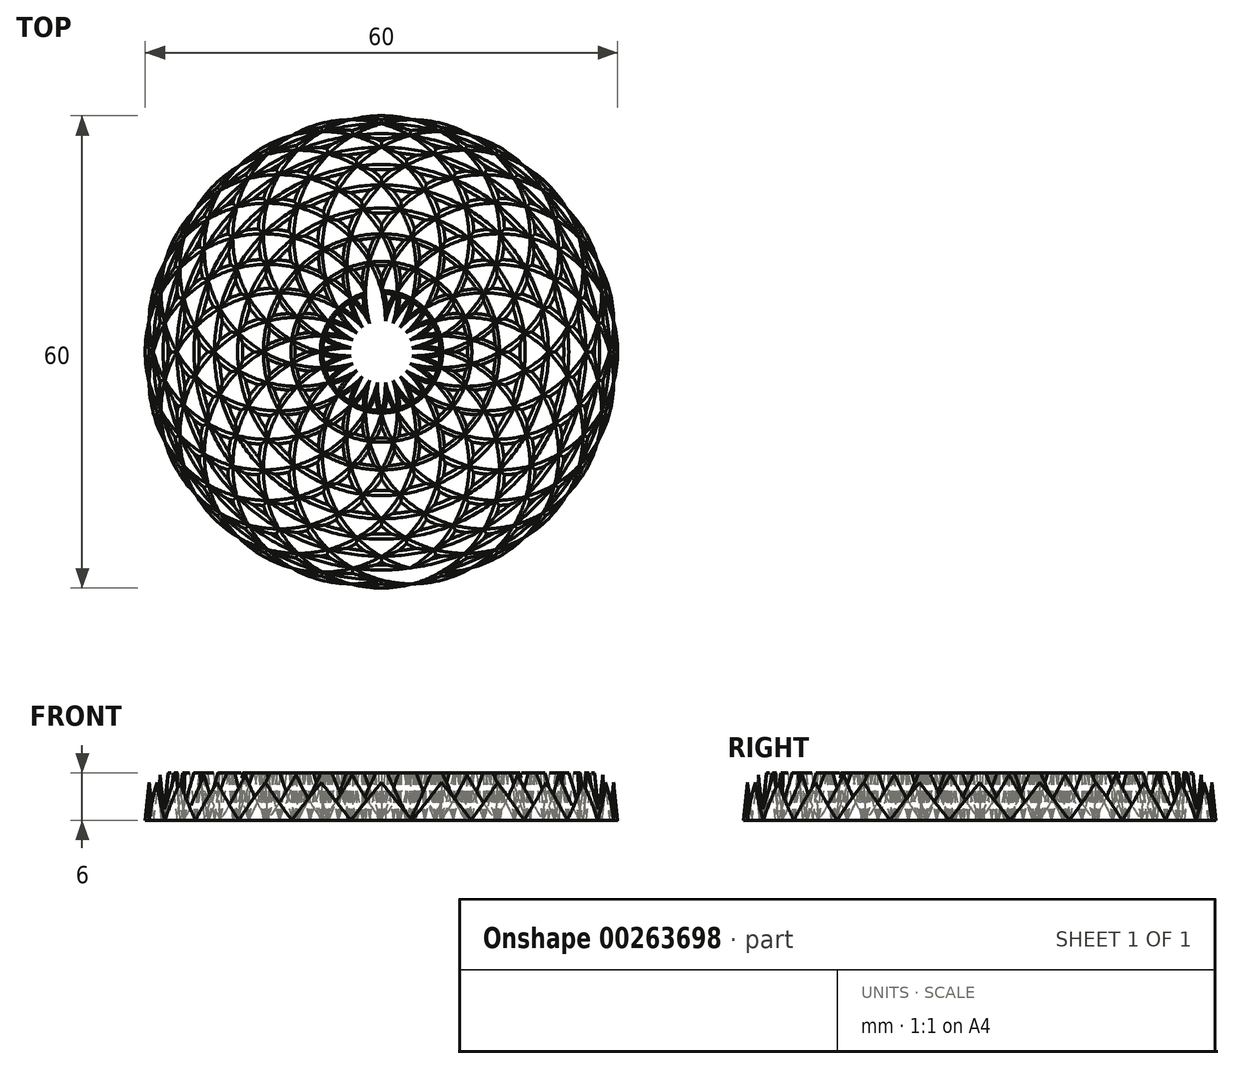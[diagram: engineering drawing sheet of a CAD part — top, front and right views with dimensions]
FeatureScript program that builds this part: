
annotation { "Feature Type Name" : "Feature", "Feature Type Description" : "" }
export const myFeature = defineFeature(function(context is Context, id is Id, definition is map)
    precondition{}
    {
        {
            var Q0;
            Q0=qCreatedBy(makeId("Top.planeOp"),FACE);
            var sketch = newSketch(context, id + "F0", { "sketchPlane" : qUnion([Q0])});
            skCircle(sketch, "E0", {"center": v(0, 0) * mm, "radius": 15 * mm});
            skLineSegment(sketch, "E1", {"start": v(-15, 0) * mm, "end": v(15, 0) * mm, "construction": true});
            skLineSegment(sketch, "E2", {"start": v(0, 15) * mm, "end": v(0, -15) * mm, "construction": true});
            skCircle(sketch, "E3", {"center": v(15, 0) * mm, "radius": 15 * mm});
            skCircle(sketch, "E4", {"center": v(7.5, 13) * mm, "radius": 15 * mm});
            skCircle(sketch, "E5", {"center": v(7.5, -13) * mm, "radius": 15 * mm});
            skCircle(sketch, "E6", {"center": v(-7.5, 13) * mm, "radius": 15 * mm});
            skCircle(sketch, "E7", {"center": v(-7.5, -13) * mm, "radius": 15 * mm});
            skCircle(sketch, "E8", {"center": v(-15, 0) * mm, "radius": 15 * mm});
            skLineSegment(sketch, "E9", {"start": v(0, 0) * mm, "end": v(22.5, 13) * mm, "construction": true});
            skCircle(sketch, "E10", {"center": v(13, 7.5) * mm, "radius": 15 * mm});
            skCircle(sketch, "E11", {"center": v(13, -7.5) * mm, "radius": 15 * mm});
            skCircle(sketch, "E12", {"center": v(0, -15) * mm, "radius": 15 * mm});
            skCircle(sketch, "E13", {"center": v(-13, -7.5) * mm, "radius": 15 * mm});
            skCircle(sketch, "E14", {"center": v(-13, 7.5) * mm, "radius": 15 * mm});
            skCircle(sketch, "E15", {"center": v(0, 15) * mm, "radius": 15 * mm});
            skLineSegment(sketch, "E16", {"start": v(7.5, 2) * mm, "end": v(20.5, 5.5) * mm, "construction": true});
            skCircle(sketch, "E17", {"center": v(14.49, 3.88) * mm, "radius": 15 * mm});
            skCircle(sketch, "E18", {"center": v(10.6, -10.6) * mm, "radius": 15 * mm});
            skCircle(sketch, "E19", {"center": v(-3.88, -14.49) * mm, "radius": 15 * mm});
            skCircle(sketch, "E20", {"center": v(-14.49, -3.88) * mm, "radius": 15 * mm});
            skCircle(sketch, "E21", {"center": v(-10.6, 10.6) * mm, "radius": 15 * mm});
            skCircle(sketch, "E22", {"center": v(3.88, 14.49) * mm, "radius": 15 * mm});
            skLineSegment(sketch, "E23", {"start": v(-2, 7.5) * mm, "end": v(-5.5, 20.5) * mm, "construction": true});
            skCircle(sketch, "E24", {"center": v(-3.88, 14.49) * mm, "radius": 15 * mm});
            skCircle(sketch, "E25", {"center": v(10.6, 10.6) * mm, "radius": 15 * mm});
            skCircle(sketch, "E26", {"center": v(14.49, -3.88) * mm, "radius": 15 * mm});
            skCircle(sketch, "E27", {"center": v(3.88, -14.49) * mm, "radius": 15 * mm});
            skCircle(sketch, "E28", {"center": v(-10.6, -10.6) * mm, "radius": 15 * mm});
            skCircle(sketch, "E29", {"center": v(-14.49, 3.88) * mm, "radius": 15 * mm});
            skCircle(sketch, "E30", {"center": v(0, 0) * mm, "radius": 18.26 * mm});
            skLineSegment(sketch, "E31", {"start": v(-6.99, 16.87) * mm, "end": v(-2.38, 18.1) * mm, "construction": true});
            skCircle(sketch, "E32", {"center": v(0, 0) * mm, "radius": 21.21 * mm});
            skLineSegment(sketch, "E33", {"start": v(0, 0) * mm, "end": v(7.5, 28) * mm, "construction": true});
            skCircle(sketch, "E34", {"center": v(0, 0) * mm, "radius": 28.98 * mm});
            skLineSegment(sketch, "E35", {"start": v(0, 0) * mm, "end": v(3.1, 23.6) * mm, "construction": true});
            skCircle(sketch, "E36", {"center": v(0, 0) * mm, "radius": 23.8 * mm});
            skLineSegment(sketch, "E37", {"start": v(0, 0) * mm, "end": v(-3.62, 27.48) * mm, "construction": true});
            skCircle(sketch, "E38", {"center": v(0, 0) * mm, "radius": 27.72 * mm});
            skLineSegment(sketch, "E39", {"start": v(0, 0) * mm, "end": v(-13, 22.5) * mm, "construction": true});
            skCircle(sketch, "E40", {"center": v(0, 0) * mm, "radius": 25.98 * mm});
            skLineSegment(sketch, "E41", {"start": v(0, 0) * mm, "end": v(-9.1, 6.99) * mm, "construction": true});
            skCircle(sketch, "E42", {"center": v(0, 0) * mm, "radius": 11.48 * mm});
            skLineSegment(sketch, "E43", {"start": v(0, 0) * mm, "end": v(-6.72, 3.88) * mm, "construction": true});
            skCircle(sketch, "E44", {"center": v(0, 0) * mm, "radius": 7.76 * mm});
            skLineSegment(sketch, "E45", {"start": v(0, 0) * mm, "end": v(-2.38, -3.1) * mm, "construction": true});
            skCircle(sketch, "E46", {"center": v(0, 0) * mm, "radius": 3.92 * mm});
            skSolve(sketch);
        }
        {
            var Q0;
            Q0=qCreatedBy(makeId("Top.planeOp"),FACE);
            cPlane(context, id + "F1", {"entities" : qUnion([Q0]), "cplaneType" : CPlaneType.OFFSET, "offset" : 0 * mm, "width" : 150 * mm, "height" : 150 * mm});
        }
        {
            var Q0;
            Q0=qCreatedBy(id+"F1.planeOp",FACE);
            var sketch = newSketch(context, id + "F2", { "sketchPlane" : qUnion([Q0])});
            skArc(sketch, "E47.0.0", {"start": v(-7.5, 2) * mm, "mid": v(-9.46, 1.88) * mm, "end": v(-11.38, 1.5) * mm});
            skArc(sketch, "E47.0.1", {"start": v(-11.38, 1.5) * mm, "mid": v(-9.62, 0.63) * mm, "end": v(-7.76, 0) * mm});
            skArc(sketch, "E48.0.1", {"start": v(-6.72, 3.88) * mm, "mid": v(-8.65, 4.27) * mm, "end": v(-10.6, 4.4) * mm});
            skArc(sketch, "E48.0.2", {"start": v(-10.6, 4.4) * mm, "mid": v(-9.13, 3.1) * mm, "end": v(-7.5, 2) * mm});
            skArc(sketch, "E49.0.1", {"start": v(-5.5, 5.5) * mm, "mid": v(-7.25, 6.36) * mm, "end": v(-9.1, 6.99) * mm});
            skArc(sketch, "E49.0.2", {"start": v(-9.1, 6.99) * mm, "mid": v(-8.02, 5.36) * mm, "end": v(-6.72, 3.88) * mm});
            skArc(sketch, "E50.0.0", {"start": v(-3.88, 6.72) * mm, "mid": v(-5.36, 8.02) * mm, "end": v(-6.99, 9.1) * mm});
            skArc(sketch, "E50.0.1", {"start": v(-6.99, 9.1) * mm, "mid": v(-6.36, 7.25) * mm, "end": v(-5.5, 5.5) * mm});
            skArc(sketch, "E51.0.1", {"start": v(-2, 7.5) * mm, "mid": v(-3.1, 9.13) * mm, "end": v(-4.4, 10.6) * mm});
            skArc(sketch, "E51.0.2", {"start": v(-4.4, 10.6) * mm, "mid": v(-4.27, 8.65) * mm, "end": v(-3.88, 6.72) * mm});
            skArc(sketch, "E52.0.1", {"start": v(0, 7.76) * mm, "mid": v(-0.63, 9.62) * mm, "end": v(-1.5, 11.38) * mm});
            skArc(sketch, "E52.0.2", {"start": v(-1.5, 11.38) * mm, "mid": v(-1.88, 9.46) * mm, "end": v(-2, 7.5) * mm});
            skArc(sketch, "E53.0.0", {"start": v(2, 7.5) * mm, "mid": v(1.88, 9.46) * mm, "end": v(1.5, 11.38) * mm});
            skArc(sketch, "E53.0.1", {"start": v(1.5, 11.38) * mm, "mid": v(0.63, 9.62) * mm, "end": v(0, 7.76) * mm});
            skArc(sketch, "E54.0.0", {"start": v(3.88, 6.72) * mm, "mid": v(4.27, 8.65) * mm, "end": v(4.4, 10.6) * mm});
            skArc(sketch, "E54.0.1", {"start": v(4.4, 10.6) * mm, "mid": v(3.1, 9.13) * mm, "end": v(2, 7.5) * mm});
            skArc(sketch, "E55.0.0", {"start": v(5.5, 5.5) * mm, "mid": v(6.36, 7.25) * mm, "end": v(6.99, 9.1) * mm});
            skArc(sketch, "E55.0.1", {"start": v(6.99, 9.1) * mm, "mid": v(5.36, 8.02) * mm, "end": v(3.88, 6.72) * mm});
            skArc(sketch, "E56.0.1", {"start": v(6.72, 3.88) * mm, "mid": v(8.02, 5.36) * mm, "end": v(9.1, 6.99) * mm});
            skArc(sketch, "E56.0.2", {"start": v(9.1, 6.99) * mm, "mid": v(7.25, 6.36) * mm, "end": v(5.5, 5.5) * mm});
            skArc(sketch, "E57.0.1", {"start": v(7.5, 2) * mm, "mid": v(9.13, 3.1) * mm, "end": v(10.6, 4.4) * mm});
            skArc(sketch, "E57.0.2", {"start": v(10.6, 4.4) * mm, "mid": v(8.65, 4.27) * mm, "end": v(6.72, 3.88) * mm});
            skArc(sketch, "E58.0.0", {"start": v(7.76, 0) * mm, "mid": v(9.62, 0.63) * mm, "end": v(11.38, 1.5) * mm});
            skArc(sketch, "E58.0.1", {"start": v(11.38, 1.5) * mm, "mid": v(9.46, 1.88) * mm, "end": v(7.5, 2) * mm});
            skArc(sketch, "E59.0.1", {"start": v(7.5, -2) * mm, "mid": v(9.46, -1.88) * mm, "end": v(11.38, -1.5) * mm});
            skArc(sketch, "E59.0.2", {"start": v(11.38, -1.5) * mm, "mid": v(9.62, -0.63) * mm, "end": v(7.76, 0) * mm});
            skArc(sketch, "E60.0.1", {"start": v(6.72, -3.88) * mm, "mid": v(8.65, -4.27) * mm, "end": v(10.6, -4.4) * mm});
            skArc(sketch, "E60.0.2", {"start": v(10.6, -4.4) * mm, "mid": v(9.13, -3.1) * mm, "end": v(7.5, -2) * mm});
            skArc(sketch, "E61.0.1", {"start": v(5.5, -5.5) * mm, "mid": v(7.25, -6.36) * mm, "end": v(9.1, -6.99) * mm});
            skArc(sketch, "E61.0.2", {"start": v(9.1, -6.99) * mm, "mid": v(8.02, -5.36) * mm, "end": v(6.72, -3.88) * mm});
            skArc(sketch, "E62.0.1", {"start": v(3.88, -6.72) * mm, "mid": v(5.36, -8.02) * mm, "end": v(6.99, -9.1) * mm});
            skArc(sketch, "E62.0.2", {"start": v(6.99, -9.1) * mm, "mid": v(6.36, -7.25) * mm, "end": v(5.5, -5.5) * mm});
            skArc(sketch, "E63.0.0", {"start": v(2, -7.5) * mm, "mid": v(3.1, -9.13) * mm, "end": v(4.4, -10.6) * mm});
            skArc(sketch, "E63.0.1", {"start": v(4.4, -10.6) * mm, "mid": v(4.27, -8.65) * mm, "end": v(3.88, -6.72) * mm});
            skArc(sketch, "E64.0.1", {"start": v(0, -7.76) * mm, "mid": v(0.63, -9.62) * mm, "end": v(1.5, -11.38) * mm});
            skArc(sketch, "E64.0.2", {"start": v(1.5, -11.38) * mm, "mid": v(1.88, -9.46) * mm, "end": v(2, -7.5) * mm});
            skArc(sketch, "E65.0.0", {"start": v(-2, -7.5) * mm, "mid": v(-1.88, -9.46) * mm, "end": v(-1.5, -11.38) * mm});
            skArc(sketch, "E65.0.1", {"start": v(-1.5, -11.38) * mm, "mid": v(-0.63, -9.62) * mm, "end": v(0, -7.76) * mm});
            skArc(sketch, "E66.0.1", {"start": v(-3.88, -6.72) * mm, "mid": v(-4.27, -8.65) * mm, "end": v(-4.4, -10.6) * mm});
            skArc(sketch, "E66.0.2", {"start": v(-4.4, -10.6) * mm, "mid": v(-3.1, -9.13) * mm, "end": v(-2, -7.5) * mm});
            skArc(sketch, "E67.0.0", {"start": v(-5.5, -5.5) * mm, "mid": v(-6.36, -7.25) * mm, "end": v(-6.99, -9.1) * mm});
            skArc(sketch, "E67.0.1", {"start": v(-6.99, -9.1) * mm, "mid": v(-5.36, -8.02) * mm, "end": v(-3.88, -6.72) * mm});
            skArc(sketch, "E68.0.1", {"start": v(-6.72, -3.88) * mm, "mid": v(-8.02, -5.36) * mm, "end": v(-9.1, -6.99) * mm});
            skArc(sketch, "E68.0.2", {"start": v(-9.1, -6.99) * mm, "mid": v(-7.25, -6.36) * mm, "end": v(-5.5, -5.5) * mm});
            skArc(sketch, "E69.0.1", {"start": v(-7.5, -2) * mm, "mid": v(-9.13, -3.1) * mm, "end": v(-10.6, -4.4) * mm});
            skArc(sketch, "E69.0.2", {"start": v(-10.6, -4.4) * mm, "mid": v(-8.65, -4.27) * mm, "end": v(-6.72, -3.88) * mm});
            skArc(sketch, "E70.0.1", {"start": v(-7.76, 0) * mm, "mid": v(-9.62, -0.63) * mm, "end": v(-11.38, -1.5) * mm});
            skArc(sketch, "E70.0.2", {"start": v(-11.38, -1.5) * mm, "mid": v(-9.46, -1.88) * mm, "end": v(-7.5, -2) * mm});
            skArc(sketch, "E71.0.1", {"start": v(-10.6, 4.4) * mm, "mid": v(-12.56, 4.27) * mm, "end": v(-14.49, 3.88) * mm});
            skArc(sketch, "E71.0.2", {"start": v(-14.49, 3.88) * mm, "mid": v(-13.01, 2.59) * mm, "end": v(-11.38, 1.5) * mm});
            skArc(sketch, "E72.0.1", {"start": v(-9.1, 6.99) * mm, "mid": v(-11.03, 7.37) * mm, "end": v(-13, 7.5) * mm});
            skArc(sketch, "E72.0.2", {"start": v(-13, 7.5) * mm, "mid": v(-11.9, 5.87) * mm, "end": v(-10.6, 4.4) * mm});
            skArc(sketch, "E73.0.1", {"start": v(-6.99, 9.1) * mm, "mid": v(-8.75, 9.98) * mm, "end": v(-10.6, 10.6) * mm});
            skArc(sketch, "E73.0.2", {"start": v(-10.6, 10.6) * mm, "mid": v(-9.98, 8.75) * mm, "end": v(-9.1, 6.99) * mm});
            skArc(sketch, "E74.0.1", {"start": v(-4.4, 10.6) * mm, "mid": v(-5.87, 11.9) * mm, "end": v(-7.5, 13) * mm});
            skArc(sketch, "E74.0.2", {"start": v(-7.5, 13) * mm, "mid": v(-7.37, 11.03) * mm, "end": v(-6.99, 9.1) * mm});
            skArc(sketch, "E75.0.1", {"start": v(-1.5, 11.38) * mm, "mid": v(-2.59, 13.01) * mm, "end": v(-3.88, 14.49) * mm});
            skArc(sketch, "E75.0.2", {"start": v(-3.88, 14.49) * mm, "mid": v(-4.27, 12.56) * mm, "end": v(-4.4, 10.6) * mm});
            skArc(sketch, "E76.0.0", {"start": v(1.5, 11.38) * mm, "mid": v(0.87, 13.24) * mm, "end": v(0, 15) * mm});
            skArc(sketch, "E76.0.1", {"start": v(0, 15) * mm, "mid": v(-0.87, 13.24) * mm, "end": v(-1.5, 11.38) * mm});
            skArc(sketch, "E77.0.1", {"start": v(4.4, 10.6) * mm, "mid": v(4.27, 12.56) * mm, "end": v(3.88, 14.49) * mm});
            skArc(sketch, "E77.0.2", {"start": v(3.88, 14.49) * mm, "mid": v(2.59, 13.01) * mm, "end": v(1.5, 11.38) * mm});
            skArc(sketch, "E78.0.1", {"start": v(6.99, 9.1) * mm, "mid": v(7.37, 11.03) * mm, "end": v(7.5, 13) * mm});
            skArc(sketch, "E78.0.2", {"start": v(7.5, 13) * mm, "mid": v(5.87, 11.9) * mm, "end": v(4.4, 10.6) * mm});
            skArc(sketch, "E79.0.1", {"start": v(9.1, 6.99) * mm, "mid": v(9.98, 8.75) * mm, "end": v(10.6, 10.6) * mm});
            skArc(sketch, "E79.0.2", {"start": v(10.6, 10.6) * mm, "mid": v(8.75, 9.98) * mm, "end": v(6.99, 9.1) * mm});
            skArc(sketch, "E80.0.0", {"start": v(10.6, 4.4) * mm, "mid": v(11.9, 5.87) * mm, "end": v(13, 7.5) * mm});
            skArc(sketch, "E80.0.1", {"start": v(13, 7.5) * mm, "mid": v(11.03, 7.37) * mm, "end": v(9.1, 6.99) * mm});
            skArc(sketch, "E81.0.1", {"start": v(11.38, 1.5) * mm, "mid": v(13.01, 2.59) * mm, "end": v(14.49, 3.88) * mm});
            skArc(sketch, "E81.0.2", {"start": v(14.49, 3.88) * mm, "mid": v(12.56, 4.27) * mm, "end": v(10.6, 4.4) * mm});
            skArc(sketch, "E82.0.0", {"start": v(11.38, -1.5) * mm, "mid": v(13.24, -0.87) * mm, "end": v(15, 0) * mm});
            skArc(sketch, "E82.0.1", {"start": v(15, 0) * mm, "mid": v(13.24, 0.87) * mm, "end": v(11.38, 1.5) * mm});
            skArc(sketch, "E83.0.1", {"start": v(10.6, -4.4) * mm, "mid": v(12.56, -4.27) * mm, "end": v(14.49, -3.88) * mm});
            skArc(sketch, "E83.0.2", {"start": v(14.49, -3.88) * mm, "mid": v(13.01, -2.59) * mm, "end": v(11.38, -1.5) * mm});
            skArc(sketch, "E84.0.1", {"start": v(9.1, -6.99) * mm, "mid": v(11.03, -7.37) * mm, "end": v(13, -7.5) * mm});
            skArc(sketch, "E84.0.2", {"start": v(13, -7.5) * mm, "mid": v(11.9, -5.87) * mm, "end": v(10.6, -4.4) * mm});
            skArc(sketch, "E85.0.1", {"start": v(6.99, -9.1) * mm, "mid": v(8.75, -9.98) * mm, "end": v(10.6, -10.6) * mm});
            skArc(sketch, "E85.0.2", {"start": v(10.6, -10.6) * mm, "mid": v(9.98, -8.75) * mm, "end": v(9.1, -6.99) * mm});
            skArc(sketch, "E86.0.0", {"start": v(4.4, -10.6) * mm, "mid": v(5.87, -11.9) * mm, "end": v(7.5, -13) * mm});
            skArc(sketch, "E86.0.1", {"start": v(7.5, -13) * mm, "mid": v(7.37, -11.03) * mm, "end": v(6.99, -9.1) * mm});
            skArc(sketch, "E87.0.1", {"start": v(1.5, -11.38) * mm, "mid": v(2.59, -13.01) * mm, "end": v(3.88, -14.49) * mm});
            skArc(sketch, "E87.0.2", {"start": v(3.88, -14.49) * mm, "mid": v(4.27, -12.56) * mm, "end": v(4.4, -10.6) * mm});
            skArc(sketch, "E88.0.1", {"start": v(-1.5, -11.38) * mm, "mid": v(-0.87, -13.24) * mm, "end": v(0, -15) * mm});
            skArc(sketch, "E88.0.2", {"start": v(0, -15) * mm, "mid": v(0.87, -13.24) * mm, "end": v(1.5, -11.38) * mm});
            skArc(sketch, "E89.0.1", {"start": v(-4.4, -10.6) * mm, "mid": v(-4.27, -12.56) * mm, "end": v(-3.88, -14.49) * mm});
            skArc(sketch, "E89.0.2", {"start": v(-3.88, -14.49) * mm, "mid": v(-2.59, -13.01) * mm, "end": v(-1.5, -11.38) * mm});
            skArc(sketch, "E90.0.1", {"start": v(-6.99, -9.1) * mm, "mid": v(-7.37, -11.03) * mm, "end": v(-7.5, -13) * mm});
            skArc(sketch, "E90.0.2", {"start": v(-7.5, -13) * mm, "mid": v(-5.87, -11.9) * mm, "end": v(-4.4, -10.6) * mm});
            skArc(sketch, "E91.0.0", {"start": v(-9.1, -6.99) * mm, "mid": v(-9.98, -8.75) * mm, "end": v(-10.6, -10.6) * mm});
            skArc(sketch, "E91.0.1", {"start": v(-10.6, -10.6) * mm, "mid": v(-8.75, -9.98) * mm, "end": v(-6.99, -9.1) * mm});
            skArc(sketch, "E92.0.1", {"start": v(-10.6, -4.4) * mm, "mid": v(-11.9, -5.87) * mm, "end": v(-13, -7.5) * mm});
            skArc(sketch, "E92.0.2", {"start": v(-13, -7.5) * mm, "mid": v(-11.03, -7.37) * mm, "end": v(-9.1, -6.99) * mm});
            skArc(sketch, "E93.0.0", {"start": v(-11.38, -1.5) * mm, "mid": v(-13.01, -2.59) * mm, "end": v(-14.49, -3.88) * mm});
            skArc(sketch, "E93.0.1", {"start": v(-14.49, -3.88) * mm, "mid": v(-12.56, -4.27) * mm, "end": v(-10.6, -4.4) * mm});
            skArc(sketch, "E94.0.1", {"start": v(-11.38, 1.5) * mm, "mid": v(-13.24, 0.87) * mm, "end": v(-15, 0) * mm});
            skArc(sketch, "E94.0.2", {"start": v(-15, 0) * mm, "mid": v(-13.24, -0.87) * mm, "end": v(-11.38, -1.5) * mm});
            skArc(sketch, "E95.0.0", {"start": v(-3.88, 6.72) * mm, "mid": v(-2.59, 5.25) * mm, "end": v(-1.5, 3.62) * mm});
            skArc(sketch, "E95.0.1", {"start": v(-1.5, 3.62) * mm, "mid": v(-1.88, 5.54) * mm, "end": v(-2, 7.5) * mm});
            skArc(sketch, "E95.0.2", {"start": v(-2, 7.5) * mm, "mid": v(-2.97, 7.17) * mm, "end": v(-3.88, 6.72) * mm});
            skArc(sketch, "E96.0.0", {"start": v(-2.38, 3.1) * mm, "mid": v(-3.25, 4.87) * mm, "end": v(-3.88, 6.72) * mm});
            skArc(sketch, "E96.0.1", {"start": v(-3.88, 6.72) * mm, "mid": v(-4.73, 6.16) * mm, "end": v(-5.5, 5.5) * mm});
            skArc(sketch, "E96.0.2", {"start": v(-5.5, 5.5) * mm, "mid": v(-3.86, 4.4) * mm, "end": v(-2.38, 3.1) * mm});
            skArc(sketch, "E97.0.0", {"start": v(-6.72, 3.88) * mm, "mid": v(-4.87, 3.25) * mm, "end": v(-3.1, 2.38) * mm});
            skArc(sketch, "E97.0.1", {"start": v(-3.1, 2.38) * mm, "mid": v(-4.4, 3.86) * mm, "end": v(-5.5, 5.5) * mm});
            skArc(sketch, "E98.0.0", {"start": v(-3.62, 1.5) * mm, "mid": v(-5.25, 2.59) * mm, "end": v(-6.72, 3.88) * mm});
            skArc(sketch, "E98.0.1", {"start": v(-6.72, 3.88) * mm, "mid": v(-7.17, 2.97) * mm, "end": v(-7.5, 2) * mm});
            skArc(sketch, "E98.0.2", {"start": v(-7.5, 2) * mm, "mid": v(-5.54, 1.88) * mm, "end": v(-3.62, 1.5) * mm});
            skArc(sketch, "E99.0.0", {"start": v(-3.88, 0.51) * mm, "mid": v(-5.74, 1.14) * mm, "end": v(-7.5, 2) * mm});
            skArc(sketch, "E99.0.1", {"start": v(-7.5, 2) * mm, "mid": v(-7.7, 1.01) * mm, "end": v(-7.76, 0) * mm});
            skArc(sketch, "E99.0.2", {"start": v(-7.76, 0) * mm, "mid": v(-5.84, 0.38) * mm, "end": v(-3.88, 0.51) * mm});
            skArc(sketch, "E100.0.0", {"start": v(-3.88, -0.51) * mm, "mid": v(-5.84, -0.38) * mm, "end": v(-7.76, 0) * mm});
            skArc(sketch, "E100.0.1", {"start": v(-7.76, 0) * mm, "mid": v(-7.7, -1.01) * mm, "end": v(-7.5, -2) * mm});
            skArc(sketch, "E100.0.2", {"start": v(-7.5, -2) * mm, "mid": v(-5.74, -1.14) * mm, "end": v(-3.88, -0.51) * mm});
            skArc(sketch, "E101.0.0", {"start": v(-3.62, -1.5) * mm, "mid": v(-5.54, -1.88) * mm, "end": v(-7.5, -2) * mm});
            skArc(sketch, "E101.0.1", {"start": v(-7.5, -2) * mm, "mid": v(-7.17, -2.97) * mm, "end": v(-6.72, -3.88) * mm});
            skArc(sketch, "E101.0.2", {"start": v(-6.72, -3.88) * mm, "mid": v(-5.25, -2.59) * mm, "end": v(-3.62, -1.5) * mm});
            skArc(sketch, "E102.0.0", {"start": v(-5.5, -5.5) * mm, "mid": v(-4.4, -3.86) * mm, "end": v(-3.1, -2.38) * mm});
            skArc(sketch, "E102.0.1", {"start": v(-3.1, -2.38) * mm, "mid": v(-4.87, -3.25) * mm, "end": v(-6.72, -3.88) * mm});
            skArc(sketch, "E102.0.2", {"start": v(-6.72, -3.88) * mm, "mid": v(-6.16, -4.73) * mm, "end": v(-5.5, -5.5) * mm});
            skArc(sketch, "E103.0.0", {"start": v(-2.38, -3.1) * mm, "mid": v(-3.86, -4.4) * mm, "end": v(-5.5, -5.5) * mm});
            skArc(sketch, "E103.0.1", {"start": v(-5.5, -5.5) * mm, "mid": v(-4.73, -6.16) * mm, "end": v(-3.88, -6.72) * mm});
            skArc(sketch, "E103.0.2", {"start": v(-3.88, -6.72) * mm, "mid": v(-3.25, -4.87) * mm, "end": v(-2.38, -3.1) * mm});
            skArc(sketch, "E104.0.0", {"start": v(-1.5, -3.62) * mm, "mid": v(-2.59, -5.25) * mm, "end": v(-3.88, -6.72) * mm});
            skArc(sketch, "E104.0.1", {"start": v(-3.88, -6.72) * mm, "mid": v(-2.97, -7.17) * mm, "end": v(-2, -7.5) * mm});
            skArc(sketch, "E104.0.2", {"start": v(-2, -7.5) * mm, "mid": v(-1.88, -5.54) * mm, "end": v(-1.5, -3.62) * mm});
            skArc(sketch, "E105.0.0", {"start": v(0, -7.76) * mm, "mid": v(-0.38, -5.84) * mm, "end": v(-0.51, -3.88) * mm});
            skArc(sketch, "E105.0.1", {"start": v(-0.51, -3.88) * mm, "mid": v(-1.14, -5.74) * mm, "end": v(-2, -7.5) * mm});
            skArc(sketch, "E105.0.2", {"start": v(-2, -7.5) * mm, "mid": v(-1.01, -7.7) * mm, "end": v(0, -7.76) * mm});
            skArc(sketch, "E106.0.0", {"start": v(0.51, -3.88) * mm, "mid": v(0.38, -5.84) * mm, "end": v(0, -7.76) * mm});
            skArc(sketch, "E106.0.1", {"start": v(0, -7.76) * mm, "mid": v(1.01, -7.7) * mm, "end": v(2, -7.5) * mm});
            skArc(sketch, "E106.0.2", {"start": v(2, -7.5) * mm, "mid": v(1.14, -5.74) * mm, "end": v(0.51, -3.88) * mm});
            skArc(sketch, "E107.0.0", {"start": v(1.5, -3.62) * mm, "mid": v(1.88, -5.54) * mm, "end": v(2, -7.5) * mm});
            skArc(sketch, "E107.0.1", {"start": v(2, -7.5) * mm, "mid": v(2.97, -7.17) * mm, "end": v(3.88, -6.72) * mm});
            skArc(sketch, "E107.0.2", {"start": v(3.88, -6.72) * mm, "mid": v(2.59, -5.25) * mm, "end": v(1.5, -3.62) * mm});
            skArc(sketch, "E108.0.0", {"start": v(2.38, -3.1) * mm, "mid": v(3.25, -4.87) * mm, "end": v(3.88, -6.72) * mm});
            skArc(sketch, "E108.0.1", {"start": v(3.88, -6.72) * mm, "mid": v(4.73, -6.16) * mm, "end": v(5.5, -5.5) * mm});
            skArc(sketch, "E108.0.2", {"start": v(5.5, -5.5) * mm, "mid": v(3.86, -4.4) * mm, "end": v(2.38, -3.1) * mm});
            skArc(sketch, "E109.0.0", {"start": v(3.1, -2.38) * mm, "mid": v(4.4, -3.86) * mm, "end": v(5.5, -5.5) * mm});
            skArc(sketch, "E109.0.1", {"start": v(5.5, -5.5) * mm, "mid": v(6.16, -4.73) * mm, "end": v(6.72, -3.88) * mm});
            skArc(sketch, "E109.0.2", {"start": v(6.72, -3.88) * mm, "mid": v(4.87, -3.25) * mm, "end": v(3.1, -2.38) * mm});
            skArc(sketch, "E110.0.0", {"start": v(7.5, -2) * mm, "mid": v(5.54, -1.88) * mm, "end": v(3.62, -1.5) * mm});
            skArc(sketch, "E110.0.1", {"start": v(3.62, -1.5) * mm, "mid": v(5.25, -2.59) * mm, "end": v(6.72, -3.88) * mm});
            skArc(sketch, "E110.0.2", {"start": v(6.72, -3.88) * mm, "mid": v(7.17, -2.97) * mm, "end": v(7.5, -2) * mm});
            skArc(sketch, "E111.0.0", {"start": v(3.88, -0.51) * mm, "mid": v(5.74, -1.14) * mm, "end": v(7.5, -2) * mm});
            skArc(sketch, "E111.0.1", {"start": v(7.5, -2) * mm, "mid": v(7.7, -1.01) * mm, "end": v(7.76, 0) * mm});
            skArc(sketch, "E111.0.2", {"start": v(7.76, 0) * mm, "mid": v(5.84, -0.38) * mm, "end": v(3.88, -0.51) * mm});
            skArc(sketch, "E112.0.0", {"start": v(7.5, 2) * mm, "mid": v(5.74, 1.14) * mm, "end": v(3.88, 0.51) * mm});
            skArc(sketch, "E112.0.1", {"start": v(3.88, 0.51) * mm, "mid": v(5.84, 0.38) * mm, "end": v(7.76, 0) * mm});
            skArc(sketch, "E112.0.2", {"start": v(7.76, 0) * mm, "mid": v(7.7, 1.01) * mm, "end": v(7.5, 2) * mm});
            skArc(sketch, "E113.0.0", {"start": v(6.72, 3.88) * mm, "mid": v(5.25, 2.59) * mm, "end": v(3.62, 1.5) * mm});
            skArc(sketch, "E113.0.1", {"start": v(3.62, 1.5) * mm, "mid": v(5.54, 1.88) * mm, "end": v(7.5, 2) * mm});
            skArc(sketch, "E113.0.2", {"start": v(7.5, 2) * mm, "mid": v(7.17, 2.97) * mm, "end": v(6.72, 3.88) * mm});
            skArc(sketch, "E114.0.0", {"start": v(3.1, 2.38) * mm, "mid": v(4.87, 3.25) * mm, "end": v(6.72, 3.88) * mm});
            skArc(sketch, "E114.0.1", {"start": v(6.72, 3.88) * mm, "mid": v(6.16, 4.73) * mm, "end": v(5.5, 5.5) * mm});
            skArc(sketch, "E114.0.2", {"start": v(5.5, 5.5) * mm, "mid": v(4.4, 3.86) * mm, "end": v(3.1, 2.38) * mm});
            skArc(sketch, "E115.0.0", {"start": v(2.38, 3.1) * mm, "mid": v(3.86, 4.4) * mm, "end": v(5.5, 5.5) * mm});
            skArc(sketch, "E115.0.1", {"start": v(5.5, 5.5) * mm, "mid": v(4.73, 6.16) * mm, "end": v(3.88, 6.72) * mm});
            skArc(sketch, "E115.0.2", {"start": v(3.88, 6.72) * mm, "mid": v(3.25, 4.87) * mm, "end": v(2.38, 3.1) * mm});
            skArc(sketch, "E116.0.0", {"start": v(1.5, 3.62) * mm, "mid": v(2.59, 5.25) * mm, "end": v(3.88, 6.72) * mm});
            skArc(sketch, "E116.0.1", {"start": v(3.88, 6.72) * mm, "mid": v(2.97, 7.17) * mm, "end": v(2, 7.5) * mm});
            skArc(sketch, "E116.0.2", {"start": v(2, 7.5) * mm, "mid": v(1.88, 5.54) * mm, "end": v(1.5, 3.62) * mm});
            skArc(sketch, "E117.0.0", {"start": v(0.51, 3.88) * mm, "mid": v(1.14, 5.74) * mm, "end": v(2, 7.5) * mm});
            skArc(sketch, "E117.0.1", {"start": v(2, 7.5) * mm, "mid": v(1.01, 7.7) * mm, "end": v(0, 7.76) * mm});
            skArc(sketch, "E117.0.2", {"start": v(0, 7.76) * mm, "mid": v(0.38, 5.84) * mm, "end": v(0.51, 3.88) * mm});
            skArc(sketch, "E118.0.0", {"start": v(-2, 7.5) * mm, "mid": v(-1.14, 5.74) * mm, "end": v(-0.51, 3.88) * mm});
            skArc(sketch, "E118.0.1", {"start": v(-0.51, 3.88) * mm, "mid": v(-0.38, 5.84) * mm, "end": v(0, 7.76) * mm});
            skArc(sketch, "E118.0.2", {"start": v(0, 7.76) * mm, "mid": v(-1.01, 7.7) * mm, "end": v(-2, 7.5) * mm});
            skArc(sketch, "E119.0.0", {"start": v(0, 0) * mm, "mid": v(0.87, 1.76) * mm, "end": v(1.5, 3.62) * mm});
            skArc(sketch, "E119.0.1", {"start": v(1.5, 3.62) * mm, "mid": v(0.63, 1.86) * mm, "end": v(0, 0) * mm});
            skArc(sketch, "E120.0.0", {"start": v(0, 0) * mm, "mid": v(1.3, 1.48) * mm, "end": v(2.38, 3.1) * mm});
            skArc(sketch, "E120.0.1", {"start": v(2.38, 3.1) * mm, "mid": v(1.1, 1.63) * mm, "end": v(0, 0) * mm});
            skArc(sketch, "E121.0.0", {"start": v(3.1, 2.38) * mm, "mid": v(1.48, 1.3) * mm, "end": v(0, 0) * mm});
            skArc(sketch, "E121.0.1", {"start": v(0, 0) * mm, "mid": v(1.63, 1.1) * mm, "end": v(3.1, 2.38) * mm});
            skArc(sketch, "E122.0.0", {"start": v(3.62, 1.5) * mm, "mid": v(1.76, 0.87) * mm, "end": v(0, 0) * mm});
            skArc(sketch, "E122.0.1", {"start": v(0, 0) * mm, "mid": v(1.86, 0.63) * mm, "end": v(3.62, 1.5) * mm});
            skArc(sketch, "E123.0.0", {"start": v(3.88, 0.51) * mm, "mid": v(1.92, 0.38) * mm, "end": v(0, 0) * mm});
            skArc(sketch, "E123.0.1", {"start": v(0, 0) * mm, "mid": v(1.96, 0.13) * mm, "end": v(3.88, 0.51) * mm});
            skArc(sketch, "E124.0.0", {"start": v(3.88, -0.51) * mm, "mid": v(1.96, -0.13) * mm, "end": v(0, 0) * mm});
            skArc(sketch, "E124.0.1", {"start": v(0, 0) * mm, "mid": v(1.92, -0.38) * mm, "end": v(3.88, -0.51) * mm});
            skArc(sketch, "E125.0.0", {"start": v(3.62, -1.5) * mm, "mid": v(1.86, -0.63) * mm, "end": v(0, 0) * mm});
            skArc(sketch, "E125.0.1", {"start": v(0, 0) * mm, "mid": v(1.76, -0.87) * mm, "end": v(3.62, -1.5) * mm});
            skArc(sketch, "E126.0.0", {"start": v(3.1, -2.38) * mm, "mid": v(1.63, -1.1) * mm, "end": v(0, 0) * mm});
            skArc(sketch, "E126.0.1", {"start": v(0, 0) * mm, "mid": v(1.48, -1.3) * mm, "end": v(3.1, -2.38) * mm});
            skArc(sketch, "E127.0.0", {"start": v(0, 0) * mm, "mid": v(1.1, -1.63) * mm, "end": v(2.38, -3.1) * mm});
            skArc(sketch, "E127.0.1", {"start": v(2.38, -3.1) * mm, "mid": v(1.3, -1.48) * mm, "end": v(0, 0) * mm});
            skArc(sketch, "E128.0.0", {"start": v(0, 0) * mm, "mid": v(0.63, -1.86) * mm, "end": v(1.5, -3.62) * mm});
            skArc(sketch, "E128.0.1", {"start": v(1.5, -3.62) * mm, "mid": v(0.87, -1.76) * mm, "end": v(0, 0) * mm});
            skArc(sketch, "E129.0.0", {"start": v(0, 0) * mm, "mid": v(0.13, -1.96) * mm, "end": v(0.51, -3.88) * mm});
            skArc(sketch, "E129.0.1", {"start": v(0.51, -3.88) * mm, "mid": v(0.38, -1.92) * mm, "end": v(0, 0) * mm});
            skArc(sketch, "E130.0.0", {"start": v(-0.51, -3.88) * mm, "mid": v(-0.13, -1.96) * mm, "end": v(0, 0) * mm});
            skArc(sketch, "E130.0.1", {"start": v(0, 0) * mm, "mid": v(-0.38, -1.92) * mm, "end": v(-0.51, -3.88) * mm});
            skArc(sketch, "E131.0.0", {"start": v(0, 0) * mm, "mid": v(-0.87, -1.76) * mm, "end": v(-1.5, -3.62) * mm});
            skArc(sketch, "E131.0.1", {"start": v(-1.5, -3.62) * mm, "mid": v(-0.63, -1.86) * mm, "end": v(0, 0) * mm});
            skArc(sketch, "E132.0.0", {"start": v(0, 0) * mm, "mid": v(-1.3, -1.48) * mm, "end": v(-2.38, -3.1) * mm});
            skArc(sketch, "E132.0.1", {"start": v(-2.38, -3.1) * mm, "mid": v(-1.1, -1.63) * mm, "end": v(0, 0) * mm});
            skArc(sketch, "E133.0.0", {"start": v(-3.1, -2.38) * mm, "mid": v(-1.48, -1.3) * mm, "end": v(0, 0) * mm});
            skArc(sketch, "E133.0.1", {"start": v(0, 0) * mm, "mid": v(-1.63, -1.1) * mm, "end": v(-3.1, -2.38) * mm});
            skArc(sketch, "E134.0.0", {"start": v(-3.62, -1.5) * mm, "mid": v(-1.76, -0.87) * mm, "end": v(0, 0) * mm});
            skArc(sketch, "E134.0.1", {"start": v(0, 0) * mm, "mid": v(-1.86, -0.63) * mm, "end": v(-3.62, -1.5) * mm});
            skArc(sketch, "E135.0.0", {"start": v(0, 0) * mm, "mid": v(-1.96, -0.13) * mm, "end": v(-3.88, -0.51) * mm});
            skArc(sketch, "E135.0.1", {"start": v(-3.88, -0.51) * mm, "mid": v(-1.92, -0.38) * mm, "end": v(0, 0) * mm});
            skArc(sketch, "E136.0.0", {"start": v(0, 0) * mm, "mid": v(-1.92, 0.38) * mm, "end": v(-3.88, 0.51) * mm});
            skArc(sketch, "E136.0.1", {"start": v(-3.88, 0.51) * mm, "mid": v(-1.96, 0.13) * mm, "end": v(0, 0) * mm});
            skArc(sketch, "E137.0.0", {"start": v(0, 0) * mm, "mid": v(-1.76, 0.87) * mm, "end": v(-3.62, 1.5) * mm});
            skArc(sketch, "E137.0.1", {"start": v(-3.62, 1.5) * mm, "mid": v(-1.86, 0.63) * mm, "end": v(0, 0) * mm});
            skArc(sketch, "E138.0.0", {"start": v(-3.1, 2.38) * mm, "mid": v(-1.63, 1.1) * mm, "end": v(0, 0) * mm});
            skArc(sketch, "E138.0.1", {"start": v(0, 0) * mm, "mid": v(-1.48, 1.3) * mm, "end": v(-3.1, 2.38) * mm});
            skArc(sketch, "E139.0.0", {"start": v(-2.38, 3.1) * mm, "mid": v(-1.3, 1.48) * mm, "end": v(0, 0) * mm});
            skArc(sketch, "E139.0.1", {"start": v(0, 0) * mm, "mid": v(-1.1, 1.63) * mm, "end": v(-2.38, 3.1) * mm});
            skArc(sketch, "E140.0.0", {"start": v(-1.5, 3.62) * mm, "mid": v(-0.87, 1.76) * mm, "end": v(0, 0) * mm});
            skArc(sketch, "E140.0.1", {"start": v(0, 0) * mm, "mid": v(-0.63, 1.86) * mm, "end": v(-1.5, 3.62) * mm});
            skArc(sketch, "E141.0.0", {"start": v(0, 0) * mm, "mid": v(-0.13, 1.96) * mm, "end": v(-0.51, 3.88) * mm});
            skArc(sketch, "E141.0.1", {"start": v(-0.51, 3.88) * mm, "mid": v(-0.38, 1.92) * mm, "end": v(0, 0) * mm});
            skArc(sketch, "E142.0.0", {"start": v(0, 0) * mm, "mid": v(0.38, 1.92) * mm, "end": v(0.51, 3.88) * mm});
            skArc(sketch, "E142.0.1", {"start": v(0.51, 3.88) * mm, "mid": v(0.13, 1.96) * mm, "end": v(0, 0) * mm});
            skCircle(sketch, "E143.0", {"center": v(0, 0) * mm, "radius": 7.76 * mm});
            skCircle(sketch, "E144.0", {"center": v(0, 0) * mm, "radius": 11.48 * mm});
            skCircle(sketch, "E145.0", {"center": v(0, 0) * mm, "radius": 15 * mm});
            skCircle(sketch, "E146.0", {"center": v(0, 0) * mm, "radius": 18.26 * mm});
            skCircle(sketch, "E147.0", {"center": v(0, 0) * mm, "radius": 21.21 * mm});
            skCircle(sketch, "E148.0", {"center": v(0, 0) * mm, "radius": 23.8 * mm});
            skCircle(sketch, "E149.0", {"center": v(0, 0) * mm, "radius": 25.98 * mm});
            skCircle(sketch, "E150.0", {"center": v(0, 0) * mm, "radius": 27.72 * mm});
            skCircle(sketch, "E151.0", {"center": v(0, 0) * mm, "radius": 28.98 * mm});
            skSolve(sketch);
        }
        {
            var Q0;
            Q0=makeQuery(id+"F2.imprint","IMPRINT",FACE,{"disambiguationData":[TD([[makeQuery(id+"F2.imprint","IMPRINT",EDGE,{"derivedFrom":sQuery(id+"F2.wireOp",EDGE,"E117.0.2")}),-1.0]])]});
            var Q1;
            Q1=makeQuery(id+"F2.imprint","IMPRINT",FACE,{"disambiguationData":[TD([[makeQuery(id+"F2.imprint","IMPRINT",EDGE,{"derivedFrom":sQuery(id+"F2.wireOp",EDGE,"E116.0.2")}),-1.0]])]});
            var Q2;
            Q2=makeQuery(id+"F2.imprint","IMPRINT",FACE,{"disambiguationData":[TD([[makeQuery(id+"F2.imprint","IMPRINT",EDGE,{"derivedFrom":sQuery(id+"F2.wireOp",EDGE,"E115.0.2")}),-1.0]])]});
            var Q3;
            Q3=makeQuery(id+"F2.imprint","IMPRINT",FACE,{"disambiguationData":[TD([[makeQuery(id+"F2.imprint","IMPRINT",EDGE,{"derivedFrom":sQuery(id+"F2.wireOp",EDGE,"E114.0.2")}),-1.0]])]});
            var Q4;
            Q4=makeQuery(id+"F2.imprint","IMPRINT",FACE,{"disambiguationData":[TD([[makeQuery(id+"F2.imprint","IMPRINT",EDGE,{"derivedFrom":sQuery(id+"F2.wireOp",EDGE,"E113.0.0")}),-1.0]])]});
            var Q5;
            Q5=makeQuery(id+"F2.imprint","IMPRINT",FACE,{"disambiguationData":[TD([[makeQuery(id+"F2.imprint","IMPRINT",EDGE,{"derivedFrom":sQuery(id+"F2.wireOp",EDGE,"E112.0.0")}),-1.0]])]});
            var Q6;
            Q6=makeQuery(id+"F2.imprint","IMPRINT",FACE,{"disambiguationData":[TD([[makeQuery(id+"F2.imprint","IMPRINT",EDGE,{"derivedFrom":sQuery(id+"F2.wireOp",EDGE,"E111.0.2")}),-1.0]])]});
            var Q7;
            Q7=makeQuery(id+"F2.imprint","IMPRINT",FACE,{"disambiguationData":[TD([[makeQuery(id+"F2.imprint","IMPRINT",EDGE,{"derivedFrom":sQuery(id+"F2.wireOp",EDGE,"E110.0.0")}),-1.0]])]});
            var Q8;
            Q8=makeQuery(id+"F2.imprint","IMPRINT",FACE,{"disambiguationData":[TD([[makeQuery(id+"F2.imprint","IMPRINT",EDGE,{"derivedFrom":sQuery(id+"F2.wireOp",EDGE,"E109.0.2")}),-1.0]])]});
            var Q9;
            Q9=makeQuery(id+"F2.imprint","IMPRINT",FACE,{"disambiguationData":[TD([[makeQuery(id+"F2.imprint","IMPRINT",EDGE,{"derivedFrom":sQuery(id+"F2.wireOp",EDGE,"E108.0.2")}),-1.0]])]});
            var Q10;
            Q10=makeQuery(id+"F2.imprint","IMPRINT",FACE,{"disambiguationData":[TD([[makeQuery(id+"F2.imprint","IMPRINT",EDGE,{"derivedFrom":sQuery(id+"F2.wireOp",EDGE,"E106.0.2")}),-1.0]])]});
            var Q11;
            Q11=makeQuery(id+"F2.imprint","IMPRINT",FACE,{"disambiguationData":[TD([[makeQuery(id+"F2.imprint","IMPRINT",EDGE,{"derivedFrom":sQuery(id+"F2.wireOp",EDGE,"E104.0.2")}),-1.0]])]});
            var Q12;
            Q12=makeQuery(id+"F2.imprint","IMPRINT",FACE,{"disambiguationData":[TD([[makeQuery(id+"F2.imprint","IMPRINT",EDGE,{"derivedFrom":sQuery(id+"F2.wireOp",EDGE,"E103.0.2")}),-1.0]])]});
            var Q13;
            Q13=makeQuery(id+"F2.imprint","IMPRINT",FACE,{"disambiguationData":[TD([[makeQuery(id+"F2.imprint","IMPRINT",EDGE,{"derivedFrom":sQuery(id+"F2.wireOp",EDGE,"E102.0.0")}),-1.0]])]});
            var Q14;
            Q14=makeQuery(id+"F2.imprint","IMPRINT",FACE,{"disambiguationData":[TD([[makeQuery(id+"F2.imprint","IMPRINT",EDGE,{"derivedFrom":sQuery(id+"F2.wireOp",EDGE,"E101.0.2")}),-1.0]])]});
            var Q15;
            Q15=makeQuery(id+"F2.imprint","IMPRINT",FACE,{"disambiguationData":[TD([[makeQuery(id+"F2.imprint","IMPRINT",EDGE,{"derivedFrom":sQuery(id+"F2.wireOp",EDGE,"E100.0.2")}),-1.0]])]});
            var Q16;
            Q16=makeQuery(id+"F2.imprint","IMPRINT",FACE,{"disambiguationData":[TD([[makeQuery(id+"F2.imprint","IMPRINT",EDGE,{"derivedFrom":sQuery(id+"F2.wireOp",EDGE,"E99.0.2")}),-1.0]])]});
            var Q17;
            Q17=makeQuery(id+"F2.imprint","IMPRINT",FACE,{"disambiguationData":[TD([[makeQuery(id+"F2.imprint","IMPRINT",EDGE,{"derivedFrom":sQuery(id+"F2.wireOp",EDGE,"E98.0.2")}),-1.0]])]});
            var Q18;
            Q18=makeQuery(id+"F2.imprint","IMPRINT",FACE,{"disambiguationData":[TD([[makeQuery(id+"F2.imprint","IMPRINT",EDGE,{"derivedFrom":sQuery(id+"F2.wireOp",EDGE,"E96.0.2")}),-1.0]])]});
            var Q19;
            Q19=makeQuery(id+"F2.imprint","IMPRINT",FACE,{"disambiguationData":[TD([[makeQuery(id+"F2.imprint","IMPRINT",EDGE,{"derivedFrom":sQuery(id+"F2.wireOp",EDGE,"E95.0.0")}),-1.0]])]});
            var Q20;
            Q20=makeQuery(id+"F2.imprint","IMPRINT",FACE,{"disambiguationData":[TD([[makeQuery(id+"F2.imprint","IMPRINT",EDGE,{"derivedFrom":sQuery(id+"F2.wireOp",EDGE,"E95.0.1")}),-1.0]])]});
            var Q21;
            Q21=makeQuery(id+"F2.imprint","IMPRINT",FACE,{"disambiguationData":[TD([[makeQuery(id+"F2.imprint","IMPRINT",EDGE,{"derivedFrom":sQuery(id+"F2.wireOp",EDGE,"E105.0.0")}),-1.0]])]});
            var Q22;
            Q22=makeQuery(id+"F2.imprint","IMPRINT",FACE,{"disambiguationData":[TD([[makeQuery(id+"F2.imprint","IMPRINT",EDGE,{"derivedFrom":sQuery(id+"F2.wireOp",EDGE,"E107.0.2")}),-1.0]])]});
            var Q23;
            Q23=makeQuery(id+"F2.imprint","IMPRINT",FACE,{"disambiguationData":[TD([[makeQuery(id+"F2.imprint","IMPRINT",EDGE,{"derivedFrom":sQuery(id+"F2.wireOp",EDGE,"E97.0.0")}),-1.0]])]});
            extrude(context, id + "F3", {"entities" : qUnion([Q0, Q1, Q2, Q3, Q4, Q5, Q6, Q7, Q8, Q9, Q10, Q11, Q12, Q13, Q14, Q15, Q16, Q17, Q18, Q19, Q20, Q21, Q22, Q23]), "depth" : 6 * mm, "hasDraft" : true, "draftAngle" : 3 * degree, "draftPullDirection" : true});
        }
        {
            var Q0;
            {var subQ0=sQuery(id+"F0.wireOp",EDGE,"E42");var subQ1=sQuery(id+"F0.wireOp",EDGE,"E17");var subQ2=makeQuery(id+"F0.imprint","INTERSECT",VERTEX,{"derivedFrom":[sQuery(id+"F0.wireOp",EDGE,"E7"),subQ1,subQ0]});Q0=makeQuery(id+"F0.imprint","IMPRINT",FACE,{"disambiguationData":[TD([[makeQuery(id+"F0.imprint","IMPRINT",EDGE,{"disambiguationData":[TD([[subQ2,1.0]])],"derivedFrom":subQ1}),-1.0]])]});}
            var Q1;
            {var subQ0=sQuery(id+"F0.wireOp",EDGE,"E28");var subQ1=sQuery(id+"F0.wireOp",EDGE,"E0");var subQ2=makeQuery(id+"F0.imprint","INTERSECT",VERTEX,{"derivedFrom":[subQ1,sQuery(id+"F0.wireOp",EDGE,"E26"),subQ0]});Q1=makeQuery(id+"F0.imprint","IMPRINT",FACE,{"disambiguationData":[TD([[makeQuery(id+"F0.imprint","IMPRINT",EDGE,{"disambiguationData":[TD([[subQ2,-1.0]])],"derivedFrom":subQ1}),1.0]])]});}
            var Q2;
            {var subQ0=sQuery(id+"F0.wireOp",EDGE,"E7");var subQ1=sQuery(id+"F0.wireOp",EDGE,"E0");var subQ2=makeQuery(id+"F0.imprint","INTERSECT",VERTEX,{"derivedFrom":[subQ1,sQuery(id+"F0.wireOp",EDGE,"E3"),subQ0]});Q2=makeQuery(id+"F0.imprint","IMPRINT",FACE,{"disambiguationData":[TD([[makeQuery(id+"F0.imprint","IMPRINT",EDGE,{"disambiguationData":[TD([[subQ2,-1.0]])],"derivedFrom":subQ1}),1.0]])]});}
            var Q3;
            {var subQ0=sQuery(id+"F0.wireOp",EDGE,"E42");var subQ1=sQuery(id+"F0.wireOp",EDGE,"E7");var subQ2=makeQuery(id+"F0.imprint","INTERSECT",VERTEX,{"derivedFrom":[subQ1,sQuery(id+"F0.wireOp",EDGE,"E17"),subQ0]});Q3=makeQuery(id+"F0.imprint","IMPRINT",FACE,{"disambiguationData":[TD([[makeQuery(id+"F0.imprint","IMPRINT",EDGE,{"disambiguationData":[TD([[subQ2,-1.0]])],"derivedFrom":subQ1}),-1.0]])]});}
            var Q4;
            {var subQ0=sQuery(id+"F0.wireOp",EDGE,"E19");var subQ1=sQuery(id+"F0.wireOp",EDGE,"E0");var subQ2=makeQuery(id+"F0.imprint","INTERSECT",VERTEX,{"derivedFrom":[subQ1,sQuery(id+"F0.wireOp",EDGE,"E17"),subQ0]});Q4=makeQuery(id+"F0.imprint","IMPRINT",FACE,{"disambiguationData":[TD([[makeQuery(id+"F0.imprint","IMPRINT",EDGE,{"disambiguationData":[TD([[subQ2,-1.0]])],"derivedFrom":subQ1}),1.0]])]});}
            var Q5;
            {var subQ0=sQuery(id+"F0.wireOp",EDGE,"E13");var subQ1=sQuery(id+"F0.wireOp",EDGE,"E3");var subQ2=makeQuery(id+"F0.imprint","INTERSECT",VERTEX,{"derivedFrom":[subQ1,subQ0,sQuery(id+"F0.wireOp",EDGE,"E44")]});Q5=makeQuery(id+"F0.imprint","IMPRINT",FACE,{"disambiguationData":[TD([[makeQuery(id+"F0.imprint","IMPRINT",EDGE,{"disambiguationData":[TD([[subQ2,-1.0]])],"derivedFrom":subQ1}),-1.0]])]});}
            var Q6;
            {var subQ0=sQuery(id+"F0.wireOp",EDGE,"E42");var subQ1=sQuery(id+"F0.wireOp",EDGE,"E20");var subQ2=makeQuery(id+"F0.imprint","INTERSECT",VERTEX,{"derivedFrom":[sQuery(id+"F0.wireOp",EDGE,"E11"),subQ1,subQ0]});Q6=makeQuery(id+"F0.imprint","IMPRINT",FACE,{"disambiguationData":[TD([[makeQuery(id+"F0.imprint","IMPRINT",EDGE,{"disambiguationData":[TD([[subQ2,-1.0]])],"derivedFrom":subQ1}),-1.0]])]});}
            var Q7;
            {var subQ0=sQuery(id+"F0.wireOp",EDGE,"E42");var subQ1=sQuery(id+"F0.wireOp",EDGE,"E8");var subQ2=makeQuery(id+"F0.imprint","INTERSECT",VERTEX,{"derivedFrom":[subQ1,sQuery(id+"F0.wireOp",EDGE,"E18"),subQ0]});Q7=makeQuery(id+"F0.imprint","IMPRINT",FACE,{"disambiguationData":[TD([[makeQuery(id+"F0.imprint","IMPRINT",EDGE,{"disambiguationData":[TD([[subQ2,-1.0]])],"derivedFrom":subQ1}),-1.0]])]});}
            var Q8;
            {var subQ0=sQuery(id+"F0.wireOp",EDGE,"E42");var subQ1=sQuery(id+"F0.wireOp",EDGE,"E18");var subQ2=makeQuery(id+"F0.imprint","INTERSECT",VERTEX,{"derivedFrom":[sQuery(id+"F0.wireOp",EDGE,"E8"),subQ1,subQ0]});Q8=makeQuery(id+"F0.imprint","IMPRINT",FACE,{"disambiguationData":[TD([[makeQuery(id+"F0.imprint","IMPRINT",EDGE,{"disambiguationData":[TD([[subQ2,1.0]])],"derivedFrom":subQ1}),-1.0]])]});}
            var Q9;
            {var subQ0=sQuery(id+"F0.wireOp",EDGE,"E14");var subQ1=sQuery(id+"F0.wireOp",EDGE,"E5");var subQ2=makeQuery(id+"F0.imprint","INTERSECT",VERTEX,{"derivedFrom":[subQ1,subQ0,sQuery(id+"F0.wireOp",EDGE,"E44")]});Q9=makeQuery(id+"F0.imprint","IMPRINT",FACE,{"disambiguationData":[TD([[makeQuery(id+"F0.imprint","IMPRINT",EDGE,{"disambiguationData":[TD([[subQ2,-1.0]])],"derivedFrom":subQ1}),-1.0]])]});}
            var Q10;
            {var subQ0=sQuery(id+"F0.wireOp",EDGE,"E42");var subQ1=sQuery(id+"F0.wireOp",EDGE,"E21");var subQ2=makeQuery(id+"F0.imprint","INTERSECT",VERTEX,{"derivedFrom":[sQuery(id+"F0.wireOp",EDGE,"E12"),subQ1,subQ0]});Q10=makeQuery(id+"F0.imprint","IMPRINT",FACE,{"disambiguationData":[TD([[makeQuery(id+"F0.imprint","IMPRINT",EDGE,{"disambiguationData":[TD([[subQ2,-1.0]])],"derivedFrom":subQ1}),-1.0]])]});}
            var Q11;
            {var subQ0=sQuery(id+"F0.wireOp",EDGE,"E42");var subQ1=sQuery(id+"F0.wireOp",EDGE,"E6");var subQ2=makeQuery(id+"F0.imprint","INTERSECT",VERTEX,{"derivedFrom":[subQ1,sQuery(id+"F0.wireOp",EDGE,"E19"),subQ0]});Q11=makeQuery(id+"F0.imprint","IMPRINT",FACE,{"disambiguationData":[TD([[makeQuery(id+"F0.imprint","IMPRINT",EDGE,{"disambiguationData":[TD([[subQ2,-1.0]])],"derivedFrom":subQ1}),-1.0]])]});}
            var Q12;
            {var subQ0=sQuery(id+"F0.wireOp",EDGE,"E42");var subQ1=sQuery(id+"F0.wireOp",EDGE,"E19");var subQ2=makeQuery(id+"F0.imprint","INTERSECT",VERTEX,{"derivedFrom":[sQuery(id+"F0.wireOp",EDGE,"E6"),subQ1,subQ0]});Q12=makeQuery(id+"F0.imprint","IMPRINT",FACE,{"disambiguationData":[TD([[makeQuery(id+"F0.imprint","IMPRINT",EDGE,{"disambiguationData":[TD([[subQ2,1.0]])],"derivedFrom":subQ1}),-1.0]])]});}
            var Q13;
            {var subQ0=sQuery(id+"F0.wireOp",EDGE,"E42");var subQ1=sQuery(id+"F0.wireOp",EDGE,"E22");var subQ2=makeQuery(id+"F0.imprint","INTERSECT",VERTEX,{"derivedFrom":[sQuery(id+"F0.wireOp",EDGE,"E13"),subQ1,subQ0]});Q13=makeQuery(id+"F0.imprint","IMPRINT",FACE,{"disambiguationData":[TD([[makeQuery(id+"F0.imprint","IMPRINT",EDGE,{"disambiguationData":[TD([[subQ2,-1.0]])],"derivedFrom":subQ1}),-1.0]])]});}
            var Q14;
            {var subQ0=sQuery(id+"F0.wireOp",EDGE,"E42");var subQ1=sQuery(id+"F0.wireOp",EDGE,"E4");var subQ2=makeQuery(id+"F0.imprint","INTERSECT",VERTEX,{"derivedFrom":[subQ1,sQuery(id+"F0.wireOp",EDGE,"E20"),subQ0]});Q14=makeQuery(id+"F0.imprint","IMPRINT",FACE,{"disambiguationData":[TD([[makeQuery(id+"F0.imprint","IMPRINT",EDGE,{"disambiguationData":[TD([[subQ2,-1.0]])],"derivedFrom":subQ1}),-1.0]])]});}
            var Q15;
            {var subQ0=sQuery(id+"F0.wireOp",EDGE,"E15");var subQ1=sQuery(id+"F0.wireOp",EDGE,"E7");var subQ2=makeQuery(id+"F0.imprint","INTERSECT",VERTEX,{"derivedFrom":[subQ1,subQ0,sQuery(id+"F0.wireOp",EDGE,"E44")]});Q15=makeQuery(id+"F0.imprint","IMPRINT",FACE,{"disambiguationData":[TD([[makeQuery(id+"F0.imprint","IMPRINT",EDGE,{"disambiguationData":[TD([[subQ2,-1.0]])],"derivedFrom":subQ1}),-1.0]])]});}
            var Q16;
            {var subQ0=sQuery(id+"F0.wireOp",EDGE,"E42");var subQ1=sQuery(id+"F0.wireOp",EDGE,"E20");var subQ2=makeQuery(id+"F0.imprint","INTERSECT",VERTEX,{"derivedFrom":[sQuery(id+"F0.wireOp",EDGE,"E4"),subQ1,subQ0]});Q16=makeQuery(id+"F0.imprint","IMPRINT",FACE,{"disambiguationData":[TD([[makeQuery(id+"F0.imprint","IMPRINT",EDGE,{"disambiguationData":[TD([[subQ2,1.0]])],"derivedFrom":subQ1}),-1.0]])]});}
            var Q17;
            {var subQ0=sQuery(id+"F0.wireOp",EDGE,"E10");var subQ1=sQuery(id+"F0.wireOp",EDGE,"E8");var subQ2=makeQuery(id+"F0.imprint","INTERSECT",VERTEX,{"derivedFrom":[subQ1,subQ0,sQuery(id+"F0.wireOp",EDGE,"E44")]});Q17=makeQuery(id+"F0.imprint","IMPRINT",FACE,{"disambiguationData":[TD([[makeQuery(id+"F0.imprint","IMPRINT",EDGE,{"disambiguationData":[TD([[subQ2,-1.0]])],"derivedFrom":subQ1}),-1.0]])]});}
            var Q18;
            {var subQ0=sQuery(id+"F0.wireOp",EDGE,"E42");var subQ1=sQuery(id+"F0.wireOp",EDGE,"E3");var subQ2=makeQuery(id+"F0.imprint","INTERSECT",VERTEX,{"derivedFrom":[subQ1,sQuery(id+"F0.wireOp",EDGE,"E21"),subQ0]});Q18=makeQuery(id+"F0.imprint","IMPRINT",FACE,{"disambiguationData":[TD([[makeQuery(id+"F0.imprint","IMPRINT",EDGE,{"disambiguationData":[TD([[subQ2,-1.0]])],"derivedFrom":subQ1}),-1.0]])]});}
            var Q19;
            {var subQ0=sQuery(id+"F0.wireOp",EDGE,"E42");var subQ1=sQuery(id+"F0.wireOp",EDGE,"E21");var subQ2=makeQuery(id+"F0.imprint","INTERSECT",VERTEX,{"derivedFrom":[sQuery(id+"F0.wireOp",EDGE,"E3"),subQ1,subQ0]});Q19=makeQuery(id+"F0.imprint","IMPRINT",FACE,{"disambiguationData":[TD([[makeQuery(id+"F0.imprint","IMPRINT",EDGE,{"disambiguationData":[TD([[subQ2,1.0]])],"derivedFrom":subQ1}),-1.0]])]});}
            var Q20;
            {var subQ0=sQuery(id+"F0.wireOp",EDGE,"E11");var subQ1=sQuery(id+"F0.wireOp",EDGE,"E6");var subQ2=makeQuery(id+"F0.imprint","INTERSECT",VERTEX,{"derivedFrom":[subQ1,subQ0,sQuery(id+"F0.wireOp",EDGE,"E44")]});Q20=makeQuery(id+"F0.imprint","IMPRINT",FACE,{"disambiguationData":[TD([[makeQuery(id+"F0.imprint","IMPRINT",EDGE,{"disambiguationData":[TD([[subQ2,-1.0]])],"derivedFrom":subQ1}),-1.0]])]});}
            var Q21;
            {var subQ0=sQuery(id+"F0.wireOp",EDGE,"E42");var subQ1=sQuery(id+"F0.wireOp",EDGE,"E18");var subQ2=makeQuery(id+"F0.imprint","INTERSECT",VERTEX,{"derivedFrom":[sQuery(id+"F0.wireOp",EDGE,"E15"),subQ1,subQ0]});Q21=makeQuery(id+"F0.imprint","IMPRINT",FACE,{"disambiguationData":[TD([[makeQuery(id+"F0.imprint","IMPRINT",EDGE,{"disambiguationData":[TD([[subQ2,-1.0]])],"derivedFrom":subQ1}),-1.0]])]});}
            var Q22;
            {var subQ0=sQuery(id+"F0.wireOp",EDGE,"E42");var subQ1=sQuery(id+"F0.wireOp",EDGE,"E5");var subQ2=makeQuery(id+"F0.imprint","INTERSECT",VERTEX,{"derivedFrom":[subQ1,sQuery(id+"F0.wireOp",EDGE,"E22"),subQ0]});Q22=makeQuery(id+"F0.imprint","IMPRINT",FACE,{"disambiguationData":[TD([[makeQuery(id+"F0.imprint","IMPRINT",EDGE,{"disambiguationData":[TD([[subQ2,-1.0]])],"derivedFrom":subQ1}),-1.0]])]});}
            var Q23;
            {var subQ0=sQuery(id+"F0.wireOp",EDGE,"E42");var subQ1=sQuery(id+"F0.wireOp",EDGE,"E22");var subQ2=makeQuery(id+"F0.imprint","INTERSECT",VERTEX,{"derivedFrom":[sQuery(id+"F0.wireOp",EDGE,"E5"),subQ1,subQ0]});Q23=makeQuery(id+"F0.imprint","IMPRINT",FACE,{"disambiguationData":[TD([[makeQuery(id+"F0.imprint","IMPRINT",EDGE,{"disambiguationData":[TD([[subQ2,1.0]])],"derivedFrom":subQ1}),-1.0]])]});}
            var Q24;
            {var subQ0=sQuery(id+"F0.wireOp",EDGE,"E12");var subQ1=sQuery(id+"F0.wireOp",EDGE,"E4");var subQ2=makeQuery(id+"F0.imprint","INTERSECT",VERTEX,{"derivedFrom":[subQ1,subQ0,sQuery(id+"F0.wireOp",EDGE,"E44")]});Q24=makeQuery(id+"F0.imprint","IMPRINT",FACE,{"disambiguationData":[TD([[makeQuery(id+"F0.imprint","IMPRINT",EDGE,{"disambiguationData":[TD([[subQ2,-1.0]])],"derivedFrom":subQ1}),-1.0]])]});}
            var Q25;
            {var subQ0=sQuery(id+"F0.wireOp",EDGE,"E42");var subQ1=sQuery(id+"F0.wireOp",EDGE,"E19");var subQ2=makeQuery(id+"F0.imprint","INTERSECT",VERTEX,{"derivedFrom":[sQuery(id+"F0.wireOp",EDGE,"E10"),subQ1,subQ0]});Q25=makeQuery(id+"F0.imprint","IMPRINT",FACE,{"disambiguationData":[TD([[makeQuery(id+"F0.imprint","IMPRINT",EDGE,{"disambiguationData":[TD([[subQ2,-1.0]])],"derivedFrom":subQ1}),-1.0]])]});}
            var Q26;
            {var subQ0=sQuery(id+"F0.wireOp",EDGE,"E13");var subQ1=sQuery(id+"F0.wireOp",EDGE,"E0");var subQ2=makeQuery(id+"F0.imprint","INTERSECT",VERTEX,{"derivedFrom":[subQ1,sQuery(id+"F0.wireOp",EDGE,"E11"),subQ0]});Q26=makeQuery(id+"F0.imprint","IMPRINT",FACE,{"disambiguationData":[TD([[makeQuery(id+"F0.imprint","IMPRINT",EDGE,{"disambiguationData":[TD([[subQ2,-1.0]])],"derivedFrom":subQ1}),1.0]])]});}
            var Q27;
            {var subQ0=sQuery(id+"F0.wireOp",EDGE,"E20");var subQ1=sQuery(id+"F0.wireOp",EDGE,"E0");var subQ2=makeQuery(id+"F0.imprint","INTERSECT",VERTEX,{"derivedFrom":[subQ1,sQuery(id+"F0.wireOp",EDGE,"E18"),subQ0]});Q27=makeQuery(id+"F0.imprint","IMPRINT",FACE,{"disambiguationData":[TD([[makeQuery(id+"F0.imprint","IMPRINT",EDGE,{"disambiguationData":[TD([[subQ2,-1.0]])],"derivedFrom":subQ1}),1.0]])]});}
            var Q28;
            {var subQ0=sQuery(id+"F0.wireOp",EDGE,"E8");var subQ1=sQuery(id+"F0.wireOp",EDGE,"E0");var subQ2=makeQuery(id+"F0.imprint","INTERSECT",VERTEX,{"derivedFrom":[subQ1,sQuery(id+"F0.wireOp",EDGE,"E5"),subQ0]});Q28=makeQuery(id+"F0.imprint","IMPRINT",FACE,{"disambiguationData":[TD([[makeQuery(id+"F0.imprint","IMPRINT",EDGE,{"disambiguationData":[TD([[subQ2,-1.0]])],"derivedFrom":subQ1}),1.0]])]});}
            var Q29;
            {var subQ0=sQuery(id+"F0.wireOp",EDGE,"E29");var subQ1=sQuery(id+"F0.wireOp",EDGE,"E0");var subQ2=makeQuery(id+"F0.imprint","INTERSECT",VERTEX,{"derivedFrom":[subQ1,sQuery(id+"F0.wireOp",EDGE,"E27"),subQ0]});Q29=makeQuery(id+"F0.imprint","IMPRINT",FACE,{"disambiguationData":[TD([[makeQuery(id+"F0.imprint","IMPRINT",EDGE,{"disambiguationData":[TD([[subQ2,-1.0]])],"derivedFrom":subQ1}),1.0]])]});}
            var Q30;
            {var subQ0=sQuery(id+"F0.wireOp",EDGE,"E14");var subQ1=sQuery(id+"F0.wireOp",EDGE,"E0");var subQ2=makeQuery(id+"F0.imprint","INTERSECT",VERTEX,{"derivedFrom":[subQ1,sQuery(id+"F0.wireOp",EDGE,"E12"),subQ0]});Q30=makeQuery(id+"F0.imprint","IMPRINT",FACE,{"disambiguationData":[TD([[makeQuery(id+"F0.imprint","IMPRINT",EDGE,{"disambiguationData":[TD([[subQ2,-1.0]])],"derivedFrom":subQ1}),1.0]])]});}
            var Q31;
            {var subQ0=sQuery(id+"F0.wireOp",EDGE,"E21");var subQ1=sQuery(id+"F0.wireOp",EDGE,"E0");var subQ2=makeQuery(id+"F0.imprint","INTERSECT",VERTEX,{"derivedFrom":[subQ1,sQuery(id+"F0.wireOp",EDGE,"E19"),subQ0]});Q31=makeQuery(id+"F0.imprint","IMPRINT",FACE,{"disambiguationData":[TD([[makeQuery(id+"F0.imprint","IMPRINT",EDGE,{"disambiguationData":[TD([[subQ2,-1.0]])],"derivedFrom":subQ1}),1.0]])]});}
            var Q32;
            {var subQ0=sQuery(id+"F0.wireOp",EDGE,"E6");var subQ1=sQuery(id+"F0.wireOp",EDGE,"E0");var subQ2=makeQuery(id+"F0.imprint","INTERSECT",VERTEX,{"derivedFrom":[subQ1,subQ0,sQuery(id+"F0.wireOp",EDGE,"E7")]});Q32=makeQuery(id+"F0.imprint","IMPRINT",FACE,{"disambiguationData":[TD([[makeQuery(id+"F0.imprint","IMPRINT",EDGE,{"disambiguationData":[TD([[subQ2,-1.0]])],"derivedFrom":subQ1}),1.0]])]});}
            var Q33;
            {var subQ0=sQuery(id+"F0.wireOp",EDGE,"E24");var subQ1=sQuery(id+"F0.wireOp",EDGE,"E0");var subQ2=makeQuery(id+"F0.imprint","INTERSECT",VERTEX,{"derivedFrom":[subQ1,subQ0,sQuery(id+"F0.wireOp",EDGE,"E28")]});Q33=makeQuery(id+"F0.imprint","IMPRINT",FACE,{"disambiguationData":[TD([[makeQuery(id+"F0.imprint","IMPRINT",EDGE,{"disambiguationData":[TD([[subQ2,-1.0]])],"derivedFrom":subQ1}),1.0]])]});}
            var Q34;
            {var subQ0=sQuery(id+"F0.wireOp",EDGE,"E15");var subQ1=sQuery(id+"F0.wireOp",EDGE,"E0");var subQ2=makeQuery(id+"F0.imprint","INTERSECT",VERTEX,{"derivedFrom":[subQ1,sQuery(id+"F0.wireOp",EDGE,"E13"),subQ0]});Q34=makeQuery(id+"F0.imprint","IMPRINT",FACE,{"disambiguationData":[TD([[makeQuery(id+"F0.imprint","IMPRINT",EDGE,{"disambiguationData":[TD([[subQ2,-1.0]])],"derivedFrom":subQ1}),1.0]])]});}
            var Q35;
            {var subQ0=sQuery(id+"F0.wireOp",EDGE,"E22");var subQ1=sQuery(id+"F0.wireOp",EDGE,"E0");var subQ2=makeQuery(id+"F0.imprint","INTERSECT",VERTEX,{"derivedFrom":[subQ1,sQuery(id+"F0.wireOp",EDGE,"E20"),subQ0]});Q35=makeQuery(id+"F0.imprint","IMPRINT",FACE,{"disambiguationData":[TD([[makeQuery(id+"F0.imprint","IMPRINT",EDGE,{"disambiguationData":[TD([[subQ2,-1.0]])],"derivedFrom":subQ1}),1.0]])]});}
            var Q36;
            {var subQ0=sQuery(id+"F0.wireOp",EDGE,"E4");var subQ1=sQuery(id+"F0.wireOp",EDGE,"E0");var subQ2=makeQuery(id+"F0.imprint","INTERSECT",VERTEX,{"derivedFrom":[subQ1,subQ0,sQuery(id+"F0.wireOp",EDGE,"E8")]});Q36=makeQuery(id+"F0.imprint","IMPRINT",FACE,{"disambiguationData":[TD([[makeQuery(id+"F0.imprint","IMPRINT",EDGE,{"disambiguationData":[TD([[subQ2,-1.0]])],"derivedFrom":subQ1}),1.0]])]});}
            var Q37;
            {var subQ0=sQuery(id+"F0.wireOp",EDGE,"E25");var subQ1=sQuery(id+"F0.wireOp",EDGE,"E0");var subQ2=makeQuery(id+"F0.imprint","INTERSECT",VERTEX,{"derivedFrom":[subQ1,subQ0,sQuery(id+"F0.wireOp",EDGE,"E29")]});Q37=makeQuery(id+"F0.imprint","IMPRINT",FACE,{"disambiguationData":[TD([[makeQuery(id+"F0.imprint","IMPRINT",EDGE,{"disambiguationData":[TD([[subQ2,-1.0]])],"derivedFrom":subQ1}),1.0]])]});}
            var Q38;
            {var subQ0=sQuery(id+"F0.wireOp",EDGE,"E26");var subQ1=sQuery(id+"F0.wireOp",EDGE,"E0");var subQ2=makeQuery(id+"F0.imprint","INTERSECT",VERTEX,{"derivedFrom":[subQ1,sQuery(id+"F0.wireOp",EDGE,"E24"),subQ0]});Q38=makeQuery(id+"F0.imprint","IMPRINT",FACE,{"disambiguationData":[TD([[makeQuery(id+"F0.imprint","IMPRINT",EDGE,{"disambiguationData":[TD([[subQ2,-1.0]])],"derivedFrom":subQ1}),1.0]])]});}
            var Q39;
            {var subQ0=sQuery(id+"F0.wireOp",EDGE,"E18");var subQ1=sQuery(id+"F0.wireOp",EDGE,"E0");var subQ2=makeQuery(id+"F0.imprint","INTERSECT",VERTEX,{"derivedFrom":[subQ1,subQ0,sQuery(id+"F0.wireOp",EDGE,"E22")]});Q39=makeQuery(id+"F0.imprint","IMPRINT",FACE,{"disambiguationData":[TD([[makeQuery(id+"F0.imprint","IMPRINT",EDGE,{"disambiguationData":[TD([[subQ2,-1.0]])],"derivedFrom":subQ1}),1.0]])]});}
            var Q40;
            {var subQ0=sQuery(id+"F0.wireOp",EDGE,"E11");var subQ1=sQuery(id+"F0.wireOp",EDGE,"E0");var subQ2=makeQuery(id+"F0.imprint","INTERSECT",VERTEX,{"derivedFrom":[subQ1,subQ0,sQuery(id+"F0.wireOp",EDGE,"E15")]});Q40=makeQuery(id+"F0.imprint","IMPRINT",FACE,{"disambiguationData":[TD([[makeQuery(id+"F0.imprint","IMPRINT",EDGE,{"disambiguationData":[TD([[subQ2,-1.0]])],"derivedFrom":subQ1}),1.0]])]});}
            var Q41;
            {var subQ0=sQuery(id+"F0.wireOp",EDGE,"E4");var subQ1=sQuery(id+"F0.wireOp",EDGE,"E0");var subQ2=makeQuery(id+"F0.imprint","INTERSECT",VERTEX,{"derivedFrom":[subQ1,subQ0,sQuery(id+"F0.wireOp",EDGE,"E5")]});Q41=makeQuery(id+"F0.imprint","IMPRINT",FACE,{"disambiguationData":[TD([[makeQuery(id+"F0.imprint","IMPRINT",EDGE,{"disambiguationData":[TD([[subQ2,1.0]])],"derivedFrom":subQ1}),1.0]])]});}
            var Q42;
            {var subQ0=sQuery(id+"F0.wireOp",EDGE,"E22");var subQ1=sQuery(id+"F0.wireOp",EDGE,"E0");var subQ2=makeQuery(id+"F0.imprint","INTERSECT",VERTEX,{"derivedFrom":[subQ1,sQuery(id+"F0.wireOp",EDGE,"E18"),subQ0]});Q42=makeQuery(id+"F0.imprint","IMPRINT",FACE,{"disambiguationData":[TD([[makeQuery(id+"F0.imprint","IMPRINT",EDGE,{"disambiguationData":[TD([[subQ2,1.0]])],"derivedFrom":subQ1}),1.0]])]});}
            var Q43;
            {var subQ0=sQuery(id+"F0.wireOp",EDGE,"E12");var subQ1=sQuery(id+"F0.wireOp",EDGE,"E0");var subQ2=makeQuery(id+"F0.imprint","INTERSECT",VERTEX,{"derivedFrom":[subQ1,sQuery(id+"F0.wireOp",EDGE,"E10"),subQ0]});Q43=makeQuery(id+"F0.imprint","IMPRINT",FACE,{"disambiguationData":[TD([[makeQuery(id+"F0.imprint","IMPRINT",EDGE,{"disambiguationData":[TD([[subQ2,-1.0]])],"derivedFrom":subQ1}),1.0]])]});}
            var Q44;
            {var subQ0=sQuery(id+"F0.wireOp",EDGE,"E3");var subQ1=sQuery(id+"F0.wireOp",EDGE,"E0");var subQ2=makeQuery(id+"F0.imprint","INTERSECT",VERTEX,{"derivedFrom":[subQ1,subQ0,sQuery(id+"F0.wireOp",EDGE,"E6")]});Q44=makeQuery(id+"F0.imprint","IMPRINT",FACE,{"disambiguationData":[TD([[makeQuery(id+"F0.imprint","IMPRINT",EDGE,{"disambiguationData":[TD([[subQ2,-1.0]])],"derivedFrom":subQ1}),1.0]])]});}
            var Q45;
            {var subQ0=sQuery(id+"F0.wireOp",EDGE,"E10");var subQ1=sQuery(id+"F0.wireOp",EDGE,"E0");var subQ2=makeQuery(id+"F0.imprint","INTERSECT",VERTEX,{"derivedFrom":[subQ1,subQ0,sQuery(id+"F0.wireOp",EDGE,"E14")]});Q45=makeQuery(id+"F0.imprint","IMPRINT",FACE,{"disambiguationData":[TD([[makeQuery(id+"F0.imprint","IMPRINT",EDGE,{"disambiguationData":[TD([[subQ2,-1.0]])],"derivedFrom":subQ1}),1.0]])]});}
            var Q46;
            {var subQ0=sQuery(id+"F0.wireOp",EDGE,"E17");var subQ1=sQuery(id+"F0.wireOp",EDGE,"E0");var subQ2=makeQuery(id+"F0.imprint","INTERSECT",VERTEX,{"derivedFrom":[subQ1,subQ0,sQuery(id+"F0.wireOp",EDGE,"E21")]});Q46=makeQuery(id+"F0.imprint","IMPRINT",FACE,{"disambiguationData":[TD([[makeQuery(id+"F0.imprint","IMPRINT",EDGE,{"disambiguationData":[TD([[subQ2,-1.0]])],"derivedFrom":subQ1}),1.0]])]});}
            var Q47;
            {var subQ0=sQuery(id+"F0.wireOp",EDGE,"E42");var subQ1=sQuery(id+"F0.wireOp",EDGE,"E17");var subQ2=makeQuery(id+"F0.imprint","INTERSECT",VERTEX,{"derivedFrom":[sQuery(id+"F0.wireOp",EDGE,"E14"),subQ1,subQ0]});Q47=makeQuery(id+"F0.imprint","IMPRINT",FACE,{"disambiguationData":[TD([[makeQuery(id+"F0.imprint","IMPRINT",EDGE,{"disambiguationData":[TD([[subQ2,-1.0]])],"derivedFrom":subQ1}),-1.0]])]});}
            extrude(context, id + "F4", {"entities" : qUnion([Q0, Q1, Q2, Q3, Q4, Q5, Q6, Q7, Q8, Q9, Q10, Q11, Q12, Q13, Q14, Q15, Q16, Q17, Q18, Q19, Q20, Q21, Q22, Q23, Q24, Q25, Q26, Q27, Q28, Q29, Q30, Q31, Q32, Q33, Q34, Q35, Q36, Q37, Q38, Q39, Q40, Q41, Q42, Q43, Q44, Q45, Q46, Q47]), "depth" : 6 * mm, "hasDraft" : true, "draftAngle" : 5 * degree, "draftPullDirection" : true});
        }
        {
            var Q0;
            {var subQ0=sQuery(id+"F0.wireOp",EDGE,"E20");var subQ1=sQuery(id+"F0.wireOp",EDGE,"E18");var subQ2=makeQuery(id+"F0.imprint","INTERSECT",VERTEX,{"derivedFrom":[sQuery(id+"F0.wireOp",EDGE,"E0"),subQ1,subQ0]});Q0=makeQuery(id+"F0.imprint","IMPRINT",FACE,{"disambiguationData":[TD([[makeQuery(id+"F0.imprint","IMPRINT",EDGE,{"disambiguationData":[TD([[subQ2,-1.0]])],"derivedFrom":subQ1}),-1.0]])]});}
            var Q1;
            {var subQ0=sQuery(id+"F0.wireOp",EDGE,"E13");var subQ1=sQuery(id+"F0.wireOp",EDGE,"E11");var subQ2=makeQuery(id+"F0.imprint","INTERSECT",VERTEX,{"derivedFrom":[sQuery(id+"F0.wireOp",EDGE,"E0"),subQ1,subQ0]});Q1=makeQuery(id+"F0.imprint","IMPRINT",FACE,{"disambiguationData":[TD([[makeQuery(id+"F0.imprint","IMPRINT",EDGE,{"disambiguationData":[TD([[subQ2,-1.0]])],"derivedFrom":subQ1}),-1.0]])]});}
            var Q2;
            {var subQ0=sQuery(id+"F0.wireOp",EDGE,"E28");var subQ1=sQuery(id+"F0.wireOp",EDGE,"E26");var subQ2=makeQuery(id+"F0.imprint","INTERSECT",VERTEX,{"derivedFrom":[sQuery(id+"F0.wireOp",EDGE,"E0"),subQ1,subQ0]});Q2=makeQuery(id+"F0.imprint","IMPRINT",FACE,{"disambiguationData":[TD([[makeQuery(id+"F0.imprint","IMPRINT",EDGE,{"disambiguationData":[TD([[subQ2,-1.0]])],"derivedFrom":subQ1}),-1.0]])]});}
            var Q3;
            {var subQ0=sQuery(id+"F0.wireOp",EDGE,"E7");var subQ1=sQuery(id+"F0.wireOp",EDGE,"E3");var subQ2=makeQuery(id+"F0.imprint","INTERSECT",VERTEX,{"derivedFrom":[sQuery(id+"F0.wireOp",EDGE,"E0"),subQ1,subQ0]});Q3=makeQuery(id+"F0.imprint","IMPRINT",FACE,{"disambiguationData":[TD([[makeQuery(id+"F0.imprint","IMPRINT",EDGE,{"disambiguationData":[TD([[subQ2,-1.0]])],"derivedFrom":subQ1}),-1.0]])]});}
            var Q4;
            {var subQ0=sQuery(id+"F0.wireOp",EDGE,"E19");var subQ1=sQuery(id+"F0.wireOp",EDGE,"E17");var subQ2=makeQuery(id+"F0.imprint","INTERSECT",VERTEX,{"derivedFrom":[sQuery(id+"F0.wireOp",EDGE,"E0"),subQ1,subQ0]});Q4=makeQuery(id+"F0.imprint","IMPRINT",FACE,{"disambiguationData":[TD([[makeQuery(id+"F0.imprint","IMPRINT",EDGE,{"disambiguationData":[TD([[subQ2,-1.0]])],"derivedFrom":subQ1}),-1.0]])]});}
            var Q5;
            {var subQ0=sQuery(id+"F0.wireOp",EDGE,"E12");var subQ1=sQuery(id+"F0.wireOp",EDGE,"E10");var subQ2=makeQuery(id+"F0.imprint","INTERSECT",VERTEX,{"derivedFrom":[sQuery(id+"F0.wireOp",EDGE,"E0"),subQ1,subQ0]});Q5=makeQuery(id+"F0.imprint","IMPRINT",FACE,{"disambiguationData":[TD([[makeQuery(id+"F0.imprint","IMPRINT",EDGE,{"disambiguationData":[TD([[subQ2,-1.0]])],"derivedFrom":subQ1}),-1.0]])]});}
            var Q6;
            {var subQ0=sQuery(id+"F0.wireOp",EDGE,"E27");var subQ1=sQuery(id+"F0.wireOp",EDGE,"E25");var subQ2=makeQuery(id+"F0.imprint","INTERSECT",VERTEX,{"derivedFrom":[sQuery(id+"F0.wireOp",EDGE,"E0"),subQ1,subQ0]});Q6=makeQuery(id+"F0.imprint","IMPRINT",FACE,{"disambiguationData":[TD([[makeQuery(id+"F0.imprint","IMPRINT",EDGE,{"disambiguationData":[TD([[subQ2,-1.0]])],"derivedFrom":subQ1}),-1.0]])]});}
            var Q7;
            {var subQ0=sQuery(id+"F0.wireOp",EDGE,"E5");var subQ1=sQuery(id+"F0.wireOp",EDGE,"E4");var subQ2=makeQuery(id+"F0.imprint","INTERSECT",VERTEX,{"derivedFrom":[sQuery(id+"F0.wireOp",EDGE,"E0"),subQ1,subQ0]});Q7=makeQuery(id+"F0.imprint","IMPRINT",FACE,{"disambiguationData":[TD([[makeQuery(id+"F0.imprint","IMPRINT",EDGE,{"disambiguationData":[TD([[subQ2,-1.0]])],"derivedFrom":subQ1}),-1.0]])]});}
            var Q8;
            {var subQ0=sQuery(id+"F0.wireOp",EDGE,"E22");var subQ1=sQuery(id+"F0.wireOp",EDGE,"E18");var subQ2=makeQuery(id+"F0.imprint","INTERSECT",VERTEX,{"derivedFrom":[sQuery(id+"F0.wireOp",EDGE,"E0"),subQ1,subQ0]});Q8=makeQuery(id+"F0.imprint","IMPRINT",FACE,{"disambiguationData":[TD([[makeQuery(id+"F0.imprint","IMPRINT",EDGE,{"disambiguationData":[TD([[subQ2,1.0]])],"derivedFrom":subQ1}),-1.0]])]});}
            var Q9;
            {var subQ0=sQuery(id+"F0.wireOp",EDGE,"E15");var subQ1=sQuery(id+"F0.wireOp",EDGE,"E11");var subQ2=makeQuery(id+"F0.imprint","INTERSECT",VERTEX,{"derivedFrom":[sQuery(id+"F0.wireOp",EDGE,"E0"),subQ1,subQ0]});Q9=makeQuery(id+"F0.imprint","IMPRINT",FACE,{"disambiguationData":[TD([[makeQuery(id+"F0.imprint","IMPRINT",EDGE,{"disambiguationData":[TD([[subQ2,1.0]])],"derivedFrom":subQ1}),-1.0]])]});}
            var Q10;
            {var subQ0=sQuery(id+"F0.wireOp",EDGE,"E26");var subQ1=sQuery(id+"F0.wireOp",EDGE,"E24");var subQ2=makeQuery(id+"F0.imprint","INTERSECT",VERTEX,{"derivedFrom":[sQuery(id+"F0.wireOp",EDGE,"E0"),subQ1,subQ0]});Q10=makeQuery(id+"F0.imprint","IMPRINT",FACE,{"disambiguationData":[TD([[makeQuery(id+"F0.imprint","IMPRINT",EDGE,{"disambiguationData":[TD([[subQ2,-1.0]])],"derivedFrom":subQ1}),-1.0]])]});}
            var Q11;
            {var subQ0=sQuery(id+"F0.wireOp",EDGE,"E6");var subQ1=sQuery(id+"F0.wireOp",EDGE,"E3");var subQ2=makeQuery(id+"F0.imprint","INTERSECT",VERTEX,{"derivedFrom":[sQuery(id+"F0.wireOp",EDGE,"E0"),subQ1,subQ0]});Q11=makeQuery(id+"F0.imprint","IMPRINT",FACE,{"disambiguationData":[TD([[makeQuery(id+"F0.imprint","IMPRINT",EDGE,{"disambiguationData":[TD([[subQ2,1.0]])],"derivedFrom":subQ1}),-1.0]])]});}
            var Q12;
            {var subQ0=sQuery(id+"F0.wireOp",EDGE,"E21");var subQ1=sQuery(id+"F0.wireOp",EDGE,"E17");var subQ2=makeQuery(id+"F0.imprint","INTERSECT",VERTEX,{"derivedFrom":[sQuery(id+"F0.wireOp",EDGE,"E0"),subQ1,subQ0]});Q12=makeQuery(id+"F0.imprint","IMPRINT",FACE,{"disambiguationData":[TD([[makeQuery(id+"F0.imprint","IMPRINT",EDGE,{"disambiguationData":[TD([[subQ2,1.0]])],"derivedFrom":subQ1}),-1.0]])]});}
            var Q13;
            {var subQ0=sQuery(id+"F0.wireOp",EDGE,"E14");var subQ1=sQuery(id+"F0.wireOp",EDGE,"E10");var subQ2=makeQuery(id+"F0.imprint","INTERSECT",VERTEX,{"derivedFrom":[sQuery(id+"F0.wireOp",EDGE,"E0"),subQ1,subQ0]});Q13=makeQuery(id+"F0.imprint","IMPRINT",FACE,{"disambiguationData":[TD([[makeQuery(id+"F0.imprint","IMPRINT",EDGE,{"disambiguationData":[TD([[subQ2,1.0]])],"derivedFrom":subQ1}),-1.0]])]});}
            var Q14;
            {var subQ0=sQuery(id+"F0.wireOp",EDGE,"E29");var subQ1=sQuery(id+"F0.wireOp",EDGE,"E25");var subQ2=makeQuery(id+"F0.imprint","INTERSECT",VERTEX,{"derivedFrom":[sQuery(id+"F0.wireOp",EDGE,"E0"),subQ1,subQ0]});Q14=makeQuery(id+"F0.imprint","IMPRINT",FACE,{"disambiguationData":[TD([[makeQuery(id+"F0.imprint","IMPRINT",EDGE,{"disambiguationData":[TD([[subQ2,1.0]])],"derivedFrom":subQ1}),-1.0]])]});}
            var Q15;
            {var subQ0=sQuery(id+"F0.wireOp",EDGE,"E8");var subQ1=sQuery(id+"F0.wireOp",EDGE,"E4");var subQ2=makeQuery(id+"F0.imprint","INTERSECT",VERTEX,{"derivedFrom":[sQuery(id+"F0.wireOp",EDGE,"E0"),subQ1,subQ0]});Q15=makeQuery(id+"F0.imprint","IMPRINT",FACE,{"disambiguationData":[TD([[makeQuery(id+"F0.imprint","IMPRINT",EDGE,{"disambiguationData":[TD([[subQ2,1.0]])],"derivedFrom":subQ1}),-1.0]])]});}
            var Q16;
            {var subQ0=sQuery(id+"F0.wireOp",EDGE,"E22");var subQ1=sQuery(id+"F0.wireOp",EDGE,"E20");var subQ2=makeQuery(id+"F0.imprint","INTERSECT",VERTEX,{"derivedFrom":[sQuery(id+"F0.wireOp",EDGE,"E0"),subQ1,subQ0]});Q16=makeQuery(id+"F0.imprint","IMPRINT",FACE,{"disambiguationData":[TD([[makeQuery(id+"F0.imprint","IMPRINT",EDGE,{"disambiguationData":[TD([[subQ2,-1.0]])],"derivedFrom":subQ1}),-1.0]])]});}
            var Q17;
            {var subQ0=sQuery(id+"F0.wireOp",EDGE,"E15");var subQ1=sQuery(id+"F0.wireOp",EDGE,"E13");var subQ2=makeQuery(id+"F0.imprint","INTERSECT",VERTEX,{"derivedFrom":[sQuery(id+"F0.wireOp",EDGE,"E0"),subQ1,subQ0]});Q17=makeQuery(id+"F0.imprint","IMPRINT",FACE,{"disambiguationData":[TD([[makeQuery(id+"F0.imprint","IMPRINT",EDGE,{"disambiguationData":[TD([[subQ2,-1.0]])],"derivedFrom":subQ1}),-1.0]])]});}
            var Q18;
            {var subQ0=sQuery(id+"F0.wireOp",EDGE,"E28");var subQ1=sQuery(id+"F0.wireOp",EDGE,"E24");var subQ2=makeQuery(id+"F0.imprint","INTERSECT",VERTEX,{"derivedFrom":[sQuery(id+"F0.wireOp",EDGE,"E0"),subQ1,subQ0]});Q18=makeQuery(id+"F0.imprint","IMPRINT",FACE,{"disambiguationData":[TD([[makeQuery(id+"F0.imprint","IMPRINT",EDGE,{"disambiguationData":[TD([[subQ2,1.0]])],"derivedFrom":subQ1}),-1.0]])]});}
            var Q19;
            {var subQ0=sQuery(id+"F0.wireOp",EDGE,"E7");var subQ1=sQuery(id+"F0.wireOp",EDGE,"E6");var subQ2=makeQuery(id+"F0.imprint","INTERSECT",VERTEX,{"derivedFrom":[sQuery(id+"F0.wireOp",EDGE,"E0"),subQ1,subQ0]});Q19=makeQuery(id+"F0.imprint","IMPRINT",FACE,{"disambiguationData":[TD([[makeQuery(id+"F0.imprint","IMPRINT",EDGE,{"disambiguationData":[TD([[subQ2,1.0]])],"derivedFrom":subQ1}),-1.0]])]});}
            var Q20;
            {var subQ0=sQuery(id+"F0.wireOp",EDGE,"E21");var subQ1=sQuery(id+"F0.wireOp",EDGE,"E19");var subQ2=makeQuery(id+"F0.imprint","INTERSECT",VERTEX,{"derivedFrom":[sQuery(id+"F0.wireOp",EDGE,"E0"),subQ1,subQ0]});Q20=makeQuery(id+"F0.imprint","IMPRINT",FACE,{"disambiguationData":[TD([[makeQuery(id+"F0.imprint","IMPRINT",EDGE,{"disambiguationData":[TD([[subQ2,-1.0]])],"derivedFrom":subQ1}),-1.0]])]});}
            var Q21;
            {var subQ0=sQuery(id+"F0.wireOp",EDGE,"E14");var subQ1=sQuery(id+"F0.wireOp",EDGE,"E12");var subQ2=makeQuery(id+"F0.imprint","INTERSECT",VERTEX,{"derivedFrom":[sQuery(id+"F0.wireOp",EDGE,"E0"),subQ1,subQ0]});Q21=makeQuery(id+"F0.imprint","IMPRINT",FACE,{"disambiguationData":[TD([[makeQuery(id+"F0.imprint","IMPRINT",EDGE,{"disambiguationData":[TD([[subQ2,-1.0]])],"derivedFrom":subQ1}),-1.0]])]});}
            var Q22;
            {var subQ0=sQuery(id+"F0.wireOp",EDGE,"E29");var subQ1=sQuery(id+"F0.wireOp",EDGE,"E27");var subQ2=makeQuery(id+"F0.imprint","INTERSECT",VERTEX,{"derivedFrom":[sQuery(id+"F0.wireOp",EDGE,"E0"),subQ1,subQ0]});Q22=makeQuery(id+"F0.imprint","IMPRINT",FACE,{"disambiguationData":[TD([[makeQuery(id+"F0.imprint","IMPRINT",EDGE,{"disambiguationData":[TD([[subQ2,-1.0]])],"derivedFrom":subQ1}),-1.0]])]});}
            var Q23;
            {var subQ0=sQuery(id+"F0.wireOp",EDGE,"E8");var subQ1=sQuery(id+"F0.wireOp",EDGE,"E5");var subQ2=makeQuery(id+"F0.imprint","INTERSECT",VERTEX,{"derivedFrom":[sQuery(id+"F0.wireOp",EDGE,"E0"),subQ1,subQ0]});Q23=makeQuery(id+"F0.imprint","IMPRINT",FACE,{"disambiguationData":[TD([[makeQuery(id+"F0.imprint","IMPRINT",EDGE,{"disambiguationData":[TD([[subQ2,-1.0]])],"derivedFrom":subQ1}),-1.0]])]});}
            var Q24;
            {var subQ0=sQuery(id+"F0.wireOp",EDGE,"E22");var subQ1=sQuery(id+"F0.wireOp",EDGE,"E8");var subQ2=makeQuery(id+"F0.imprint","INTERSECT",VERTEX,{"derivedFrom":[subQ1,subQ0,sQuery(id+"F0.wireOp",EDGE,"E30")]});Q24=makeQuery(id+"F0.imprint","IMPRINT",FACE,{"disambiguationData":[TD([[makeQuery(id+"F0.imprint","IMPRINT",EDGE,{"disambiguationData":[TD([[subQ2,-1.0]])],"derivedFrom":subQ1}),-1.0]])]});}
            var Q25;
            {var subQ0=sQuery(id+"F0.wireOp",EDGE,"E32");var subQ1=sQuery(id+"F0.wireOp",EDGE,"E15");var subQ2=makeQuery(id+"F0.imprint","INTERSECT",VERTEX,{"derivedFrom":[sQuery(id+"F0.wireOp",EDGE,"E8"),subQ1,subQ0]});Q25=makeQuery(id+"F0.imprint","IMPRINT",FACE,{"disambiguationData":[TD([[makeQuery(id+"F0.imprint","IMPRINT",EDGE,{"disambiguationData":[TD([[subQ2,-1.0]])],"derivedFrom":subQ1}),-1.0]])]});}
            var Q26;
            {var subQ0=sQuery(id+"F0.wireOp",EDGE,"E32");var subQ1=sQuery(id+"F0.wireOp",EDGE,"E13");var subQ2=makeQuery(id+"F0.imprint","INTERSECT",VERTEX,{"derivedFrom":[sQuery(id+"F0.wireOp",EDGE,"E6"),subQ1,subQ0]});Q26=makeQuery(id+"F0.imprint","IMPRINT",FACE,{"disambiguationData":[TD([[makeQuery(id+"F0.imprint","IMPRINT",EDGE,{"disambiguationData":[TD([[subQ2,1.0]])],"derivedFrom":subQ1}),-1.0]])]});}
            var Q27;
            {var subQ0=sQuery(id+"F0.wireOp",EDGE,"E32");var subQ1=sQuery(id+"F0.wireOp",EDGE,"E6");var subQ2=makeQuery(id+"F0.imprint","INTERSECT",VERTEX,{"derivedFrom":[subQ1,sQuery(id+"F0.wireOp",EDGE,"E13"),subQ0]});Q27=makeQuery(id+"F0.imprint","IMPRINT",FACE,{"disambiguationData":[TD([[makeQuery(id+"F0.imprint","IMPRINT",EDGE,{"disambiguationData":[TD([[subQ2,-1.0]])],"derivedFrom":subQ1}),-1.0]])]});}
            var Q28;
            {var subQ0=sQuery(id+"F0.wireOp",EDGE,"E21");var subQ1=sQuery(id+"F0.wireOp",EDGE,"E7");var subQ2=makeQuery(id+"F0.imprint","INTERSECT",VERTEX,{"derivedFrom":[subQ1,subQ0,sQuery(id+"F0.wireOp",EDGE,"E30")]});Q28=makeQuery(id+"F0.imprint","IMPRINT",FACE,{"disambiguationData":[TD([[makeQuery(id+"F0.imprint","IMPRINT",EDGE,{"disambiguationData":[TD([[subQ2,-1.0]])],"derivedFrom":subQ1}),-1.0]])]});}
            var Q29;
            {var subQ0=sQuery(id+"F0.wireOp",EDGE,"E32");var subQ1=sQuery(id+"F0.wireOp",EDGE,"E14");var subQ2=makeQuery(id+"F0.imprint","INTERSECT",VERTEX,{"derivedFrom":[sQuery(id+"F0.wireOp",EDGE,"E7"),subQ1,subQ0]});Q29=makeQuery(id+"F0.imprint","IMPRINT",FACE,{"disambiguationData":[TD([[makeQuery(id+"F0.imprint","IMPRINT",EDGE,{"disambiguationData":[TD([[subQ2,-1.0]])],"derivedFrom":subQ1}),-1.0]])]});}
            var Q30;
            {var subQ0=sQuery(id+"F0.wireOp",EDGE,"E32");var subQ1=sQuery(id+"F0.wireOp",EDGE,"E12");var subQ2=makeQuery(id+"F0.imprint","INTERSECT",VERTEX,{"derivedFrom":[sQuery(id+"F0.wireOp",EDGE,"E8"),subQ1,subQ0]});Q30=makeQuery(id+"F0.imprint","IMPRINT",FACE,{"disambiguationData":[TD([[makeQuery(id+"F0.imprint","IMPRINT",EDGE,{"disambiguationData":[TD([[subQ2,1.0]])],"derivedFrom":subQ1}),-1.0]])]});}
            var Q31;
            {var subQ0=sQuery(id+"F0.wireOp",EDGE,"E32");var subQ1=sQuery(id+"F0.wireOp",EDGE,"E8");var subQ2=makeQuery(id+"F0.imprint","INTERSECT",VERTEX,{"derivedFrom":[subQ1,sQuery(id+"F0.wireOp",EDGE,"E12"),subQ0]});Q31=makeQuery(id+"F0.imprint","IMPRINT",FACE,{"disambiguationData":[TD([[makeQuery(id+"F0.imprint","IMPRINT",EDGE,{"disambiguationData":[TD([[subQ2,-1.0]])],"derivedFrom":subQ1}),-1.0]])]});}
            var Q32;
            {var subQ0=sQuery(id+"F0.wireOp",EDGE,"E20");var subQ1=sQuery(id+"F0.wireOp",EDGE,"E5");var subQ2=makeQuery(id+"F0.imprint","INTERSECT",VERTEX,{"derivedFrom":[subQ1,subQ0,sQuery(id+"F0.wireOp",EDGE,"E30")]});Q32=makeQuery(id+"F0.imprint","IMPRINT",FACE,{"disambiguationData":[TD([[makeQuery(id+"F0.imprint","IMPRINT",EDGE,{"disambiguationData":[TD([[subQ2,-1.0]])],"derivedFrom":subQ1}),-1.0]])]});}
            var Q33;
            {var subQ0=sQuery(id+"F0.wireOp",EDGE,"E32");var subQ1=sQuery(id+"F0.wireOp",EDGE,"E13");var subQ2=makeQuery(id+"F0.imprint","INTERSECT",VERTEX,{"derivedFrom":[sQuery(id+"F0.wireOp",EDGE,"E5"),subQ1,subQ0]});Q33=makeQuery(id+"F0.imprint","IMPRINT",FACE,{"disambiguationData":[TD([[makeQuery(id+"F0.imprint","IMPRINT",EDGE,{"disambiguationData":[TD([[subQ2,-1.0]])],"derivedFrom":subQ1}),-1.0]])]});}
            var Q34;
            {var subQ0=sQuery(id+"F0.wireOp",EDGE,"E32");var subQ1=sQuery(id+"F0.wireOp",EDGE,"E11");var subQ2=makeQuery(id+"F0.imprint","INTERSECT",VERTEX,{"derivedFrom":[sQuery(id+"F0.wireOp",EDGE,"E7"),subQ1,subQ0]});Q34=makeQuery(id+"F0.imprint","IMPRINT",FACE,{"disambiguationData":[TD([[makeQuery(id+"F0.imprint","IMPRINT",EDGE,{"disambiguationData":[TD([[subQ2,1.0]])],"derivedFrom":subQ1}),-1.0]])]});}
            var Q35;
            {var subQ0=sQuery(id+"F0.wireOp",EDGE,"E32");var subQ1=sQuery(id+"F0.wireOp",EDGE,"E7");var subQ2=makeQuery(id+"F0.imprint","INTERSECT",VERTEX,{"derivedFrom":[subQ1,sQuery(id+"F0.wireOp",EDGE,"E11"),subQ0]});Q35=makeQuery(id+"F0.imprint","IMPRINT",FACE,{"disambiguationData":[TD([[makeQuery(id+"F0.imprint","IMPRINT",EDGE,{"disambiguationData":[TD([[subQ2,-1.0]])],"derivedFrom":subQ1}),-1.0]])]});}
            var Q36;
            {var subQ0=sQuery(id+"F0.wireOp",EDGE,"E19");var subQ1=sQuery(id+"F0.wireOp",EDGE,"E3");var subQ2=makeQuery(id+"F0.imprint","INTERSECT",VERTEX,{"derivedFrom":[subQ1,subQ0,sQuery(id+"F0.wireOp",EDGE,"E30")]});Q36=makeQuery(id+"F0.imprint","IMPRINT",FACE,{"disambiguationData":[TD([[makeQuery(id+"F0.imprint","IMPRINT",EDGE,{"disambiguationData":[TD([[subQ2,-1.0]])],"derivedFrom":subQ1}),-1.0]])]});}
            var Q37;
            {var subQ0=sQuery(id+"F0.wireOp",EDGE,"E32");var subQ1=sQuery(id+"F0.wireOp",EDGE,"E12");var subQ2=makeQuery(id+"F0.imprint","INTERSECT",VERTEX,{"derivedFrom":[sQuery(id+"F0.wireOp",EDGE,"E3"),subQ1,subQ0]});Q37=makeQuery(id+"F0.imprint","IMPRINT",FACE,{"disambiguationData":[TD([[makeQuery(id+"F0.imprint","IMPRINT",EDGE,{"disambiguationData":[TD([[subQ2,-1.0]])],"derivedFrom":subQ1}),-1.0]])]});}
            var Q38;
            {var subQ0=sQuery(id+"F0.wireOp",EDGE,"E32");var subQ1=sQuery(id+"F0.wireOp",EDGE,"E10");var subQ2=makeQuery(id+"F0.imprint","INTERSECT",VERTEX,{"derivedFrom":[sQuery(id+"F0.wireOp",EDGE,"E5"),subQ1,subQ0]});Q38=makeQuery(id+"F0.imprint","IMPRINT",FACE,{"disambiguationData":[TD([[makeQuery(id+"F0.imprint","IMPRINT",EDGE,{"disambiguationData":[TD([[subQ2,1.0]])],"derivedFrom":subQ1}),-1.0]])]});}
            var Q39;
            {var subQ0=sQuery(id+"F0.wireOp",EDGE,"E32");var subQ1=sQuery(id+"F0.wireOp",EDGE,"E5");var subQ2=makeQuery(id+"F0.imprint","INTERSECT",VERTEX,{"derivedFrom":[subQ1,sQuery(id+"F0.wireOp",EDGE,"E10"),subQ0]});Q39=makeQuery(id+"F0.imprint","IMPRINT",FACE,{"disambiguationData":[TD([[makeQuery(id+"F0.imprint","IMPRINT",EDGE,{"disambiguationData":[TD([[subQ2,-1.0]])],"derivedFrom":subQ1}),-1.0]])]});}
            var Q40;
            {var subQ0=sQuery(id+"F0.wireOp",EDGE,"E18");var subQ1=sQuery(id+"F0.wireOp",EDGE,"E4");var subQ2=makeQuery(id+"F0.imprint","INTERSECT",VERTEX,{"derivedFrom":[subQ1,subQ0,sQuery(id+"F0.wireOp",EDGE,"E30")]});Q40=makeQuery(id+"F0.imprint","IMPRINT",FACE,{"disambiguationData":[TD([[makeQuery(id+"F0.imprint","IMPRINT",EDGE,{"disambiguationData":[TD([[subQ2,-1.0]])],"derivedFrom":subQ1}),-1.0]])]});}
            var Q41;
            {var subQ0=sQuery(id+"F0.wireOp",EDGE,"E32");var subQ1=sQuery(id+"F0.wireOp",EDGE,"E11");var subQ2=makeQuery(id+"F0.imprint","INTERSECT",VERTEX,{"derivedFrom":[sQuery(id+"F0.wireOp",EDGE,"E4"),subQ1,subQ0]});Q41=makeQuery(id+"F0.imprint","IMPRINT",FACE,{"disambiguationData":[TD([[makeQuery(id+"F0.imprint","IMPRINT",EDGE,{"disambiguationData":[TD([[subQ2,-1.0]])],"derivedFrom":subQ1}),-1.0]])]});}
            var Q42;
            {var subQ0=sQuery(id+"F0.wireOp",EDGE,"E32");var subQ1=sQuery(id+"F0.wireOp",EDGE,"E15");var subQ2=makeQuery(id+"F0.imprint","INTERSECT",VERTEX,{"derivedFrom":[sQuery(id+"F0.wireOp",EDGE,"E3"),subQ1,subQ0]});Q42=makeQuery(id+"F0.imprint","IMPRINT",FACE,{"disambiguationData":[TD([[makeQuery(id+"F0.imprint","IMPRINT",EDGE,{"disambiguationData":[TD([[subQ2,1.0]])],"derivedFrom":subQ1}),-1.0]])]});}
            var Q43;
            {var subQ0=sQuery(id+"F0.wireOp",EDGE,"E32");var subQ1=sQuery(id+"F0.wireOp",EDGE,"E3");var subQ2=makeQuery(id+"F0.imprint","INTERSECT",VERTEX,{"derivedFrom":[subQ1,sQuery(id+"F0.wireOp",EDGE,"E15"),subQ0]});Q43=makeQuery(id+"F0.imprint","IMPRINT",FACE,{"disambiguationData":[TD([[makeQuery(id+"F0.imprint","IMPRINT",EDGE,{"disambiguationData":[TD([[subQ2,-1.0]])],"derivedFrom":subQ1}),-1.0]])]});}
            var Q44;
            {var subQ0=sQuery(id+"F0.wireOp",EDGE,"E17");var subQ1=sQuery(id+"F0.wireOp",EDGE,"E6");var subQ2=makeQuery(id+"F0.imprint","INTERSECT",VERTEX,{"derivedFrom":[subQ1,subQ0,sQuery(id+"F0.wireOp",EDGE,"E30")]});Q44=makeQuery(id+"F0.imprint","IMPRINT",FACE,{"disambiguationData":[TD([[makeQuery(id+"F0.imprint","IMPRINT",EDGE,{"disambiguationData":[TD([[subQ2,-1.0]])],"derivedFrom":subQ1}),-1.0]])]});}
            var Q45;
            {var subQ0=sQuery(id+"F0.wireOp",EDGE,"E32");var subQ1=sQuery(id+"F0.wireOp",EDGE,"E10");var subQ2=makeQuery(id+"F0.imprint","INTERSECT",VERTEX,{"derivedFrom":[sQuery(id+"F0.wireOp",EDGE,"E6"),subQ1,subQ0]});Q45=makeQuery(id+"F0.imprint","IMPRINT",FACE,{"disambiguationData":[TD([[makeQuery(id+"F0.imprint","IMPRINT",EDGE,{"disambiguationData":[TD([[subQ2,-1.0]])],"derivedFrom":subQ1}),-1.0]])]});}
            var Q46;
            {var subQ0=sQuery(id+"F0.wireOp",EDGE,"E32");var subQ1=sQuery(id+"F0.wireOp",EDGE,"E14");var subQ2=makeQuery(id+"F0.imprint","INTERSECT",VERTEX,{"derivedFrom":[sQuery(id+"F0.wireOp",EDGE,"E4"),subQ1,subQ0]});Q46=makeQuery(id+"F0.imprint","IMPRINT",FACE,{"disambiguationData":[TD([[makeQuery(id+"F0.imprint","IMPRINT",EDGE,{"disambiguationData":[TD([[subQ2,1.0]])],"derivedFrom":subQ1}),-1.0]])]});}
            var Q47;
            {var subQ0=sQuery(id+"F0.wireOp",EDGE,"E32");var subQ1=sQuery(id+"F0.wireOp",EDGE,"E4");var subQ2=makeQuery(id+"F0.imprint","INTERSECT",VERTEX,{"derivedFrom":[subQ1,sQuery(id+"F0.wireOp",EDGE,"E14"),subQ0]});Q47=makeQuery(id+"F0.imprint","IMPRINT",FACE,{"disambiguationData":[TD([[makeQuery(id+"F0.imprint","IMPRINT",EDGE,{"disambiguationData":[TD([[subQ2,-1.0]])],"derivedFrom":subQ1}),-1.0]])]});}
            var Q48;
            {var subQ0=sQuery(id+"F0.wireOp",EDGE,"E32");var subQ1=sQuery(id+"F0.wireOp",EDGE,"E14");var subQ2=makeQuery(id+"F0.imprint","INTERSECT",VERTEX,{"derivedFrom":[sQuery(id+"F0.wireOp",EDGE,"E4"),subQ1,subQ0]});Q48=makeQuery(id+"F0.imprint","IMPRINT",FACE,{"disambiguationData":[TD([[makeQuery(id+"F0.imprint","IMPRINT",EDGE,{"disambiguationData":[TD([[subQ2,1.0]])],"derivedFrom":subQ1}),-1.0]])]});}
            var Q49;
            {var subQ0=sQuery(id+"F0.wireOp",EDGE,"E36");var subQ1=sQuery(id+"F0.wireOp",EDGE,"E18");var subQ2=makeQuery(id+"F0.imprint","INTERSECT",VERTEX,{"derivedFrom":[sQuery(id+"F0.wireOp",EDGE,"E7"),subQ1,subQ0]});Q49=makeQuery(id+"F0.imprint","IMPRINT",FACE,{"disambiguationData":[TD([[makeQuery(id+"F0.imprint","IMPRINT",EDGE,{"disambiguationData":[TD([[subQ2,1.0]])],"derivedFrom":subQ1}),-1.0]])]});}
            var Q50;
            {var subQ0=sQuery(id+"F0.wireOp",EDGE,"E36");var subQ1=sQuery(id+"F0.wireOp",EDGE,"E7");var subQ2=makeQuery(id+"F0.imprint","INTERSECT",VERTEX,{"derivedFrom":[subQ1,sQuery(id+"F0.wireOp",EDGE,"E18"),subQ0]});Q50=makeQuery(id+"F0.imprint","IMPRINT",FACE,{"disambiguationData":[TD([[makeQuery(id+"F0.imprint","IMPRINT",EDGE,{"disambiguationData":[TD([[subQ2,-1.0]])],"derivedFrom":subQ1}),-1.0]])]});}
            var Q51;
            {var subQ0=sQuery(id+"F0.wireOp",EDGE,"E36");var subQ1=sQuery(id+"F0.wireOp",EDGE,"E19");var subQ2=makeQuery(id+"F0.imprint","INTERSECT",VERTEX,{"derivedFrom":[sQuery(id+"F0.wireOp",EDGE,"E11"),subQ1,subQ0]});Q51=makeQuery(id+"F0.imprint","IMPRINT",FACE,{"disambiguationData":[TD([[makeQuery(id+"F0.imprint","IMPRINT",EDGE,{"disambiguationData":[TD([[subQ2,-1.0]])],"derivedFrom":subQ1}),-1.0]])]});}
            var Q52;
            {var subQ0=sQuery(id+"F0.wireOp",EDGE,"E12");var subQ1=sQuery(id+"F0.wireOp",EDGE,"E3");var subQ2=makeQuery(id+"F0.imprint","INTERSECT",VERTEX,{"derivedFrom":[subQ1,subQ0,sQuery(id+"F0.wireOp",EDGE,"E32")]});Q52=makeQuery(id+"F0.imprint","IMPRINT",FACE,{"disambiguationData":[TD([[makeQuery(id+"F0.imprint","IMPRINT",EDGE,{"disambiguationData":[TD([[subQ2,-1.0]])],"derivedFrom":subQ1}),-1.0]])]});}
            var Q53;
            {var subQ0=sQuery(id+"F0.wireOp",EDGE,"E36");var subQ1=sQuery(id+"F0.wireOp",EDGE,"E17");var subQ2=makeQuery(id+"F0.imprint","INTERSECT",VERTEX,{"derivedFrom":[sQuery(id+"F0.wireOp",EDGE,"E5"),subQ1,subQ0]});Q53=makeQuery(id+"F0.imprint","IMPRINT",FACE,{"disambiguationData":[TD([[makeQuery(id+"F0.imprint","IMPRINT",EDGE,{"disambiguationData":[TD([[subQ2,1.0]])],"derivedFrom":subQ1}),-1.0]])]});}
            var Q54;
            {var subQ0=sQuery(id+"F0.wireOp",EDGE,"E36");var subQ1=sQuery(id+"F0.wireOp",EDGE,"E5");var subQ2=makeQuery(id+"F0.imprint","INTERSECT",VERTEX,{"derivedFrom":[subQ1,sQuery(id+"F0.wireOp",EDGE,"E17"),subQ0]});Q54=makeQuery(id+"F0.imprint","IMPRINT",FACE,{"disambiguationData":[TD([[makeQuery(id+"F0.imprint","IMPRINT",EDGE,{"disambiguationData":[TD([[subQ2,-1.0]])],"derivedFrom":subQ1}),-1.0]])]});}
            var Q55;
            {var subQ0=sQuery(id+"F0.wireOp",EDGE,"E36");var subQ1=sQuery(id+"F0.wireOp",EDGE,"E18");var subQ2=makeQuery(id+"F0.imprint","INTERSECT",VERTEX,{"derivedFrom":[sQuery(id+"F0.wireOp",EDGE,"E10"),subQ1,subQ0]});Q55=makeQuery(id+"F0.imprint","IMPRINT",FACE,{"disambiguationData":[TD([[makeQuery(id+"F0.imprint","IMPRINT",EDGE,{"disambiguationData":[TD([[subQ2,-1.0]])],"derivedFrom":subQ1}),-1.0]])]});}
            var Q56;
            {var subQ0=sQuery(id+"F0.wireOp",EDGE,"E11");var subQ1=sQuery(id+"F0.wireOp",EDGE,"E4");var subQ2=makeQuery(id+"F0.imprint","INTERSECT",VERTEX,{"derivedFrom":[subQ1,subQ0,sQuery(id+"F0.wireOp",EDGE,"E32")]});Q56=makeQuery(id+"F0.imprint","IMPRINT",FACE,{"disambiguationData":[TD([[makeQuery(id+"F0.imprint","IMPRINT",EDGE,{"disambiguationData":[TD([[subQ2,-1.0]])],"derivedFrom":subQ1}),-1.0]])]});}
            var Q57;
            {var subQ0=sQuery(id+"F0.wireOp",EDGE,"E36");var subQ1=sQuery(id+"F0.wireOp",EDGE,"E22");var subQ2=makeQuery(id+"F0.imprint","INTERSECT",VERTEX,{"derivedFrom":[sQuery(id+"F0.wireOp",EDGE,"E3"),subQ1,subQ0]});Q57=makeQuery(id+"F0.imprint","IMPRINT",FACE,{"disambiguationData":[TD([[makeQuery(id+"F0.imprint","IMPRINT",EDGE,{"disambiguationData":[TD([[subQ2,1.0]])],"derivedFrom":subQ1}),-1.0]])]});}
            var Q58;
            {var subQ0=sQuery(id+"F0.wireOp",EDGE,"E36");var subQ1=sQuery(id+"F0.wireOp",EDGE,"E3");var subQ2=makeQuery(id+"F0.imprint","INTERSECT",VERTEX,{"derivedFrom":[subQ1,sQuery(id+"F0.wireOp",EDGE,"E22"),subQ0]});Q58=makeQuery(id+"F0.imprint","IMPRINT",FACE,{"disambiguationData":[TD([[makeQuery(id+"F0.imprint","IMPRINT",EDGE,{"disambiguationData":[TD([[subQ2,-1.0]])],"derivedFrom":subQ1}),-1.0]])]});}
            var Q59;
            {var subQ0=sQuery(id+"F0.wireOp",EDGE,"E36");var subQ1=sQuery(id+"F0.wireOp",EDGE,"E17");var subQ2=makeQuery(id+"F0.imprint","INTERSECT",VERTEX,{"derivedFrom":[sQuery(id+"F0.wireOp",EDGE,"E15"),subQ1,subQ0]});Q59=makeQuery(id+"F0.imprint","IMPRINT",FACE,{"disambiguationData":[TD([[makeQuery(id+"F0.imprint","IMPRINT",EDGE,{"disambiguationData":[TD([[subQ2,-1.0]])],"derivedFrom":subQ1}),-1.0]])]});}
            var Q60;
            {var subQ0=sQuery(id+"F0.wireOp",EDGE,"E10");var subQ1=sQuery(id+"F0.wireOp",EDGE,"E6");var subQ2=makeQuery(id+"F0.imprint","INTERSECT",VERTEX,{"derivedFrom":[subQ1,subQ0,sQuery(id+"F0.wireOp",EDGE,"E32")]});Q60=makeQuery(id+"F0.imprint","IMPRINT",FACE,{"disambiguationData":[TD([[makeQuery(id+"F0.imprint","IMPRINT",EDGE,{"disambiguationData":[TD([[subQ2,-1.0]])],"derivedFrom":subQ1}),-1.0]])]});}
            var Q61;
            {var subQ0=sQuery(id+"F0.wireOp",EDGE,"E36");var subQ1=sQuery(id+"F0.wireOp",EDGE,"E21");var subQ2=makeQuery(id+"F0.imprint","INTERSECT",VERTEX,{"derivedFrom":[sQuery(id+"F0.wireOp",EDGE,"E4"),subQ1,subQ0]});Q61=makeQuery(id+"F0.imprint","IMPRINT",FACE,{"disambiguationData":[TD([[makeQuery(id+"F0.imprint","IMPRINT",EDGE,{"disambiguationData":[TD([[subQ2,1.0]])],"derivedFrom":subQ1}),-1.0]])]});}
            var Q62;
            {var subQ0=sQuery(id+"F0.wireOp",EDGE,"E36");var subQ1=sQuery(id+"F0.wireOp",EDGE,"E4");var subQ2=makeQuery(id+"F0.imprint","INTERSECT",VERTEX,{"derivedFrom":[subQ1,sQuery(id+"F0.wireOp",EDGE,"E21"),subQ0]});Q62=makeQuery(id+"F0.imprint","IMPRINT",FACE,{"disambiguationData":[TD([[makeQuery(id+"F0.imprint","IMPRINT",EDGE,{"disambiguationData":[TD([[subQ2,-1.0]])],"derivedFrom":subQ1}),-1.0]])]});}
            var Q63;
            {var subQ0=sQuery(id+"F0.wireOp",EDGE,"E36");var subQ1=sQuery(id+"F0.wireOp",EDGE,"E22");var subQ2=makeQuery(id+"F0.imprint","INTERSECT",VERTEX,{"derivedFrom":[sQuery(id+"F0.wireOp",EDGE,"E14"),subQ1,subQ0]});Q63=makeQuery(id+"F0.imprint","IMPRINT",FACE,{"disambiguationData":[TD([[makeQuery(id+"F0.imprint","IMPRINT",EDGE,{"disambiguationData":[TD([[subQ2,-1.0]])],"derivedFrom":subQ1}),-1.0]])]});}
            var Q64;
            {var subQ0=sQuery(id+"F0.wireOp",EDGE,"E15");var subQ1=sQuery(id+"F0.wireOp",EDGE,"E8");var subQ2=makeQuery(id+"F0.imprint","INTERSECT",VERTEX,{"derivedFrom":[subQ1,subQ0,sQuery(id+"F0.wireOp",EDGE,"E32")]});Q64=makeQuery(id+"F0.imprint","IMPRINT",FACE,{"disambiguationData":[TD([[makeQuery(id+"F0.imprint","IMPRINT",EDGE,{"disambiguationData":[TD([[subQ2,-1.0]])],"derivedFrom":subQ1}),-1.0]])]});}
            var Q65;
            {var subQ0=sQuery(id+"F0.wireOp",EDGE,"E36");var subQ1=sQuery(id+"F0.wireOp",EDGE,"E20");var subQ2=makeQuery(id+"F0.imprint","INTERSECT",VERTEX,{"derivedFrom":[sQuery(id+"F0.wireOp",EDGE,"E6"),subQ1,subQ0]});Q65=makeQuery(id+"F0.imprint","IMPRINT",FACE,{"disambiguationData":[TD([[makeQuery(id+"F0.imprint","IMPRINT",EDGE,{"disambiguationData":[TD([[subQ2,1.0]])],"derivedFrom":subQ1}),-1.0]])]});}
            var Q66;
            {var subQ0=sQuery(id+"F0.wireOp",EDGE,"E36");var subQ1=sQuery(id+"F0.wireOp",EDGE,"E6");var subQ2=makeQuery(id+"F0.imprint","INTERSECT",VERTEX,{"derivedFrom":[subQ1,sQuery(id+"F0.wireOp",EDGE,"E20"),subQ0]});Q66=makeQuery(id+"F0.imprint","IMPRINT",FACE,{"disambiguationData":[TD([[makeQuery(id+"F0.imprint","IMPRINT",EDGE,{"disambiguationData":[TD([[subQ2,-1.0]])],"derivedFrom":subQ1}),-1.0]])]});}
            var Q67;
            {var subQ0=sQuery(id+"F0.wireOp",EDGE,"E36");var subQ1=sQuery(id+"F0.wireOp",EDGE,"E21");var subQ2=makeQuery(id+"F0.imprint","INTERSECT",VERTEX,{"derivedFrom":[sQuery(id+"F0.wireOp",EDGE,"E13"),subQ1,subQ0]});Q67=makeQuery(id+"F0.imprint","IMPRINT",FACE,{"disambiguationData":[TD([[makeQuery(id+"F0.imprint","IMPRINT",EDGE,{"disambiguationData":[TD([[subQ2,-1.0]])],"derivedFrom":subQ1}),-1.0]])]});}
            var Q68;
            {var subQ0=sQuery(id+"F0.wireOp",EDGE,"E14");var subQ1=sQuery(id+"F0.wireOp",EDGE,"E7");var subQ2=makeQuery(id+"F0.imprint","INTERSECT",VERTEX,{"derivedFrom":[subQ1,subQ0,sQuery(id+"F0.wireOp",EDGE,"E32")]});Q68=makeQuery(id+"F0.imprint","IMPRINT",FACE,{"disambiguationData":[TD([[makeQuery(id+"F0.imprint","IMPRINT",EDGE,{"disambiguationData":[TD([[subQ2,-1.0]])],"derivedFrom":subQ1}),-1.0]])]});}
            var Q69;
            {var subQ0=sQuery(id+"F0.wireOp",EDGE,"E36");var subQ1=sQuery(id+"F0.wireOp",EDGE,"E19");var subQ2=makeQuery(id+"F0.imprint","INTERSECT",VERTEX,{"derivedFrom":[sQuery(id+"F0.wireOp",EDGE,"E8"),subQ1,subQ0]});Q69=makeQuery(id+"F0.imprint","IMPRINT",FACE,{"disambiguationData":[TD([[makeQuery(id+"F0.imprint","IMPRINT",EDGE,{"disambiguationData":[TD([[subQ2,1.0]])],"derivedFrom":subQ1}),-1.0]])]});}
            var Q70;
            {var subQ0=sQuery(id+"F0.wireOp",EDGE,"E36");var subQ1=sQuery(id+"F0.wireOp",EDGE,"E8");var subQ2=makeQuery(id+"F0.imprint","INTERSECT",VERTEX,{"derivedFrom":[subQ1,sQuery(id+"F0.wireOp",EDGE,"E19"),subQ0]});Q70=makeQuery(id+"F0.imprint","IMPRINT",FACE,{"disambiguationData":[TD([[makeQuery(id+"F0.imprint","IMPRINT",EDGE,{"disambiguationData":[TD([[subQ2,-1.0]])],"derivedFrom":subQ1}),-1.0]])]});}
            var Q71;
            {var subQ0=sQuery(id+"F0.wireOp",EDGE,"E36");var subQ1=sQuery(id+"F0.wireOp",EDGE,"E20");var subQ2=makeQuery(id+"F0.imprint","INTERSECT",VERTEX,{"derivedFrom":[sQuery(id+"F0.wireOp",EDGE,"E12"),subQ1,subQ0]});Q71=makeQuery(id+"F0.imprint","IMPRINT",FACE,{"disambiguationData":[TD([[makeQuery(id+"F0.imprint","IMPRINT",EDGE,{"disambiguationData":[TD([[subQ2,-1.0]])],"derivedFrom":subQ1}),-1.0]])]});}
            var Q72;
            {var subQ0=sQuery(id+"F0.wireOp",EDGE,"E13");var subQ1=sQuery(id+"F0.wireOp",EDGE,"E5");var subQ2=makeQuery(id+"F0.imprint","INTERSECT",VERTEX,{"derivedFrom":[subQ1,subQ0,sQuery(id+"F0.wireOp",EDGE,"E32")]});Q72=makeQuery(id+"F0.imprint","IMPRINT",FACE,{"disambiguationData":[TD([[makeQuery(id+"F0.imprint","IMPRINT",EDGE,{"disambiguationData":[TD([[subQ2,-1.0]])],"derivedFrom":subQ1}),-1.0]])]});}
            var Q73;
            {var subQ0=sQuery(id+"F0.wireOp",EDGE,"E40");var subQ1=sQuery(id+"F0.wireOp",EDGE,"E6");var subQ2=makeQuery(id+"F0.imprint","INTERSECT",VERTEX,{"derivedFrom":[sQuery(id+"F0.wireOp",EDGE,"E4"),subQ1,subQ0]});Q73=makeQuery(id+"F0.imprint","IMPRINT",FACE,{"disambiguationData":[TD([[makeQuery(id+"F0.imprint","IMPRINT",EDGE,{"disambiguationData":[TD([[subQ2,1.0]])],"derivedFrom":subQ1}),-1.0]])]});}
            var Q74;
            {var subQ0=sQuery(id+"F0.wireOp",EDGE,"E40");var subQ1=sQuery(id+"F0.wireOp",EDGE,"E10");var subQ2=makeQuery(id+"F0.imprint","INTERSECT",VERTEX,{"derivedFrom":[subQ1,sQuery(id+"F0.wireOp",EDGE,"E15"),subQ0]});Q74=makeQuery(id+"F0.imprint","IMPRINT",FACE,{"disambiguationData":[TD([[makeQuery(id+"F0.imprint","IMPRINT",EDGE,{"disambiguationData":[TD([[subQ2,-1.0]])],"derivedFrom":subQ1}),-1.0]])]});}
            var Q75;
            {var subQ0=sQuery(id+"F0.wireOp",EDGE,"E40");var subQ1=sQuery(id+"F0.wireOp",EDGE,"E15");var subQ2=makeQuery(id+"F0.imprint","INTERSECT",VERTEX,{"derivedFrom":[sQuery(id+"F0.wireOp",EDGE,"E10"),subQ1,subQ0]});Q75=makeQuery(id+"F0.imprint","IMPRINT",FACE,{"disambiguationData":[TD([[makeQuery(id+"F0.imprint","IMPRINT",EDGE,{"disambiguationData":[TD([[subQ2,1.0]])],"derivedFrom":subQ1}),-1.0]])]});}
            var Q76;
            {var subQ0=sQuery(id+"F0.wireOp",EDGE,"E40");var subQ1=sQuery(id+"F0.wireOp",EDGE,"E3");var subQ2=makeQuery(id+"F0.imprint","INTERSECT",VERTEX,{"derivedFrom":[subQ1,sQuery(id+"F0.wireOp",EDGE,"E4"),subQ0]});Q76=makeQuery(id+"F0.imprint","IMPRINT",FACE,{"disambiguationData":[TD([[makeQuery(id+"F0.imprint","IMPRINT",EDGE,{"disambiguationData":[TD([[subQ2,-1.0]])],"derivedFrom":subQ1}),-1.0]])]});}
            var Q77;
            {var subQ0=sQuery(id+"F0.wireOp",EDGE,"E40");var subQ1=sQuery(id+"F0.wireOp",EDGE,"E4");var subQ2=makeQuery(id+"F0.imprint","INTERSECT",VERTEX,{"derivedFrom":[sQuery(id+"F0.wireOp",EDGE,"E3"),subQ1,subQ0]});Q77=makeQuery(id+"F0.imprint","IMPRINT",FACE,{"disambiguationData":[TD([[makeQuery(id+"F0.imprint","IMPRINT",EDGE,{"disambiguationData":[TD([[subQ2,1.0]])],"derivedFrom":subQ1}),-1.0]])]});}
            var Q78;
            {var subQ0=sQuery(id+"F0.wireOp",EDGE,"E40");var subQ1=sQuery(id+"F0.wireOp",EDGE,"E11");var subQ2=makeQuery(id+"F0.imprint","INTERSECT",VERTEX,{"derivedFrom":[sQuery(id+"F0.wireOp",EDGE,"E10"),subQ1,subQ0]});Q78=makeQuery(id+"F0.imprint","IMPRINT",FACE,{"disambiguationData":[TD([[makeQuery(id+"F0.imprint","IMPRINT",EDGE,{"disambiguationData":[TD([[subQ2,-1.0]])],"derivedFrom":subQ1}),-1.0]])]});}
            var Q79;
            {var subQ0=sQuery(id+"F0.wireOp",EDGE,"E18");var subQ1=sQuery(id+"F0.wireOp",EDGE,"E10");var subQ2=makeQuery(id+"F0.imprint","INTERSECT",VERTEX,{"derivedFrom":[subQ1,subQ0,sQuery(id+"F0.wireOp",EDGE,"E36")]});Q79=makeQuery(id+"F0.imprint","IMPRINT",FACE,{"disambiguationData":[TD([[makeQuery(id+"F0.imprint","IMPRINT",EDGE,{"disambiguationData":[TD([[subQ2,-1.0]])],"derivedFrom":subQ1}),-1.0]])]});}
            var Q80;
            {var subQ0=sQuery(id+"F0.wireOp",EDGE,"E40");var subQ1=sQuery(id+"F0.wireOp",EDGE,"E5");var subQ2=makeQuery(id+"F0.imprint","INTERSECT",VERTEX,{"derivedFrom":[sQuery(id+"F0.wireOp",EDGE,"E3"),subQ1,subQ0]});Q80=makeQuery(id+"F0.imprint","IMPRINT",FACE,{"disambiguationData":[TD([[makeQuery(id+"F0.imprint","IMPRINT",EDGE,{"disambiguationData":[TD([[subQ2,-1.0]])],"derivedFrom":subQ1}),-1.0]])]});}
            var Q81;
            {var subQ0=sQuery(id+"F0.wireOp",EDGE,"E27");var subQ1=sQuery(id+"F0.wireOp",EDGE,"E3");var subQ2=makeQuery(id+"F0.imprint","INTERSECT",VERTEX,{"derivedFrom":[subQ1,subQ0,sQuery(id+"F0.wireOp",EDGE,"E36")]});Q81=makeQuery(id+"F0.imprint","IMPRINT",FACE,{"disambiguationData":[TD([[makeQuery(id+"F0.imprint","IMPRINT",EDGE,{"disambiguationData":[TD([[subQ2,-1.0]])],"derivedFrom":subQ1}),-1.0]])]});}
            var Q82;
            {var subQ0=sQuery(id+"F0.wireOp",EDGE,"E40");var subQ1=sQuery(id+"F0.wireOp",EDGE,"E12");var subQ2=makeQuery(id+"F0.imprint","INTERSECT",VERTEX,{"derivedFrom":[sQuery(id+"F0.wireOp",EDGE,"E11"),subQ1,subQ0]});Q82=makeQuery(id+"F0.imprint","IMPRINT",FACE,{"disambiguationData":[TD([[makeQuery(id+"F0.imprint","IMPRINT",EDGE,{"disambiguationData":[TD([[subQ2,-1.0]])],"derivedFrom":subQ1}),-1.0]])]});}
            var Q83;
            {var subQ0=sQuery(id+"F0.wireOp",EDGE,"E19");var subQ1=sQuery(id+"F0.wireOp",EDGE,"E11");var subQ2=makeQuery(id+"F0.imprint","INTERSECT",VERTEX,{"derivedFrom":[subQ1,subQ0,sQuery(id+"F0.wireOp",EDGE,"E36")]});Q83=makeQuery(id+"F0.imprint","IMPRINT",FACE,{"disambiguationData":[TD([[makeQuery(id+"F0.imprint","IMPRINT",EDGE,{"disambiguationData":[TD([[subQ2,-1.0]])],"derivedFrom":subQ1}),-1.0]])]});}
            var Q84;
            {var subQ0=sQuery(id+"F0.wireOp",EDGE,"E40");var subQ1=sQuery(id+"F0.wireOp",EDGE,"E7");var subQ2=makeQuery(id+"F0.imprint","INTERSECT",VERTEX,{"derivedFrom":[sQuery(id+"F0.wireOp",EDGE,"E5"),subQ1,subQ0]});Q84=makeQuery(id+"F0.imprint","IMPRINT",FACE,{"disambiguationData":[TD([[makeQuery(id+"F0.imprint","IMPRINT",EDGE,{"disambiguationData":[TD([[subQ2,-1.0]])],"derivedFrom":subQ1}),-1.0]])]});}
            var Q85;
            {var subQ0=sQuery(id+"F0.wireOp",EDGE,"E28");var subQ1=sQuery(id+"F0.wireOp",EDGE,"E5");var subQ2=makeQuery(id+"F0.imprint","INTERSECT",VERTEX,{"derivedFrom":[subQ1,subQ0,sQuery(id+"F0.wireOp",EDGE,"E36")]});Q85=makeQuery(id+"F0.imprint","IMPRINT",FACE,{"disambiguationData":[TD([[makeQuery(id+"F0.imprint","IMPRINT",EDGE,{"disambiguationData":[TD([[subQ2,-1.0]])],"derivedFrom":subQ1}),-1.0]])]});}
            var Q86;
            {var subQ0=sQuery(id+"F0.wireOp",EDGE,"E40");var subQ1=sQuery(id+"F0.wireOp",EDGE,"E13");var subQ2=makeQuery(id+"F0.imprint","INTERSECT",VERTEX,{"derivedFrom":[sQuery(id+"F0.wireOp",EDGE,"E12"),subQ1,subQ0]});Q86=makeQuery(id+"F0.imprint","IMPRINT",FACE,{"disambiguationData":[TD([[makeQuery(id+"F0.imprint","IMPRINT",EDGE,{"disambiguationData":[TD([[subQ2,-1.0]])],"derivedFrom":subQ1}),-1.0]])]});}
            var Q87;
            {var subQ0=sQuery(id+"F0.wireOp",EDGE,"E20");var subQ1=sQuery(id+"F0.wireOp",EDGE,"E12");var subQ2=makeQuery(id+"F0.imprint","INTERSECT",VERTEX,{"derivedFrom":[subQ1,subQ0,sQuery(id+"F0.wireOp",EDGE,"E36")]});Q87=makeQuery(id+"F0.imprint","IMPRINT",FACE,{"disambiguationData":[TD([[makeQuery(id+"F0.imprint","IMPRINT",EDGE,{"disambiguationData":[TD([[subQ2,-1.0]])],"derivedFrom":subQ1}),-1.0]])]});}
            var Q88;
            {var subQ0=sQuery(id+"F0.wireOp",EDGE,"E40");var subQ1=sQuery(id+"F0.wireOp",EDGE,"E8");var subQ2=makeQuery(id+"F0.imprint","INTERSECT",VERTEX,{"derivedFrom":[sQuery(id+"F0.wireOp",EDGE,"E7"),subQ1,subQ0]});Q88=makeQuery(id+"F0.imprint","IMPRINT",FACE,{"disambiguationData":[TD([[makeQuery(id+"F0.imprint","IMPRINT",EDGE,{"disambiguationData":[TD([[subQ2,-1.0]])],"derivedFrom":subQ1}),-1.0]])]});}
            var Q89;
            {var subQ0=sQuery(id+"F0.wireOp",EDGE,"E29");var subQ1=sQuery(id+"F0.wireOp",EDGE,"E7");var subQ2=makeQuery(id+"F0.imprint","INTERSECT",VERTEX,{"derivedFrom":[subQ1,subQ0,sQuery(id+"F0.wireOp",EDGE,"E36")]});Q89=makeQuery(id+"F0.imprint","IMPRINT",FACE,{"disambiguationData":[TD([[makeQuery(id+"F0.imprint","IMPRINT",EDGE,{"disambiguationData":[TD([[subQ2,-1.0]])],"derivedFrom":subQ1}),-1.0]])]});}
            var Q90;
            {var subQ0=sQuery(id+"F0.wireOp",EDGE,"E40");var subQ1=sQuery(id+"F0.wireOp",EDGE,"E14");var subQ2=makeQuery(id+"F0.imprint","INTERSECT",VERTEX,{"derivedFrom":[sQuery(id+"F0.wireOp",EDGE,"E13"),subQ1,subQ0]});Q90=makeQuery(id+"F0.imprint","IMPRINT",FACE,{"disambiguationData":[TD([[makeQuery(id+"F0.imprint","IMPRINT",EDGE,{"disambiguationData":[TD([[subQ2,-1.0]])],"derivedFrom":subQ1}),-1.0]])]});}
            var Q91;
            {var subQ0=sQuery(id+"F0.wireOp",EDGE,"E21");var subQ1=sQuery(id+"F0.wireOp",EDGE,"E13");var subQ2=makeQuery(id+"F0.imprint","INTERSECT",VERTEX,{"derivedFrom":[subQ1,subQ0,sQuery(id+"F0.wireOp",EDGE,"E36")]});Q91=makeQuery(id+"F0.imprint","IMPRINT",FACE,{"disambiguationData":[TD([[makeQuery(id+"F0.imprint","IMPRINT",EDGE,{"disambiguationData":[TD([[subQ2,-1.0]])],"derivedFrom":subQ1}),-1.0]])]});}
            var Q92;
            {var subQ0=sQuery(id+"F0.wireOp",EDGE,"E40");var subQ1=sQuery(id+"F0.wireOp",EDGE,"E6");var subQ2=makeQuery(id+"F0.imprint","INTERSECT",VERTEX,{"derivedFrom":[subQ1,sQuery(id+"F0.wireOp",EDGE,"E8"),subQ0]});Q92=makeQuery(id+"F0.imprint","IMPRINT",FACE,{"disambiguationData":[TD([[makeQuery(id+"F0.imprint","IMPRINT",EDGE,{"disambiguationData":[TD([[subQ2,-1.0]])],"derivedFrom":subQ1}),-1.0]])]});}
            var Q93;
            {var subQ0=sQuery(id+"F0.wireOp",EDGE,"E40");var subQ1=sQuery(id+"F0.wireOp",EDGE,"E8");var subQ2=makeQuery(id+"F0.imprint","INTERSECT",VERTEX,{"derivedFrom":[sQuery(id+"F0.wireOp",EDGE,"E6"),subQ1,subQ0]});Q93=makeQuery(id+"F0.imprint","IMPRINT",FACE,{"disambiguationData":[TD([[makeQuery(id+"F0.imprint","IMPRINT",EDGE,{"disambiguationData":[TD([[subQ2,1.0]])],"derivedFrom":subQ1}),-1.0]])]});}
            var Q94;
            {var subQ0=sQuery(id+"F0.wireOp",EDGE,"E40");var subQ1=sQuery(id+"F0.wireOp",EDGE,"E15");var subQ2=makeQuery(id+"F0.imprint","INTERSECT",VERTEX,{"derivedFrom":[sQuery(id+"F0.wireOp",EDGE,"E14"),subQ1,subQ0]});Q94=makeQuery(id+"F0.imprint","IMPRINT",FACE,{"disambiguationData":[TD([[makeQuery(id+"F0.imprint","IMPRINT",EDGE,{"disambiguationData":[TD([[subQ2,-1.0]])],"derivedFrom":subQ1}),-1.0]])]});}
            var Q95;
            {var subQ0=sQuery(id+"F0.wireOp",EDGE,"E22");var subQ1=sQuery(id+"F0.wireOp",EDGE,"E14");var subQ2=makeQuery(id+"F0.imprint","INTERSECT",VERTEX,{"derivedFrom":[subQ1,subQ0,sQuery(id+"F0.wireOp",EDGE,"E36")]});Q95=makeQuery(id+"F0.imprint","IMPRINT",FACE,{"disambiguationData":[TD([[makeQuery(id+"F0.imprint","IMPRINT",EDGE,{"disambiguationData":[TD([[subQ2,-1.0]])],"derivedFrom":subQ1}),-1.0]])]});}
            var Q96;
            {var subQ0=sQuery(id+"F0.wireOp",EDGE,"E40");var subQ1=sQuery(id+"F0.wireOp",EDGE,"E4");var subQ2=makeQuery(id+"F0.imprint","INTERSECT",VERTEX,{"derivedFrom":[subQ1,sQuery(id+"F0.wireOp",EDGE,"E6"),subQ0]});Q96=makeQuery(id+"F0.imprint","IMPRINT",FACE,{"disambiguationData":[TD([[makeQuery(id+"F0.imprint","IMPRINT",EDGE,{"disambiguationData":[TD([[subQ2,-1.0]])],"derivedFrom":subQ1}),-1.0]])]});}
            var Q97;
            {var subQ0=sQuery(id+"F0.wireOp",EDGE,"E38");var subQ1=sQuery(id+"F0.wireOp",EDGE,"E10");var subQ2=makeQuery(id+"F0.imprint","INTERSECT",VERTEX,{"derivedFrom":[subQ1,sQuery(id+"F0.wireOp",EDGE,"E22"),subQ0]});Q97=makeQuery(id+"F0.imprint","IMPRINT",FACE,{"disambiguationData":[TD([[makeQuery(id+"F0.imprint","IMPRINT",EDGE,{"disambiguationData":[TD([[subQ2,-1.0]])],"derivedFrom":subQ1}),-1.0]])]});}
            var Q98;
            {var subQ0=sQuery(id+"F0.wireOp",EDGE,"E38");var subQ1=sQuery(id+"F0.wireOp",EDGE,"E24");var subQ2=makeQuery(id+"F0.imprint","INTERSECT",VERTEX,{"derivedFrom":[sQuery(id+"F0.wireOp",EDGE,"E4"),subQ1,subQ0]});Q98=makeQuery(id+"F0.imprint","IMPRINT",FACE,{"disambiguationData":[TD([[makeQuery(id+"F0.imprint","IMPRINT",EDGE,{"disambiguationData":[TD([[subQ2,1.0]])],"derivedFrom":subQ1}),-1.0]])]});}
            var Q99;
            {var subQ0=sQuery(id+"F0.wireOp",EDGE,"E38");var subQ1=sQuery(id+"F0.wireOp",EDGE,"E4");var subQ2=makeQuery(id+"F0.imprint","INTERSECT",VERTEX,{"derivedFrom":[subQ1,sQuery(id+"F0.wireOp",EDGE,"E24"),subQ0]});Q99=makeQuery(id+"F0.imprint","IMPRINT",FACE,{"disambiguationData":[TD([[makeQuery(id+"F0.imprint","IMPRINT",EDGE,{"disambiguationData":[TD([[subQ2,-1.0]])],"derivedFrom":subQ1}),-1.0]])]});}
            var Q100;
            {var subQ0=sQuery(id+"F0.wireOp",EDGE,"E38");var subQ1=sQuery(id+"F0.wireOp",EDGE,"E21");var subQ2=makeQuery(id+"F0.imprint","INTERSECT",VERTEX,{"derivedFrom":[sQuery(id+"F0.wireOp",EDGE,"E15"),subQ1,subQ0]});Q100=makeQuery(id+"F0.imprint","IMPRINT",FACE,{"disambiguationData":[TD([[makeQuery(id+"F0.imprint","IMPRINT",EDGE,{"disambiguationData":[TD([[subQ2,1.0]])],"derivedFrom":subQ1}),-1.0]])]});}
            var Q101;
            {var subQ0=sQuery(id+"F0.wireOp",EDGE,"E15");var subQ1=sQuery(id+"F0.wireOp",EDGE,"E14");var subQ2=makeQuery(id+"F0.imprint","INTERSECT",VERTEX,{"derivedFrom":[subQ1,subQ0,sQuery(id+"F0.wireOp",EDGE,"E40")]});Q101=makeQuery(id+"F0.imprint","IMPRINT",FACE,{"disambiguationData":[TD([[makeQuery(id+"F0.imprint","IMPRINT",EDGE,{"disambiguationData":[TD([[subQ2,-1.0]])],"derivedFrom":subQ1}),-1.0]])]});}
            var Q102;
            {var subQ0=sQuery(id+"F0.wireOp",EDGE,"E38");var subQ1=sQuery(id+"F0.wireOp",EDGE,"E24");var subQ2=makeQuery(id+"F0.imprint","INTERSECT",VERTEX,{"derivedFrom":[sQuery(id+"F0.wireOp",EDGE,"E14"),subQ1,subQ0]});Q102=makeQuery(id+"F0.imprint","IMPRINT",FACE,{"disambiguationData":[TD([[makeQuery(id+"F0.imprint","IMPRINT",EDGE,{"disambiguationData":[TD([[subQ2,-1.0]])],"derivedFrom":subQ1}),-1.0]])]});}
            var Q103;
            {var subQ0=sQuery(id+"F0.wireOp",EDGE,"E38");var subQ1=sQuery(id+"F0.wireOp",EDGE,"E6");var subQ2=makeQuery(id+"F0.imprint","INTERSECT",VERTEX,{"derivedFrom":[subQ1,sQuery(id+"F0.wireOp",EDGE,"E29"),subQ0]});Q103=makeQuery(id+"F0.imprint","IMPRINT",FACE,{"disambiguationData":[TD([[makeQuery(id+"F0.imprint","IMPRINT",EDGE,{"disambiguationData":[TD([[subQ2,-1.0]])],"derivedFrom":subQ1}),-1.0]])]});}
            var Q104;
            {var subQ0=sQuery(id+"F0.wireOp",EDGE,"E38");var subQ1=sQuery(id+"F0.wireOp",EDGE,"E20");var subQ2=makeQuery(id+"F0.imprint","INTERSECT",VERTEX,{"derivedFrom":[sQuery(id+"F0.wireOp",EDGE,"E14"),subQ1,subQ0]});Q104=makeQuery(id+"F0.imprint","IMPRINT",FACE,{"disambiguationData":[TD([[makeQuery(id+"F0.imprint","IMPRINT",EDGE,{"disambiguationData":[TD([[subQ2,1.0]])],"derivedFrom":subQ1}),-1.0]])]});}
            var Q105;
            {var subQ0=sQuery(id+"F0.wireOp",EDGE,"E14");var subQ1=sQuery(id+"F0.wireOp",EDGE,"E13");var subQ2=makeQuery(id+"F0.imprint","INTERSECT",VERTEX,{"derivedFrom":[subQ1,subQ0,sQuery(id+"F0.wireOp",EDGE,"E40")]});Q105=makeQuery(id+"F0.imprint","IMPRINT",FACE,{"disambiguationData":[TD([[makeQuery(id+"F0.imprint","IMPRINT",EDGE,{"disambiguationData":[TD([[subQ2,-1.0]])],"derivedFrom":subQ1}),-1.0]])]});}
            var Q106;
            {var subQ0=sQuery(id+"F0.wireOp",EDGE,"E38");var subQ1=sQuery(id+"F0.wireOp",EDGE,"E28");var subQ2=makeQuery(id+"F0.imprint","INTERSECT",VERTEX,{"derivedFrom":[sQuery(id+"F0.wireOp",EDGE,"E8"),subQ1,subQ0]});Q106=makeQuery(id+"F0.imprint","IMPRINT",FACE,{"disambiguationData":[TD([[makeQuery(id+"F0.imprint","IMPRINT",EDGE,{"disambiguationData":[TD([[subQ2,1.0]])],"derivedFrom":subQ1}),-1.0]])]});}
            var Q107;
            {var subQ0=sQuery(id+"F0.wireOp",EDGE,"E8");var subQ1=sQuery(id+"F0.wireOp",EDGE,"E7");var subQ2=makeQuery(id+"F0.imprint","INTERSECT",VERTEX,{"derivedFrom":[subQ1,subQ0,sQuery(id+"F0.wireOp",EDGE,"E40")]});Q107=makeQuery(id+"F0.imprint","IMPRINT",FACE,{"disambiguationData":[TD([[makeQuery(id+"F0.imprint","IMPRINT",EDGE,{"disambiguationData":[TD([[subQ2,-1.0]])],"derivedFrom":subQ1}),-1.0]])]});}
            var Q108;
            {var subQ0=sQuery(id+"F0.wireOp",EDGE,"E38");var subQ1=sQuery(id+"F0.wireOp",EDGE,"E19");var subQ2=makeQuery(id+"F0.imprint","INTERSECT",VERTEX,{"derivedFrom":[sQuery(id+"F0.wireOp",EDGE,"E13"),subQ1,subQ0]});Q108=makeQuery(id+"F0.imprint","IMPRINT",FACE,{"disambiguationData":[TD([[makeQuery(id+"F0.imprint","IMPRINT",EDGE,{"disambiguationData":[TD([[subQ2,1.0]])],"derivedFrom":subQ1}),-1.0]])]});}
            var Q109;
            {var subQ0=sQuery(id+"F0.wireOp",EDGE,"E13");var subQ1=sQuery(id+"F0.wireOp",EDGE,"E12");var subQ2=makeQuery(id+"F0.imprint","INTERSECT",VERTEX,{"derivedFrom":[subQ1,subQ0,sQuery(id+"F0.wireOp",EDGE,"E40")]});Q109=makeQuery(id+"F0.imprint","IMPRINT",FACE,{"disambiguationData":[TD([[makeQuery(id+"F0.imprint","IMPRINT",EDGE,{"disambiguationData":[TD([[subQ2,-1.0]])],"derivedFrom":subQ1}),-1.0]])]});}
            var Q110;
            {var subQ0=sQuery(id+"F0.wireOp",EDGE,"E38");var subQ1=sQuery(id+"F0.wireOp",EDGE,"E27");var subQ2=makeQuery(id+"F0.imprint","INTERSECT",VERTEX,{"derivedFrom":[sQuery(id+"F0.wireOp",EDGE,"E7"),subQ1,subQ0]});Q110=makeQuery(id+"F0.imprint","IMPRINT",FACE,{"disambiguationData":[TD([[makeQuery(id+"F0.imprint","IMPRINT",EDGE,{"disambiguationData":[TD([[subQ2,1.0]])],"derivedFrom":subQ1}),-1.0]])]});}
            var Q111;
            {var subQ0=sQuery(id+"F0.wireOp",EDGE,"E7");var subQ1=sQuery(id+"F0.wireOp",EDGE,"E5");var subQ2=makeQuery(id+"F0.imprint","INTERSECT",VERTEX,{"derivedFrom":[subQ1,subQ0,sQuery(id+"F0.wireOp",EDGE,"E40")]});Q111=makeQuery(id+"F0.imprint","IMPRINT",FACE,{"disambiguationData":[TD([[makeQuery(id+"F0.imprint","IMPRINT",EDGE,{"disambiguationData":[TD([[subQ2,-1.0]])],"derivedFrom":subQ1}),-1.0]])]});}
            var Q112;
            {var subQ0=sQuery(id+"F0.wireOp",EDGE,"E38");var subQ1=sQuery(id+"F0.wireOp",EDGE,"E18");var subQ2=makeQuery(id+"F0.imprint","INTERSECT",VERTEX,{"derivedFrom":[sQuery(id+"F0.wireOp",EDGE,"E12"),subQ1,subQ0]});Q112=makeQuery(id+"F0.imprint","IMPRINT",FACE,{"disambiguationData":[TD([[makeQuery(id+"F0.imprint","IMPRINT",EDGE,{"disambiguationData":[TD([[subQ2,1.0]])],"derivedFrom":subQ1}),-1.0]])]});}
            var Q113;
            {var subQ0=sQuery(id+"F0.wireOp",EDGE,"E12");var subQ1=sQuery(id+"F0.wireOp",EDGE,"E11");var subQ2=makeQuery(id+"F0.imprint","INTERSECT",VERTEX,{"derivedFrom":[subQ1,subQ0,sQuery(id+"F0.wireOp",EDGE,"E40")]});Q113=makeQuery(id+"F0.imprint","IMPRINT",FACE,{"disambiguationData":[TD([[makeQuery(id+"F0.imprint","IMPRINT",EDGE,{"disambiguationData":[TD([[subQ2,-1.0]])],"derivedFrom":subQ1}),-1.0]])]});}
            var Q114;
            {var subQ0=sQuery(id+"F0.wireOp",EDGE,"E38");var subQ1=sQuery(id+"F0.wireOp",EDGE,"E26");var subQ2=makeQuery(id+"F0.imprint","INTERSECT",VERTEX,{"derivedFrom":[sQuery(id+"F0.wireOp",EDGE,"E5"),subQ1,subQ0]});Q114=makeQuery(id+"F0.imprint","IMPRINT",FACE,{"disambiguationData":[TD([[makeQuery(id+"F0.imprint","IMPRINT",EDGE,{"disambiguationData":[TD([[subQ2,1.0]])],"derivedFrom":subQ1}),-1.0]])]});}
            var Q115;
            {var subQ0=sQuery(id+"F0.wireOp",EDGE,"E5");var subQ1=sQuery(id+"F0.wireOp",EDGE,"E3");var subQ2=makeQuery(id+"F0.imprint","INTERSECT",VERTEX,{"derivedFrom":[subQ1,subQ0,sQuery(id+"F0.wireOp",EDGE,"E40")]});Q115=makeQuery(id+"F0.imprint","IMPRINT",FACE,{"disambiguationData":[TD([[makeQuery(id+"F0.imprint","IMPRINT",EDGE,{"disambiguationData":[TD([[subQ2,-1.0]])],"derivedFrom":subQ1}),-1.0]])]});}
            var Q116;
            {var subQ0=sQuery(id+"F0.wireOp",EDGE,"E38");var subQ1=sQuery(id+"F0.wireOp",EDGE,"E17");var subQ2=makeQuery(id+"F0.imprint","INTERSECT",VERTEX,{"derivedFrom":[sQuery(id+"F0.wireOp",EDGE,"E11"),subQ1,subQ0]});Q116=makeQuery(id+"F0.imprint","IMPRINT",FACE,{"disambiguationData":[TD([[makeQuery(id+"F0.imprint","IMPRINT",EDGE,{"disambiguationData":[TD([[subQ2,1.0]])],"derivedFrom":subQ1}),-1.0]])]});}
            var Q117;
            {var subQ0=sQuery(id+"F0.wireOp",EDGE,"E11");var subQ1=sQuery(id+"F0.wireOp",EDGE,"E10");var subQ2=makeQuery(id+"F0.imprint","INTERSECT",VERTEX,{"derivedFrom":[subQ1,subQ0,sQuery(id+"F0.wireOp",EDGE,"E40")]});Q117=makeQuery(id+"F0.imprint","IMPRINT",FACE,{"disambiguationData":[TD([[makeQuery(id+"F0.imprint","IMPRINT",EDGE,{"disambiguationData":[TD([[subQ2,-1.0]])],"derivedFrom":subQ1}),-1.0]])]});}
            var Q118;
            {var subQ0=sQuery(id+"F0.wireOp",EDGE,"E38");var subQ1=sQuery(id+"F0.wireOp",EDGE,"E25");var subQ2=makeQuery(id+"F0.imprint","INTERSECT",VERTEX,{"derivedFrom":[sQuery(id+"F0.wireOp",EDGE,"E3"),subQ1,subQ0]});Q118=makeQuery(id+"F0.imprint","IMPRINT",FACE,{"disambiguationData":[TD([[makeQuery(id+"F0.imprint","IMPRINT",EDGE,{"disambiguationData":[TD([[subQ2,1.0]])],"derivedFrom":subQ1}),-1.0]])]});}
            var Q119;
            {var subQ0=sQuery(id+"F0.wireOp",EDGE,"E38");var subQ1=sQuery(id+"F0.wireOp",EDGE,"E3");var subQ2=makeQuery(id+"F0.imprint","INTERSECT",VERTEX,{"derivedFrom":[subQ1,sQuery(id+"F0.wireOp",EDGE,"E25"),subQ0]});Q119=makeQuery(id+"F0.imprint","IMPRINT",FACE,{"disambiguationData":[TD([[makeQuery(id+"F0.imprint","IMPRINT",EDGE,{"disambiguationData":[TD([[subQ2,-1.0]])],"derivedFrom":subQ1}),-1.0]])]});}
            var Q120;
            {var subQ0=sQuery(id+"F0.wireOp",EDGE,"E38");var subQ1=sQuery(id+"F0.wireOp",EDGE,"E17");var subQ2=makeQuery(id+"F0.imprint","INTERSECT",VERTEX,{"derivedFrom":[sQuery(id+"F0.wireOp",EDGE,"E4"),subQ1,subQ0]});Q120=makeQuery(id+"F0.imprint","IMPRINT",FACE,{"disambiguationData":[TD([[makeQuery(id+"F0.imprint","IMPRINT",EDGE,{"disambiguationData":[TD([[subQ2,-1.0]])],"derivedFrom":subQ1}),-1.0]])]});}
            var Q121;
            {var subQ0=sQuery(id+"F0.wireOp",EDGE,"E22");var subQ1=sQuery(id+"F0.wireOp",EDGE,"E6");var subQ2=makeQuery(id+"F0.imprint","INTERSECT",VERTEX,{"derivedFrom":[subQ1,subQ0,sQuery(id+"F0.wireOp",EDGE,"E38")]});Q121=makeQuery(id+"F0.imprint","IMPRINT",FACE,{"disambiguationData":[TD([[makeQuery(id+"F0.imprint","IMPRINT",EDGE,{"disambiguationData":[TD([[subQ2,-1.0]])],"derivedFrom":subQ1}),-1.0]])]});}
            var Q122;
            {var subQ0=sQuery(id+"F0.wireOp",EDGE,"E34");var subQ1=sQuery(id+"F0.wireOp",EDGE,"E4");var subQ2=makeQuery(id+"F0.imprint","INTERSECT",VERTEX,{"derivedFrom":[subQ1,sQuery(id+"F0.wireOp",EDGE,"E15"),subQ0]});Q122=makeQuery(id+"F0.imprint","IMPRINT",FACE,{"disambiguationData":[TD([[makeQuery(id+"F0.imprint","IMPRINT",EDGE,{"disambiguationData":[TD([[subQ2,-1.0]])],"derivedFrom":subQ1}),-1.0]])]});}
            var Q123;
            {var subQ0=sQuery(id+"F0.wireOp",EDGE,"E34");var subQ1=sQuery(id+"F0.wireOp",EDGE,"E15");var subQ2=makeQuery(id+"F0.imprint","INTERSECT",VERTEX,{"derivedFrom":[sQuery(id+"F0.wireOp",EDGE,"E4"),subQ1,subQ0]});Q123=makeQuery(id+"F0.imprint","IMPRINT",FACE,{"disambiguationData":[TD([[makeQuery(id+"F0.imprint","IMPRINT",EDGE,{"disambiguationData":[TD([[subQ2,1.0]])],"derivedFrom":subQ1}),-1.0]])]});}
            var Q124;
            {var subQ0=sQuery(id+"F0.wireOp",EDGE,"E34");var subQ1=sQuery(id+"F0.wireOp",EDGE,"E10");var subQ2=makeQuery(id+"F0.imprint","INTERSECT",VERTEX,{"derivedFrom":[sQuery(id+"F0.wireOp",EDGE,"E4"),subQ1,subQ0]});Q124=makeQuery(id+"F0.imprint","IMPRINT",FACE,{"disambiguationData":[TD([[makeQuery(id+"F0.imprint","IMPRINT",EDGE,{"disambiguationData":[TD([[subQ2,-1.0]])],"derivedFrom":subQ1}),-1.0]])]});}
            var Q125;
            {var subQ0=sQuery(id+"F0.wireOp",EDGE,"E17");var subQ1=sQuery(id+"F0.wireOp",EDGE,"E4");var subQ2=makeQuery(id+"F0.imprint","INTERSECT",VERTEX,{"derivedFrom":[subQ1,subQ0,sQuery(id+"F0.wireOp",EDGE,"E38")]});Q125=makeQuery(id+"F0.imprint","IMPRINT",FACE,{"disambiguationData":[TD([[makeQuery(id+"F0.imprint","IMPRINT",EDGE,{"disambiguationData":[TD([[subQ2,-1.0]])],"derivedFrom":subQ1}),-1.0]])]});}
            var Q126;
            {var subQ0=sQuery(id+"F0.wireOp",EDGE,"E34");var subQ1=sQuery(id+"F0.wireOp",EDGE,"E3");var subQ2=makeQuery(id+"F0.imprint","INTERSECT",VERTEX,{"derivedFrom":[subQ1,sQuery(id+"F0.wireOp",EDGE,"E10"),subQ0]});Q126=makeQuery(id+"F0.imprint","IMPRINT",FACE,{"disambiguationData":[TD([[makeQuery(id+"F0.imprint","IMPRINT",EDGE,{"disambiguationData":[TD([[subQ2,-1.0]])],"derivedFrom":subQ1}),-1.0]])]});}
            var Q127;
            {var subQ0=sQuery(id+"F0.wireOp",EDGE,"E34");var subQ1=sQuery(id+"F0.wireOp",EDGE,"E10");var subQ2=makeQuery(id+"F0.imprint","INTERSECT",VERTEX,{"derivedFrom":[sQuery(id+"F0.wireOp",EDGE,"E3"),subQ1,subQ0]});Q127=makeQuery(id+"F0.imprint","IMPRINT",FACE,{"disambiguationData":[TD([[makeQuery(id+"F0.imprint","IMPRINT",EDGE,{"disambiguationData":[TD([[subQ2,1.0]])],"derivedFrom":subQ1}),-1.0]])]});}
            var Q128;
            {var subQ0=sQuery(id+"F0.wireOp",EDGE,"E34");var subQ1=sQuery(id+"F0.wireOp",EDGE,"E11");var subQ2=makeQuery(id+"F0.imprint","INTERSECT",VERTEX,{"derivedFrom":[sQuery(id+"F0.wireOp",EDGE,"E3"),subQ1,subQ0]});Q128=makeQuery(id+"F0.imprint","IMPRINT",FACE,{"disambiguationData":[TD([[makeQuery(id+"F0.imprint","IMPRINT",EDGE,{"disambiguationData":[TD([[subQ2,-1.0]])],"derivedFrom":subQ1}),-1.0]])]});}
            var Q129;
            {var subQ0=sQuery(id+"F0.wireOp",EDGE,"E18");var subQ1=sQuery(id+"F0.wireOp",EDGE,"E3");var subQ2=makeQuery(id+"F0.imprint","INTERSECT",VERTEX,{"derivedFrom":[subQ1,subQ0,sQuery(id+"F0.wireOp",EDGE,"E38")]});Q129=makeQuery(id+"F0.imprint","IMPRINT",FACE,{"disambiguationData":[TD([[makeQuery(id+"F0.imprint","IMPRINT",EDGE,{"disambiguationData":[TD([[subQ2,-1.0]])],"derivedFrom":subQ1}),-1.0]])]});}
            var Q130;
            {var subQ0=sQuery(id+"F0.wireOp",EDGE,"E34");var subQ1=sQuery(id+"F0.wireOp",EDGE,"E5");var subQ2=makeQuery(id+"F0.imprint","INTERSECT",VERTEX,{"derivedFrom":[subQ1,sQuery(id+"F0.wireOp",EDGE,"E11"),subQ0]});Q130=makeQuery(id+"F0.imprint","IMPRINT",FACE,{"disambiguationData":[TD([[makeQuery(id+"F0.imprint","IMPRINT",EDGE,{"disambiguationData":[TD([[subQ2,-1.0]])],"derivedFrom":subQ1}),-1.0]])]});}
            var Q131;
            {var subQ0=sQuery(id+"F0.wireOp",EDGE,"E34");var subQ1=sQuery(id+"F0.wireOp",EDGE,"E11");var subQ2=makeQuery(id+"F0.imprint","INTERSECT",VERTEX,{"derivedFrom":[sQuery(id+"F0.wireOp",EDGE,"E5"),subQ1,subQ0]});Q131=makeQuery(id+"F0.imprint","IMPRINT",FACE,{"disambiguationData":[TD([[makeQuery(id+"F0.imprint","IMPRINT",EDGE,{"disambiguationData":[TD([[subQ2,1.0]])],"derivedFrom":subQ1}),-1.0]])]});}
            var Q132;
            {var subQ0=sQuery(id+"F0.wireOp",EDGE,"E34");var subQ1=sQuery(id+"F0.wireOp",EDGE,"E12");var subQ2=makeQuery(id+"F0.imprint","INTERSECT",VERTEX,{"derivedFrom":[sQuery(id+"F0.wireOp",EDGE,"E5"),subQ1,subQ0]});Q132=makeQuery(id+"F0.imprint","IMPRINT",FACE,{"disambiguationData":[TD([[makeQuery(id+"F0.imprint","IMPRINT",EDGE,{"disambiguationData":[TD([[subQ2,-1.0]])],"derivedFrom":subQ1}),-1.0]])]});}
            var Q133;
            {var subQ0=sQuery(id+"F0.wireOp",EDGE,"E34");var subQ1=sQuery(id+"F0.wireOp",EDGE,"E7");var subQ2=makeQuery(id+"F0.imprint","INTERSECT",VERTEX,{"derivedFrom":[subQ1,sQuery(id+"F0.wireOp",EDGE,"E12"),subQ0]});Q133=makeQuery(id+"F0.imprint","IMPRINT",FACE,{"disambiguationData":[TD([[makeQuery(id+"F0.imprint","IMPRINT",EDGE,{"disambiguationData":[TD([[subQ2,-1.0]])],"derivedFrom":subQ1}),-1.0]])]});}
            var Q134;
            {var subQ0=sQuery(id+"F0.wireOp",EDGE,"E34");var subQ1=sQuery(id+"F0.wireOp",EDGE,"E12");var subQ2=makeQuery(id+"F0.imprint","INTERSECT",VERTEX,{"derivedFrom":[sQuery(id+"F0.wireOp",EDGE,"E7"),subQ1,subQ0]});Q134=makeQuery(id+"F0.imprint","IMPRINT",FACE,{"disambiguationData":[TD([[makeQuery(id+"F0.imprint","IMPRINT",EDGE,{"disambiguationData":[TD([[subQ2,1.0]])],"derivedFrom":subQ1}),-1.0]])]});}
            var Q135;
            {var subQ0=sQuery(id+"F0.wireOp",EDGE,"E34");var subQ1=sQuery(id+"F0.wireOp",EDGE,"E13");var subQ2=makeQuery(id+"F0.imprint","INTERSECT",VERTEX,{"derivedFrom":[sQuery(id+"F0.wireOp",EDGE,"E7"),subQ1,subQ0]});Q135=makeQuery(id+"F0.imprint","IMPRINT",FACE,{"disambiguationData":[TD([[makeQuery(id+"F0.imprint","IMPRINT",EDGE,{"disambiguationData":[TD([[subQ2,-1.0]])],"derivedFrom":subQ1}),-1.0]])]});}
            var Q136;
            {var subQ0=sQuery(id+"F0.wireOp",EDGE,"E20");var subQ1=sQuery(id+"F0.wireOp",EDGE,"E7");var subQ2=makeQuery(id+"F0.imprint","INTERSECT",VERTEX,{"derivedFrom":[subQ1,subQ0,sQuery(id+"F0.wireOp",EDGE,"E38")]});Q136=makeQuery(id+"F0.imprint","IMPRINT",FACE,{"disambiguationData":[TD([[makeQuery(id+"F0.imprint","IMPRINT",EDGE,{"disambiguationData":[TD([[subQ2,-1.0]])],"derivedFrom":subQ1}),-1.0]])]});}
            var Q137;
            {var subQ0=sQuery(id+"F0.wireOp",EDGE,"E34");var subQ1=sQuery(id+"F0.wireOp",EDGE,"E8");var subQ2=makeQuery(id+"F0.imprint","INTERSECT",VERTEX,{"derivedFrom":[subQ1,sQuery(id+"F0.wireOp",EDGE,"E13"),subQ0]});Q137=makeQuery(id+"F0.imprint","IMPRINT",FACE,{"disambiguationData":[TD([[makeQuery(id+"F0.imprint","IMPRINT",EDGE,{"disambiguationData":[TD([[subQ2,-1.0]])],"derivedFrom":subQ1}),-1.0]])]});}
            var Q138;
            {var subQ0=sQuery(id+"F0.wireOp",EDGE,"E34");var subQ1=sQuery(id+"F0.wireOp",EDGE,"E13");var subQ2=makeQuery(id+"F0.imprint","INTERSECT",VERTEX,{"derivedFrom":[sQuery(id+"F0.wireOp",EDGE,"E8"),subQ1,subQ0]});Q138=makeQuery(id+"F0.imprint","IMPRINT",FACE,{"disambiguationData":[TD([[makeQuery(id+"F0.imprint","IMPRINT",EDGE,{"disambiguationData":[TD([[subQ2,1.0]])],"derivedFrom":subQ1}),-1.0]])]});}
            var Q139;
            {var subQ0=sQuery(id+"F0.wireOp",EDGE,"E34");var subQ1=sQuery(id+"F0.wireOp",EDGE,"E14");var subQ2=makeQuery(id+"F0.imprint","INTERSECT",VERTEX,{"derivedFrom":[sQuery(id+"F0.wireOp",EDGE,"E8"),subQ1,subQ0]});Q139=makeQuery(id+"F0.imprint","IMPRINT",FACE,{"disambiguationData":[TD([[makeQuery(id+"F0.imprint","IMPRINT",EDGE,{"disambiguationData":[TD([[subQ2,-1.0]])],"derivedFrom":subQ1}),-1.0]])]});}
            var Q140;
            {var subQ0=sQuery(id+"F0.wireOp",EDGE,"E21");var subQ1=sQuery(id+"F0.wireOp",EDGE,"E8");var subQ2=makeQuery(id+"F0.imprint","INTERSECT",VERTEX,{"derivedFrom":[subQ1,subQ0,sQuery(id+"F0.wireOp",EDGE,"E38")]});Q140=makeQuery(id+"F0.imprint","IMPRINT",FACE,{"disambiguationData":[TD([[makeQuery(id+"F0.imprint","IMPRINT",EDGE,{"disambiguationData":[TD([[subQ2,-1.0]])],"derivedFrom":subQ1}),-1.0]])]});}
            var Q141;
            {var subQ0=sQuery(id+"F0.wireOp",EDGE,"E34");var subQ1=sQuery(id+"F0.wireOp",EDGE,"E6");var subQ2=makeQuery(id+"F0.imprint","INTERSECT",VERTEX,{"derivedFrom":[subQ1,sQuery(id+"F0.wireOp",EDGE,"E14"),subQ0]});Q141=makeQuery(id+"F0.imprint","IMPRINT",FACE,{"disambiguationData":[TD([[makeQuery(id+"F0.imprint","IMPRINT",EDGE,{"disambiguationData":[TD([[subQ2,-1.0]])],"derivedFrom":subQ1}),-1.0]])]});}
            var Q142;
            {var subQ0=sQuery(id+"F0.wireOp",EDGE,"E34");var subQ1=sQuery(id+"F0.wireOp",EDGE,"E14");var subQ2=makeQuery(id+"F0.imprint","INTERSECT",VERTEX,{"derivedFrom":[sQuery(id+"F0.wireOp",EDGE,"E6"),subQ1,subQ0]});Q142=makeQuery(id+"F0.imprint","IMPRINT",FACE,{"disambiguationData":[TD([[makeQuery(id+"F0.imprint","IMPRINT",EDGE,{"disambiguationData":[TD([[subQ2,1.0]])],"derivedFrom":subQ1}),-1.0]])]});}
            var Q143;
            {var subQ0=sQuery(id+"F0.wireOp",EDGE,"E34");var subQ1=sQuery(id+"F0.wireOp",EDGE,"E15");var subQ2=makeQuery(id+"F0.imprint","INTERSECT",VERTEX,{"derivedFrom":[sQuery(id+"F0.wireOp",EDGE,"E6"),subQ1,subQ0]});Q143=makeQuery(id+"F0.imprint","IMPRINT",FACE,{"disambiguationData":[TD([[makeQuery(id+"F0.imprint","IMPRINT",EDGE,{"disambiguationData":[TD([[subQ2,-1.0]])],"derivedFrom":subQ1}),-1.0]])]});}
            var Q144;
            {var subQ0=sQuery(id+"F0.wireOp",EDGE,"E24");var subQ1=sQuery(id+"F0.wireOp",EDGE,"E6");var subQ2=makeQuery(id+"F0.imprint","INTERSECT",VERTEX,{"derivedFrom":[subQ1,subQ0]});Q144=makeQuery(id+"F0.imprint","IMPRINT",FACE,{"disambiguationData":[TD([[makeQuery(id+"F0.imprint","IMPRINT",EDGE,{"disambiguationData":[TD([[subQ2,-1.0]])],"derivedFrom":subQ1}),1.0]])]});}
            var Q145;
            {var subQ0=sQuery(id+"F0.wireOp",EDGE,"E21");var subQ1=sQuery(id+"F0.wireOp",EDGE,"E6");var subQ2=makeQuery(id+"F0.imprint","INTERSECT",VERTEX,{"derivedFrom":[subQ1,subQ0]});Q145=makeQuery(id+"F0.imprint","IMPRINT",FACE,{"disambiguationData":[TD([[makeQuery(id+"F0.imprint","IMPRINT",EDGE,{"disambiguationData":[TD([[subQ2,-1.0]])],"derivedFrom":subQ0}),1.0]])]});}
            var Q146;
            {var subQ0=sQuery(id+"F0.wireOp",EDGE,"E21");var subQ1=sQuery(id+"F0.wireOp",EDGE,"E14");var subQ2=makeQuery(id+"F0.imprint","INTERSECT",VERTEX,{"derivedFrom":[subQ1,subQ0]});Q146=makeQuery(id+"F0.imprint","IMPRINT",FACE,{"disambiguationData":[TD([[makeQuery(id+"F0.imprint","IMPRINT",EDGE,{"disambiguationData":[TD([[subQ2,-1.0]])],"derivedFrom":subQ1}),1.0]])]});}
            var Q147;
            {var subQ0=sQuery(id+"F0.wireOp",EDGE,"E29");var subQ1=sQuery(id+"F0.wireOp",EDGE,"E8");var subQ2=makeQuery(id+"F0.imprint","INTERSECT",VERTEX,{"derivedFrom":[subQ1,subQ0]});Q147=makeQuery(id+"F0.imprint","IMPRINT",FACE,{"disambiguationData":[TD([[makeQuery(id+"F0.imprint","IMPRINT",EDGE,{"disambiguationData":[TD([[subQ2,1.0]])],"derivedFrom":subQ0}),1.0]])]});}
            var Q148;
            {var subQ0=sQuery(id+"F0.wireOp",EDGE,"E29");var subQ1=sQuery(id+"F0.wireOp",EDGE,"E8");var subQ2=makeQuery(id+"F0.imprint","INTERSECT",VERTEX,{"derivedFrom":[subQ1,subQ0]});Q148=makeQuery(id+"F0.imprint","IMPRINT",FACE,{"disambiguationData":[TD([[makeQuery(id+"F0.imprint","IMPRINT",EDGE,{"disambiguationData":[TD([[subQ2,-1.0]])],"derivedFrom":subQ1}),1.0]])]});}
            var Q149;
            {var subQ0=sQuery(id+"F0.wireOp",EDGE,"E20");var subQ1=sQuery(id+"F0.wireOp",EDGE,"E8");var subQ2=makeQuery(id+"F0.imprint","INTERSECT",VERTEX,{"derivedFrom":[subQ1,subQ0]});Q149=makeQuery(id+"F0.imprint","IMPRINT",FACE,{"disambiguationData":[TD([[makeQuery(id+"F0.imprint","IMPRINT",EDGE,{"disambiguationData":[TD([[subQ2,-1.0]])],"derivedFrom":subQ0}),1.0]])]});}
            var Q150;
            {var subQ0=sQuery(id+"F0.wireOp",EDGE,"E20");var subQ1=sQuery(id+"F0.wireOp",EDGE,"E13");var subQ2=makeQuery(id+"F0.imprint","INTERSECT",VERTEX,{"derivedFrom":[subQ1,subQ0]});Q150=makeQuery(id+"F0.imprint","IMPRINT",FACE,{"disambiguationData":[TD([[makeQuery(id+"F0.imprint","IMPRINT",EDGE,{"disambiguationData":[TD([[subQ2,-1.0]])],"derivedFrom":subQ1}),1.0]])]});}
            var Q151;
            {var subQ0=sQuery(id+"F0.wireOp",EDGE,"E28");var subQ1=sQuery(id+"F0.wireOp",EDGE,"E7");var subQ2=makeQuery(id+"F0.imprint","INTERSECT",VERTEX,{"derivedFrom":[subQ1,subQ0]});Q151=makeQuery(id+"F0.imprint","IMPRINT",FACE,{"disambiguationData":[TD([[makeQuery(id+"F0.imprint","IMPRINT",EDGE,{"disambiguationData":[TD([[subQ2,1.0]])],"derivedFrom":subQ0}),1.0]])]});}
            var Q152;
            {var subQ0=sQuery(id+"F0.wireOp",EDGE,"E28");var subQ1=sQuery(id+"F0.wireOp",EDGE,"E7");var subQ2=makeQuery(id+"F0.imprint","INTERSECT",VERTEX,{"derivedFrom":[subQ1,subQ0]});Q152=makeQuery(id+"F0.imprint","IMPRINT",FACE,{"disambiguationData":[TD([[makeQuery(id+"F0.imprint","IMPRINT",EDGE,{"disambiguationData":[TD([[subQ2,-1.0]])],"derivedFrom":subQ1}),1.0]])]});}
            var Q153;
            {var subQ0=sQuery(id+"F0.wireOp",EDGE,"E19");var subQ1=sQuery(id+"F0.wireOp",EDGE,"E7");var subQ2=makeQuery(id+"F0.imprint","INTERSECT",VERTEX,{"derivedFrom":[subQ1,subQ0]});Q153=makeQuery(id+"F0.imprint","IMPRINT",FACE,{"disambiguationData":[TD([[makeQuery(id+"F0.imprint","IMPRINT",EDGE,{"disambiguationData":[TD([[subQ2,-1.0]])],"derivedFrom":subQ0}),1.0]])]});}
            var Q154;
            {var subQ0=sQuery(id+"F0.wireOp",EDGE,"E19");var subQ1=sQuery(id+"F0.wireOp",EDGE,"E12");var subQ2=makeQuery(id+"F0.imprint","INTERSECT",VERTEX,{"derivedFrom":[subQ1,subQ0]});Q154=makeQuery(id+"F0.imprint","IMPRINT",FACE,{"disambiguationData":[TD([[makeQuery(id+"F0.imprint","IMPRINT",EDGE,{"disambiguationData":[TD([[subQ2,-1.0]])],"derivedFrom":subQ1}),1.0]])]});}
            var Q155;
            {var subQ0=sQuery(id+"F0.wireOp",EDGE,"E27");var subQ1=sQuery(id+"F0.wireOp",EDGE,"E5");var subQ2=makeQuery(id+"F0.imprint","INTERSECT",VERTEX,{"derivedFrom":[subQ1,subQ0]});Q155=makeQuery(id+"F0.imprint","IMPRINT",FACE,{"disambiguationData":[TD([[makeQuery(id+"F0.imprint","IMPRINT",EDGE,{"disambiguationData":[TD([[subQ2,1.0]])],"derivedFrom":subQ0}),1.0]])]});}
            var Q156;
            {var subQ0=sQuery(id+"F0.wireOp",EDGE,"E27");var subQ1=sQuery(id+"F0.wireOp",EDGE,"E5");var subQ2=makeQuery(id+"F0.imprint","INTERSECT",VERTEX,{"derivedFrom":[subQ1,subQ0]});Q156=makeQuery(id+"F0.imprint","IMPRINT",FACE,{"disambiguationData":[TD([[makeQuery(id+"F0.imprint","IMPRINT",EDGE,{"disambiguationData":[TD([[subQ2,-1.0]])],"derivedFrom":subQ1}),1.0]])]});}
            var Q157;
            {var subQ0=sQuery(id+"F0.wireOp",EDGE,"E18");var subQ1=sQuery(id+"F0.wireOp",EDGE,"E5");var subQ2=makeQuery(id+"F0.imprint","INTERSECT",VERTEX,{"derivedFrom":[subQ1,subQ0]});Q157=makeQuery(id+"F0.imprint","IMPRINT",FACE,{"disambiguationData":[TD([[makeQuery(id+"F0.imprint","IMPRINT",EDGE,{"disambiguationData":[TD([[subQ2,-1.0]])],"derivedFrom":subQ0}),1.0]])]});}
            var Q158;
            {var subQ0=sQuery(id+"F0.wireOp",EDGE,"E18");var subQ1=sQuery(id+"F0.wireOp",EDGE,"E11");var subQ2=makeQuery(id+"F0.imprint","INTERSECT",VERTEX,{"derivedFrom":[subQ1,subQ0]});Q158=makeQuery(id+"F0.imprint","IMPRINT",FACE,{"disambiguationData":[TD([[makeQuery(id+"F0.imprint","IMPRINT",EDGE,{"disambiguationData":[TD([[subQ2,-1.0]])],"derivedFrom":subQ1}),1.0]])]});}
            var Q159;
            {var subQ0=sQuery(id+"F0.wireOp",EDGE,"E26");var subQ1=sQuery(id+"F0.wireOp",EDGE,"E3");var subQ2=makeQuery(id+"F0.imprint","INTERSECT",VERTEX,{"derivedFrom":[subQ1,subQ0]});Q159=makeQuery(id+"F0.imprint","IMPRINT",FACE,{"disambiguationData":[TD([[makeQuery(id+"F0.imprint","IMPRINT",EDGE,{"disambiguationData":[TD([[subQ2,1.0]])],"derivedFrom":subQ0}),1.0]])]});}
            var Q160;
            {var subQ0=sQuery(id+"F0.wireOp",EDGE,"E17");var subQ1=sQuery(id+"F0.wireOp",EDGE,"E3");var subQ2=makeQuery(id+"F0.imprint","INTERSECT",VERTEX,{"derivedFrom":[subQ1,subQ0]});Q160=makeQuery(id+"F0.imprint","IMPRINT",FACE,{"disambiguationData":[TD([[makeQuery(id+"F0.imprint","IMPRINT",EDGE,{"disambiguationData":[TD([[subQ2,1.0]])],"derivedFrom":subQ1}),1.0]])]});}
            var Q161;
            {var subQ0=sQuery(id+"F0.wireOp",EDGE,"E17");var subQ1=sQuery(id+"F0.wireOp",EDGE,"E3");var subQ2=makeQuery(id+"F0.imprint","INTERSECT",VERTEX,{"derivedFrom":[subQ1,subQ0]});Q161=makeQuery(id+"F0.imprint","IMPRINT",FACE,{"disambiguationData":[TD([[makeQuery(id+"F0.imprint","IMPRINT",EDGE,{"disambiguationData":[TD([[subQ2,-1.0]])],"derivedFrom":subQ0}),1.0]])]});}
            var Q162;
            {var subQ0=sQuery(id+"F0.wireOp",EDGE,"E17");var subQ1=sQuery(id+"F0.wireOp",EDGE,"E10");var subQ2=makeQuery(id+"F0.imprint","INTERSECT",VERTEX,{"derivedFrom":[subQ1,subQ0]});Q162=makeQuery(id+"F0.imprint","IMPRINT",FACE,{"disambiguationData":[TD([[makeQuery(id+"F0.imprint","IMPRINT",EDGE,{"disambiguationData":[TD([[subQ2,-1.0]])],"derivedFrom":subQ1}),1.0]])]});}
            var Q163;
            {var subQ0=sQuery(id+"F0.wireOp",EDGE,"E25");var subQ1=sQuery(id+"F0.wireOp",EDGE,"E4");var subQ2=makeQuery(id+"F0.imprint","INTERSECT",VERTEX,{"derivedFrom":[subQ1,subQ0]});Q163=makeQuery(id+"F0.imprint","IMPRINT",FACE,{"disambiguationData":[TD([[makeQuery(id+"F0.imprint","IMPRINT",EDGE,{"disambiguationData":[TD([[subQ2,1.0]])],"derivedFrom":subQ0}),1.0]])]});}
            var Q164;
            {var subQ0=sQuery(id+"F0.wireOp",EDGE,"E25");var subQ1=sQuery(id+"F0.wireOp",EDGE,"E4");var subQ2=makeQuery(id+"F0.imprint","INTERSECT",VERTEX,{"derivedFrom":[subQ1,subQ0]});Q164=makeQuery(id+"F0.imprint","IMPRINT",FACE,{"disambiguationData":[TD([[makeQuery(id+"F0.imprint","IMPRINT",EDGE,{"disambiguationData":[TD([[subQ2,-1.0]])],"derivedFrom":subQ1}),1.0]])]});}
            var Q165;
            {var subQ0=sQuery(id+"F0.wireOp",EDGE,"E22");var subQ1=sQuery(id+"F0.wireOp",EDGE,"E4");var subQ2=makeQuery(id+"F0.imprint","INTERSECT",VERTEX,{"derivedFrom":[subQ1,subQ0]});Q165=makeQuery(id+"F0.imprint","IMPRINT",FACE,{"disambiguationData":[TD([[makeQuery(id+"F0.imprint","IMPRINT",EDGE,{"disambiguationData":[TD([[subQ2,-1.0]])],"derivedFrom":subQ0}),1.0]])]});}
            var Q166;
            {var subQ0=sQuery(id+"F0.wireOp",EDGE,"E22");var subQ1=sQuery(id+"F0.wireOp",EDGE,"E15");var subQ2=makeQuery(id+"F0.imprint","INTERSECT",VERTEX,{"derivedFrom":[subQ1,subQ0]});Q166=makeQuery(id+"F0.imprint","IMPRINT",FACE,{"disambiguationData":[TD([[makeQuery(id+"F0.imprint","IMPRINT",EDGE,{"disambiguationData":[TD([[subQ2,-1.0]])],"derivedFrom":subQ1}),1.0]])]});}
            var Q167;
            {var subQ0=sQuery(id+"F0.wireOp",EDGE,"E24");var subQ1=sQuery(id+"F0.wireOp",EDGE,"E6");var subQ2=makeQuery(id+"F0.imprint","INTERSECT",VERTEX,{"derivedFrom":[subQ1,subQ0]});Q167=makeQuery(id+"F0.imprint","IMPRINT",FACE,{"disambiguationData":[TD([[makeQuery(id+"F0.imprint","IMPRINT",EDGE,{"disambiguationData":[TD([[subQ2,1.0]])],"derivedFrom":subQ0}),1.0]])]});}
            var Q168;
            {var subQ0=sQuery(id+"F0.wireOp",EDGE,"E24");var subQ1=sQuery(id+"F0.wireOp",EDGE,"E6");var subQ2=makeQuery(id+"F0.imprint","INTERSECT",VERTEX,{"derivedFrom":[subQ1,subQ0]});Q168=makeQuery(id+"F0.imprint","IMPRINT",FACE,{"disambiguationData":[TD([[makeQuery(id+"F0.imprint","IMPRINT",EDGE,{"disambiguationData":[TD([[subQ2,1.0]])],"derivedFrom":subQ0}),1.0]])]});}
            var Q169;
            {var subQ0=sQuery(id+"F0.wireOp",EDGE,"E22");var subQ1=sQuery(id+"F0.wireOp",EDGE,"E15");var subQ2=makeQuery(id+"F0.imprint","INTERSECT",VERTEX,{"derivedFrom":[subQ1,subQ0]});Q169=makeQuery(id+"F0.imprint","IMPRINT",FACE,{"disambiguationData":[TD([[makeQuery(id+"F0.imprint","IMPRINT",EDGE,{"disambiguationData":[TD([[subQ2,-1.0]])],"derivedFrom":subQ1}),1.0]])]});}
            var Q170;
            {var subQ0=sQuery(id+"F0.wireOp",EDGE,"E22");var subQ1=sQuery(id+"F0.wireOp",EDGE,"E4");var subQ2=makeQuery(id+"F0.imprint","INTERSECT",VERTEX,{"derivedFrom":[subQ1,subQ0]});Q170=makeQuery(id+"F0.imprint","IMPRINT",FACE,{"disambiguationData":[TD([[makeQuery(id+"F0.imprint","IMPRINT",EDGE,{"disambiguationData":[TD([[subQ2,-1.0]])],"derivedFrom":subQ0}),1.0]])]});}
            var Q171;
            {var subQ0=sQuery(id+"F0.wireOp",EDGE,"E25");var subQ1=sQuery(id+"F0.wireOp",EDGE,"E4");var subQ2=makeQuery(id+"F0.imprint","INTERSECT",VERTEX,{"derivedFrom":[subQ1,subQ0]});Q171=makeQuery(id+"F0.imprint","IMPRINT",FACE,{"disambiguationData":[TD([[makeQuery(id+"F0.imprint","IMPRINT",EDGE,{"disambiguationData":[TD([[subQ2,-1.0]])],"derivedFrom":subQ1}),1.0]])]});}
            var Q172;
            {var subQ0=sQuery(id+"F0.wireOp",EDGE,"E25");var subQ1=sQuery(id+"F0.wireOp",EDGE,"E4");var subQ2=makeQuery(id+"F0.imprint","INTERSECT",VERTEX,{"derivedFrom":[subQ1,subQ0]});Q172=makeQuery(id+"F0.imprint","IMPRINT",FACE,{"disambiguationData":[TD([[makeQuery(id+"F0.imprint","IMPRINT",EDGE,{"disambiguationData":[TD([[subQ2,1.0]])],"derivedFrom":subQ0}),1.0]])]});}
            extrude(context, id + "F5", {"entities" : qUnion([Q0, Q1, Q2, Q3, Q4, Q5, Q6, Q7, Q8, Q9, Q10, Q11, Q12, Q13, Q14, Q15, Q16, Q17, Q18, Q19, Q20, Q21, Q22, Q23, Q24, Q25, Q26, Q27, Q28, Q29, Q30, Q31, Q32, Q33, Q34, Q35, Q36, Q37, Q38, Q39, Q40, Q41, Q42, Q43, Q44, Q45, Q46, Q47, Q48, Q49, Q50, Q51, Q52, Q53, Q54, Q55, Q56, Q57, Q58, Q59, Q60, Q61, Q62, Q63, Q64, Q65, Q66, Q67, Q68, Q69, Q70, Q71, Q72, Q73, Q74, Q75, Q76, Q77, Q78, Q79, Q80, Q81, Q82, Q83, Q84, Q85, Q86, Q87, Q88, Q89, Q90, Q91, Q92, Q93, Q94, Q95, Q96, Q97, Q98, Q99, Q100, Q101, Q102, Q103, Q104, Q105, Q106, Q107, Q108, Q109, Q110, Q111, Q112, Q113, Q114, Q115, Q116, Q117, Q118, Q119, Q120, Q121, Q122, Q123, Q124, Q125, Q126, Q127, Q128, Q129, Q130, Q131, Q132, Q133, Q134, Q135, Q136, Q137, Q138, Q139, Q140, Q141, Q142, Q143, Q144, Q145, Q146, Q147, Q148, Q149, Q150, Q151, Q152, Q153, Q154, Q155, Q156, Q157, Q158, Q159, Q160, Q161, Q162, Q163, Q164, Q165, Q166, Q167, Q168, Q169, Q170, Q171, Q172]), "depth" : 6 * mm, "hasDraft" : true, "draftAngle" : 6 * degree, "draftPullDirection" : true});
        }
        {
            var Q0;
            Q0=qCreatedBy(makeId("Top.planeOp"),FACE);
            cPlane(context, id + "F6", {"entities" : qUnion([Q0]), "cplaneType" : CPlaneType.OFFSET, "offset" : 0 * mm, "width" : 150 * mm, "height" : 150 * mm});
        }
    });
